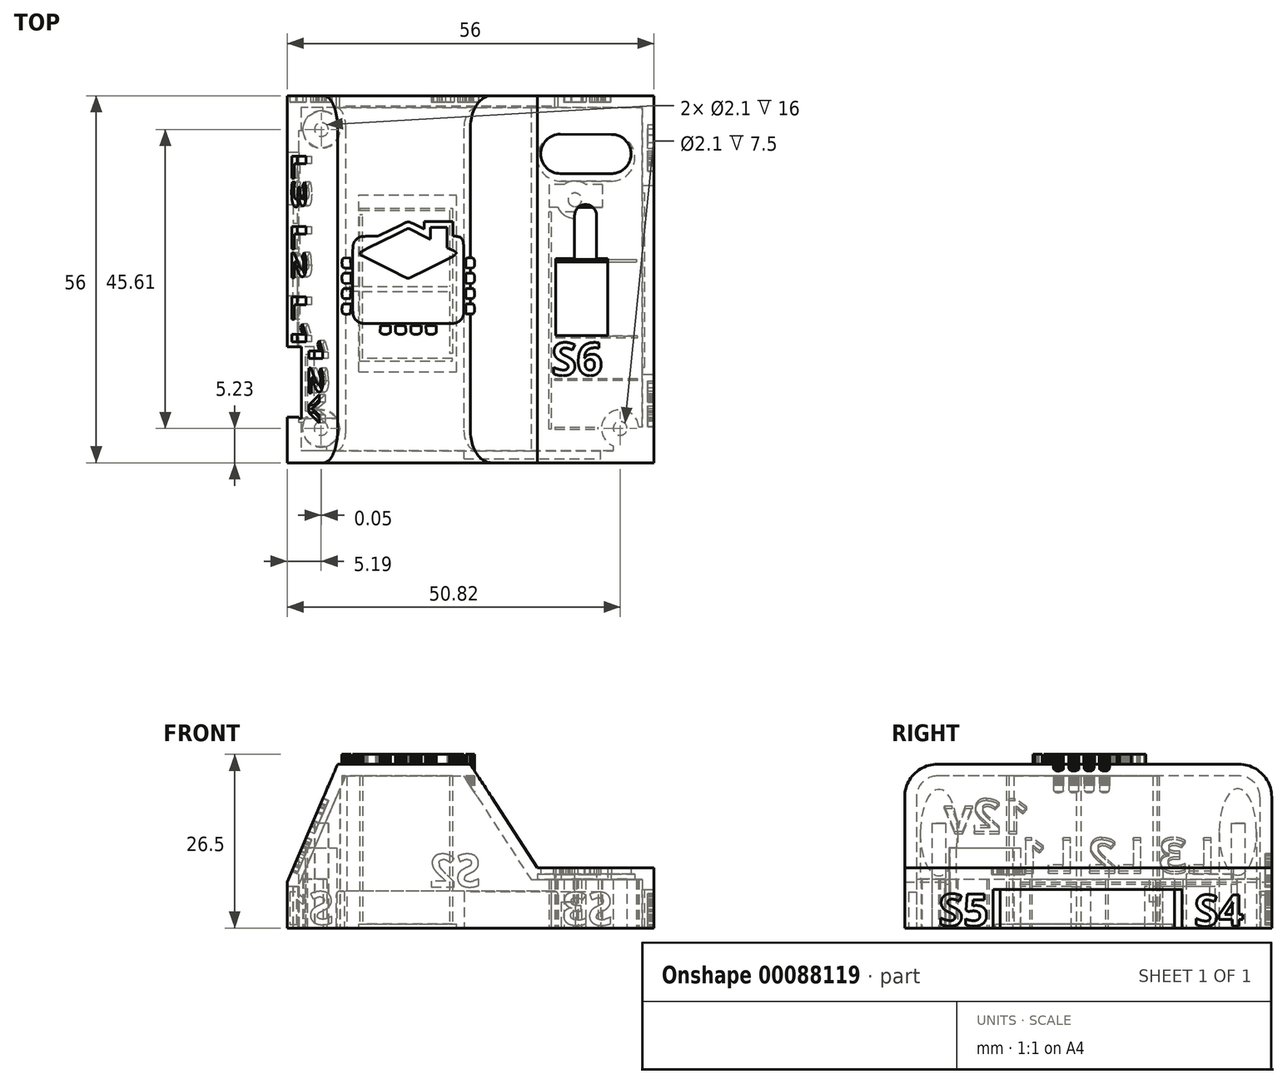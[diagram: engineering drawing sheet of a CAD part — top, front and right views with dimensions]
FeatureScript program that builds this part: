
annotation { "Feature Type Name" : "Feature", "Feature Type Description" : "" }
export const myFeature = defineFeature(function(context is Context, id is Id, definition is map)
    precondition{}
    {
        {
            var Q0;
            Q0=qCreatedBy(makeId("Top.planeOp"),FACE);
            var sketch = newSketch(context, id + "F0", { "sketchPlane" : qUnion([Q0])});
            skLineSegment(sketch, "E0.rect.bottom", {"start": v(22.84, -21.13) * mm, "end": v(-26.83, -21.13) * mm});
            skLineSegment(sketch, "E0.rect.top", {"start": v(22.84, 28.7) * mm, "end": v(-26.83, 28.7) * mm});
            skLineSegment(sketch, "E0.rect.left", {"start": v(22.84, -21.13) * mm, "end": v(22.84, 28.7) * mm});
            skPoint(sketch, "E0.rect.middle", {"position": v(-2, 3.78) * mm});
            skCircle(sketch, "E1", {"center": v(-24.81, -18.99) * mm, "radius": 1.05 * mm});
            skCircle(sketch, "E2", {"center": v(-24.76, 26.62) * mm, "radius": 1.05 * mm});
            skCircle(sketch, "E3", {"center": v(13.92, 15.91) * mm, "radius": 1.05 * mm});
            skLineSegment(sketch, "E4", {"start": v(-2, -21.13) * mm, "end": v(-2, -18.21) * mm});
            skCircle(sketch, "E5.MirrorC", {"center": v(20.82, -18.99) * mm, "radius": 1.05 * mm});
            skLineSegment(sketch, "E6.rect.bottom", {"start": v(24.75, -22.97) * mm, "end": v(-28.75, -22.97) * mm});
            skLineSegment(sketch, "E6.rect.top", {"start": v(24.75, 30.53) * mm, "end": v(-28.75, 30.53) * mm});
            skLineSegment(sketch, "E6.rect.left", {"start": v(24.75, -22.97) * mm, "end": v(24.75, 30.53) * mm});
            skLineSegment(sketch, "E6.rect.right", {"start": v(-28.75, -22.97) * mm, "end": v(-28.75, 30.53) * mm});
            skLineSegment(sketch, "E7.rect.bottom", {"start": v(26, -24.22) * mm, "end": v(-30, -24.22) * mm});
            skLineSegment(sketch, "E7.rect.top", {"start": v(26, 31.78) * mm, "end": v(-30, 31.78) * mm});
            skLineSegment(sketch, "E7.rect.left", {"start": v(26, -24.22) * mm, "end": v(26, 31.78) * mm});
            skLineSegment(sketch, "E7.rect.right", {"start": v(-30, -24.22) * mm, "end": v(-30, 31.78) * mm});
            skPoint(sketch, "E8", {"position": v(8.65, 14) * mm});
            skSolve(sketch);
        }
        {
            var Q0;
            Q0=qSketchRegion(id+"F0",true);
            var Q1;
            Q1=makeQuery(id+"F0.imprint","IMPRINT",FACE,{"disambiguationData":[TD([[makeQuery(id+"F0.imprint","IMPRINT",EDGE,{"derivedFrom":sQuery(id+"F0.wireOp",EDGE,"E1")}),-1.0]])]});
            extrude(context, id + "F1", {"entities" : qUnion([Q0, Q1]), "depth" : 25 * mm});
        }
        {
            var Q0;
            Q0=qCreatedBy(makeId("Front.planeOp"),FACE);
            var sketch = newSketch(context, id + "F2", { "sketchPlane" : qUnion([Q0])});
            skLineSegment(sketch, "E9", {"start": v(0, 0) * mm, "end": v(0, 7) * mm});
            skLineSegment(sketch, "E10", {"start": v(0, 7) * mm, "end": v(26.03, 7) * mm});
            skLineSegment(sketch, "E11", {"start": v(26.03, 9.19) * mm, "end": v(26.03, 25.51) * mm});
            skLineSegment(sketch, "E12", {"start": v(15.3, 7) * mm, "end": v(26.03, 7) * mm});
            skLineSegment(sketch, "E13", {"start": v(0, 7) * mm, "end": v(-30.02, 7) * mm});
            skLineSegment(sketch, "E14", {"start": v(-30.02, 7) * mm, "end": v(-22.06, 25.51) * mm});
            skLineSegment(sketch, "E15", {"start": v(-22.06, 25.51) * mm, "end": v(-2.39, 25.51) * mm});
            skLineSegment(sketch, "E16", {"start": v(26.03, 25.51) * mm, "end": v(-2.39, 25.51) * mm});
            skLineSegment(sketch, "E17", {"start": v(-22.06, 25.51) * mm, "end": v(-30.02, 25.51) * mm});
            skLineSegment(sketch, "E18", {"start": v(-30.02, 25.51) * mm, "end": v(-30.02, 7) * mm});
            skLineSegment(sketch, "E19", {"start": v(18.06, 10.7) * mm, "end": v(18.04, 10.7) * mm});
            skLineSegment(sketch, "E20", {"start": v(19.86, 9.19) * mm, "end": v(8.2, 9.19) * mm});
            skLineSegment(sketch, "E21", {"start": v(8.2, 9.19) * mm, "end": v(-2.39, 25.51) * mm});
            skLineSegment(sketch, "E22", {"start": v(19.86, 9.19) * mm, "end": v(26.03, 9.19) * mm});
            skSolve(sketch);
        }
        {
            var Q0;
            Q0=makeQuery(id+"F2.imprint","IMPRINT",FACE,{"disambiguationData":[TD([[makeQuery(id+"F2.imprint","IMPRINT",EDGE,{"derivedFrom":sQuery(id+"F2.wireOp",EDGE,"E14")}),1.0]])]});
            var Q1;
            {var subQ0=sQuery(id+"F2.wireOp",EDGE,"E11");Q1=makeQuery(id+"F2.imprint","IMPRINT",FACE,{"disambiguationData":[TD([[makeQuery(id+"F2.imprint","IMPRINT",EDGE,{"derivedFrom":subQ0}),1.0]])]});}
            extrude(context, id + "F3", {"entities" : qUnion([Q0, Q1]), "operationType" : NewBodyOperationType.REMOVE, "endBound" : BoundingType.UP_TO_NEXT, "oppositeDirection" : true, "depth" : 25 * mm, "hasSecondDirection" : true, "secondDirectionOppositeDirection" : false, "secondDirectionDepth" : 25 * mm});
        }
        {
            var Q0;
            Q0=makeQuery(id+"F1.opExtrude","CAP_EDGE",EDGE,{"disambiguationData":[OSD([sQuery(id+"F0.wireOp",EDGE,"E7.rect.right")])],"isStart":false});
            var Q1;
            Q1=makeQuery(id+"F3.boolean.opBoolean","COPY",EDGE,{"derivedFrom":makeQuery(id+"F3.opExtrude","TWEAK_EDGE",EDGE,{"derivedFrom":[makeQuery(id+"F1.opExtrude","CAP_FACE",FACE,{"disambiguationData":[OSD([sQuery(id+"F0.wireOp",EDGE,"E1"),sQuery(id+"F0.wireOp",EDGE,"E2"),sQuery(id+"F0.wireOp",EDGE,"E3"),sQuery(id+"F0.wireOp",EDGE,"E5.MirrorC"),sQuery(id+"F0.wireOp",EDGE,"E7.rect.bottom"),sQuery(id+"F0.wireOp",EDGE,"E7.rect.top"),sQuery(id+"F0.wireOp",EDGE,"E7.rect.left"),sQuery(id+"F0.wireOp",EDGE,"E7.rect.right")])],"isStart":false}),makeQuery(id+"F2.imprint","IMPRINT",EDGE,{"derivedFrom":sQuery(id+"F2.wireOp",EDGE,"ff17f17f-c23f-4b7b-92e3-773d52701edb")})]})});
            var Q2;
            Q2=makeQuery(id+"F3.boolean.opBoolean","COPY",EDGE,{"derivedFrom":makeQuery(id+"F3.opExtrude","TWEAK_EDGE",EDGE,{"derivedFrom":[makeQuery(id+"F1.opExtrude","CAP_FACE",FACE,{"disambiguationData":[OSD([sQuery(id+"F0.wireOp",EDGE,"E1"),sQuery(id+"F0.wireOp",EDGE,"E2"),sQuery(id+"F0.wireOp",EDGE,"E3"),sQuery(id+"F0.wireOp",EDGE,"E5.MirrorC"),sQuery(id+"F0.wireOp",EDGE,"E7.rect.bottom"),sQuery(id+"F0.wireOp",EDGE,"E7.rect.top"),sQuery(id+"F0.wireOp",EDGE,"E7.rect.left"),sQuery(id+"F0.wireOp",EDGE,"E7.rect.right")])],"isStart":false}),makeQuery(id+"F2.imprint","IMPRINT",EDGE,{"derivedFrom":sQuery(id+"F2.wireOp",EDGE,"7c30f75c-de24-4105-9ec6-0528e7197d9e")})]})});
            var Q3;
            {var subQ0=sQuery(id+"F2.wireOp",EDGE,"cpQ2IQLn-lepx-jHqE-Occg-QwCyzWVKbBFz");var subQ1=sQuery(id+"F2.wireOp",EDGE,"9136473a-ce9f-4df1-8e41-d79c079f6f02");var subQ2=makeQuery(id+"F2.imprint","INTERSECT",VERTEX,{"disambiguationData":[OD(0.0)],"derivedFrom":[subQ1,subQ0]});var subQ4=makeQuery(id+"F2.imprint","INTERSECT",VERTEX,{"disambiguationData":[OD(1.0)],"derivedFrom":[subQ1,subQ0]});Q3=makeQuery(id+"F3.boolean.opBoolean","COPY",EDGE,{"derivedFrom":makeQuery(id+"F3.opExtrude","TWEAK_EDGE",EDGE,{"derivedFrom":[makeQuery(id+"F1.opExtrude","CAP_FACE",FACE,{"disambiguationData":[OSD([sQuery(id+"F0.wireOp",EDGE,"E1"),sQuery(id+"F0.wireOp",EDGE,"E2"),sQuery(id+"F0.wireOp",EDGE,"E3"),sQuery(id+"F0.wireOp",EDGE,"E5.MirrorC"),sQuery(id+"F0.wireOp",EDGE,"E7.rect.bottom"),sQuery(id+"F0.wireOp",EDGE,"E7.rect.top"),sQuery(id+"F0.wireOp",EDGE,"E7.rect.left"),sQuery(id+"F0.wireOp",EDGE,"E7.rect.right")])],"isStart":false}),makeQuery(id+"F2.imprint","IMPRINT",EDGE,{"disambiguationData":[TD([[subQ4,1.0]])],"derivedFrom":subQ0}),makeQuery(id+"F2.imprint","IMPRINT",EDGE,{"disambiguationData":[TD([[subQ2,1.0]])],"derivedFrom":subQ0}),makeQuery(id+"F2.imprint","IMPRINT",EDGE,{"disambiguationData":[TD([[subQ2,-1.0]])],"derivedFrom":subQ0})]})});}
            var Q4;
            {var subQ0=sQuery(id+"F2.wireOp",EDGE,"cpQ2IQLn-lepx-jHqE-Occg-QwCyzWVKbBFz");var subQ1=sQuery(id+"F2.wireOp",EDGE,"9136473a-ce9f-4df1-8e41-d79c079f6f02");var subQ2=makeQuery(id+"F2.imprint","INTERSECT",VERTEX,{"disambiguationData":[OD(0.0)],"derivedFrom":[subQ1,subQ0]});var subQ3=sQuery(id+"F2.wireOp",EDGE,"7c30f75c-de24-4105-9ec6-0528e7197d9e");var subQ4=makeQuery(id+"F2.imprint","INTERSECT",VERTEX,{"derivedFrom":[subQ3,subQ0]});var subQ5=makeQuery(id+"F2.imprint","INTERSECT",VERTEX,{"disambiguationData":[OD(1.0)],"derivedFrom":[subQ1,subQ0]});Q4=makeQuery(id+"F3.boolean.opBoolean","COPY",EDGE,{"derivedFrom":makeQuery(id+"F3.opExtrude","TWEAK_EDGE",EDGE,{"disambiguationData":[OD(0.0)],"derivedFrom":[makeQuery(id+"F2.imprint","IMPRINT",EDGE,{"disambiguationData":[TD([[subQ4,1.0]])],"derivedFrom":subQ3}),makeQuery(id+"F2.imprint","IMPRINT",EDGE,{"disambiguationData":[TD([[subQ5,1.0]])],"derivedFrom":subQ0}),makeQuery(id+"F2.imprint","IMPRINT",EDGE,{"disambiguationData":[TD([[subQ2,1.0]])],"derivedFrom":subQ0}),makeQuery(id+"F2.imprint","IMPRINT",EDGE,{"disambiguationData":[TD([[subQ2,-1.0]])],"derivedFrom":subQ0})]})});}
            var Q5;
            {var subQ0=sQuery(id+"F2.wireOp",EDGE,"cpQ2IQLn-lepx-jHqE-Occg-QwCyzWVKbBFz");var subQ1=sQuery(id+"F2.wireOp",EDGE,"9136473a-ce9f-4df1-8e41-d79c079f6f02");var subQ2=makeQuery(id+"F2.imprint","INTERSECT",VERTEX,{"disambiguationData":[OD(0.0)],"derivedFrom":[subQ1,subQ0]});var subQ3=sQuery(id+"F2.wireOp",EDGE,"7c30f75c-de24-4105-9ec6-0528e7197d9e");var subQ4=makeQuery(id+"F2.imprint","INTERSECT",VERTEX,{"derivedFrom":[subQ3,subQ0]});var subQ5=makeQuery(id+"F2.imprint","INTERSECT",VERTEX,{"disambiguationData":[OD(1.0)],"derivedFrom":[subQ1,subQ0]});Q5=makeQuery(id+"F3.boolean.opBoolean","COPY",EDGE,{"derivedFrom":makeQuery(id+"F3.opExtrude","TWEAK_EDGE",EDGE,{"disambiguationData":[OD(1.0)],"derivedFrom":[makeQuery(id+"F2.imprint","IMPRINT",EDGE,{"disambiguationData":[TD([[subQ4,1.0]])],"derivedFrom":subQ3}),makeQuery(id+"F2.imprint","IMPRINT",EDGE,{"disambiguationData":[TD([[subQ5,1.0]])],"derivedFrom":subQ0}),makeQuery(id+"F2.imprint","IMPRINT",EDGE,{"disambiguationData":[TD([[subQ2,1.0]])],"derivedFrom":subQ0}),makeQuery(id+"F2.imprint","IMPRINT",EDGE,{"disambiguationData":[TD([[subQ2,-1.0]])],"derivedFrom":subQ0})]})});}
            var Q6;
            Q6=makeQuery(id+"F1.opExtrude","CAP_EDGE",EDGE,{"disambiguationData":[OSD([sQuery(id+"F0.wireOp",EDGE,"E7.rect.bottom")])],"isStart":false});
            var Q7;
            {var subQ0=sQuery(id+"F2.wireOp",EDGE,"cpQ2IQLn-lepx-jHqE-Occg-QwCyzWVKbBFz");var subQ1=sQuery(id+"F2.wireOp",EDGE,"9136473a-ce9f-4df1-8e41-d79c079f6f02");var subQ2=makeQuery(id+"F2.imprint","INTERSECT",VERTEX,{"disambiguationData":[OD(0.0)],"derivedFrom":[subQ1,subQ0]});var subQ4=makeQuery(id+"F2.imprint","INTERSECT",VERTEX,{"disambiguationData":[OD(1.0)],"derivedFrom":[subQ1,subQ0]});Q7=makeQuery(id+"F3.boolean.opBoolean","COPY",EDGE,{"derivedFrom":makeQuery(id+"F3.opExtrude","TWEAK_EDGE",EDGE,{"derivedFrom":[makeQuery(id+"F1.opExtrude","SWEPT_FACE",FACE,{"disambiguationData":[OSD([sQuery(id+"F0.wireOp",EDGE,"E7.rect.bottom")])]}),makeQuery(id+"F2.imprint","IMPRINT",EDGE,{"disambiguationData":[TD([[subQ4,1.0]])],"derivedFrom":subQ0}),makeQuery(id+"F2.imprint","IMPRINT",EDGE,{"disambiguationData":[TD([[subQ2,1.0]])],"derivedFrom":subQ0}),makeQuery(id+"F2.imprint","IMPRINT",EDGE,{"disambiguationData":[TD([[subQ2,-1.0]])],"derivedFrom":subQ0})]})});}
            var Q8;
            Q8=makeQuery(id+"F1.opExtrude","CAP_EDGE",EDGE,{"disambiguationData":[OSD([sQuery(id+"F0.wireOp",EDGE,"E7.rect.top")])],"isStart":false});
            var Q9;
            {var subQ0=sQuery(id+"F2.wireOp",EDGE,"cpQ2IQLn-lepx-jHqE-Occg-QwCyzWVKbBFz");var subQ1=sQuery(id+"F2.wireOp",EDGE,"9136473a-ce9f-4df1-8e41-d79c079f6f02");var subQ2=makeQuery(id+"F2.imprint","INTERSECT",VERTEX,{"disambiguationData":[OD(0.0)],"derivedFrom":[subQ1,subQ0]});var subQ4=makeQuery(id+"F2.imprint","INTERSECT",VERTEX,{"disambiguationData":[OD(1.0)],"derivedFrom":[subQ1,subQ0]});Q9=makeQuery(id+"F3.boolean.opBoolean","COPY",EDGE,{"derivedFrom":makeQuery(id+"F3.opExtrude","TWEAK_EDGE",EDGE,{"derivedFrom":[makeQuery(id+"F1.opExtrude","SWEPT_FACE",FACE,{"disambiguationData":[OSD([sQuery(id+"F0.wireOp",EDGE,"E7.rect.top")])]}),makeQuery(id+"F2.imprint","IMPRINT",EDGE,{"disambiguationData":[TD([[subQ4,1.0]])],"derivedFrom":subQ0}),makeQuery(id+"F2.imprint","IMPRINT",EDGE,{"disambiguationData":[TD([[subQ2,1.0]])],"derivedFrom":subQ0}),makeQuery(id+"F2.imprint","IMPRINT",EDGE,{"disambiguationData":[TD([[subQ2,-1.0]])],"derivedFrom":subQ0})]})});}
            var Q10;
            Q10=makeQuery(id+"F3.boolean.opBoolean","COPY",EDGE,{"derivedFrom":makeQuery(id+"F3.opExtrude","TWEAK_EDGE",EDGE,{"derivedFrom":[makeQuery(id+"F1.opExtrude","CAP_FACE",FACE,{"disambiguationData":[OSD([sQuery(id+"F0.wireOp",EDGE,"E1"),sQuery(id+"F0.wireOp",EDGE,"E2"),sQuery(id+"F0.wireOp",EDGE,"E3"),sQuery(id+"F0.wireOp",EDGE,"E5.MirrorC"),sQuery(id+"F0.wireOp",EDGE,"E7.rect.bottom"),sQuery(id+"F0.wireOp",EDGE,"E7.rect.top"),sQuery(id+"F0.wireOp",EDGE,"E7.rect.left"),sQuery(id+"F0.wireOp",EDGE,"E7.rect.right")])],"isStart":false}),makeQuery(id+"F2.imprint","IMPRINT",EDGE,{"derivedFrom":sQuery(id+"F2.wireOp",EDGE,"99fa5713-44e2-4710-8a3e-a5a5802f03ed")})]})});
            var Q11;
            Q11=makeQuery(id+"F3.boolean.opBoolean","COPY",EDGE,{"derivedFrom":makeQuery(id+"F3.opExtrude","TWEAK_EDGE",EDGE,{"derivedFrom":[makeQuery(id+"F1.opExtrude","CAP_FACE",FACE,{"disambiguationData":[OSD([sQuery(id+"F0.wireOp",EDGE,"E1"),sQuery(id+"F0.wireOp",EDGE,"E2"),sQuery(id+"F0.wireOp",EDGE,"E3"),sQuery(id+"F0.wireOp",EDGE,"E5.MirrorC"),sQuery(id+"F0.wireOp",EDGE,"E7.rect.bottom"),sQuery(id+"F0.wireOp",EDGE,"E7.rect.top"),sQuery(id+"F0.wireOp",EDGE,"E7.rect.left"),sQuery(id+"F0.wireOp",EDGE,"E7.rect.right")])],"isStart":false}),makeQuery(id+"F2.imprint","IMPRINT",EDGE,{"derivedFrom":sQuery(id+"F2.wireOp",EDGE,"E14")})]})});
            var Q12;
            Q12=makeQuery(id+"F3.boolean.opBoolean","COPY",EDGE,{"derivedFrom":makeQuery(id+"F3.opExtrude","TWEAK_EDGE",EDGE,{"derivedFrom":[makeQuery(id+"F1.opExtrude","CAP_FACE",FACE,{"disambiguationData":[OSD([sQuery(id+"F0.wireOp",EDGE,"E1"),sQuery(id+"F0.wireOp",EDGE,"E2"),sQuery(id+"F0.wireOp",EDGE,"E3"),sQuery(id+"F0.wireOp",EDGE,"E5.MirrorC"),sQuery(id+"F0.wireOp",EDGE,"E7.rect.bottom"),sQuery(id+"F0.wireOp",EDGE,"E7.rect.top"),sQuery(id+"F0.wireOp",EDGE,"E7.rect.left"),sQuery(id+"F0.wireOp",EDGE,"E7.rect.right")])],"isStart":false}),makeQuery(id+"F2.imprint","IMPRINT",EDGE,{"derivedFrom":sQuery(id+"F2.wireOp",EDGE,"E21")})]})});
            var Q13;
            Q13=makeQuery(id+"F3.boolean.opBoolean","COPY",EDGE,{"derivedFrom":makeQuery(id+"F3.opExtrude","TWEAK_EDGE",EDGE,{"derivedFrom":[makeQuery(id+"F2.imprint","IMPRINT",EDGE,{"derivedFrom":sQuery(id+"F2.wireOp",EDGE,"E20")}),makeQuery(id+"F2.imprint","IMPRINT",EDGE,{"derivedFrom":sQuery(id+"F2.wireOp",EDGE,"E21")})]})});
            var Q14;
            Q14=makeQuery(id+"F3.boolean.opBoolean","COPY",EDGE,{"derivedFrom":makeQuery(id+"F3.opExtrude","TWEAK_EDGE",EDGE,{"derivedFrom":[makeQuery(id+"F1.opExtrude","SWEPT_FACE",FACE,{"disambiguationData":[OSD([sQuery(id+"F0.wireOp",EDGE,"E7.rect.bottom")])]}),makeQuery(id+"F2.imprint","IMPRINT",EDGE,{"derivedFrom":sQuery(id+"F2.wireOp",EDGE,"E21")})]})});
            var Q15;
            Q15=makeQuery(id+"F3.boolean.opBoolean","COPY",EDGE,{"derivedFrom":makeQuery(id+"F3.opExtrude","TWEAK_EDGE",EDGE,{"derivedFrom":[makeQuery(id+"F1.opExtrude","SWEPT_FACE",FACE,{"disambiguationData":[OSD([sQuery(id+"F0.wireOp",EDGE,"E7.rect.top")])]}),makeQuery(id+"F2.imprint","IMPRINT",EDGE,{"derivedFrom":sQuery(id+"F2.wireOp",EDGE,"E21")})]})});
            var Q16;
            Q16=makeQuery(id+"F3.boolean.opBoolean","COPY",EDGE,{"derivedFrom":makeQuery(id+"F3.opExtrude","TWEAK_EDGE",EDGE,{"derivedFrom":[makeQuery(id+"F1.opExtrude","SWEPT_FACE",FACE,{"disambiguationData":[OSD([sQuery(id+"F0.wireOp",EDGE,"E7.rect.left")])]}),makeQuery(id+"F2.imprint","IMPRINT",EDGE,{"derivedFrom":sQuery(id+"F2.wireOp",EDGE,"E20")}),makeQuery(id+"F2.imprint","IMPRINT",EDGE,{"derivedFrom":sQuery(id+"F2.wireOp",EDGE,"E22")})]})});
            var Q17;
            Q17=makeQuery(id+"F3.boolean.opBoolean","COPY",EDGE,{"derivedFrom":makeQuery(id+"F3.opExtrude","TWEAK_EDGE",EDGE,{"derivedFrom":[makeQuery(id+"F2.imprint","IMPRINT",EDGE,{"derivedFrom":sQuery(id+"F2.wireOp",EDGE,"E20")}),makeQuery(id+"F2.imprint","IMPRINT",EDGE,{"derivedFrom":sQuery(id+"F2.wireOp",EDGE,"E21")}),makeQuery(id+"F2.imprint","IMPRINT",EDGE,{"derivedFrom":sQuery(id+"F2.wireOp",EDGE,"E22")})]})});
            fillet(context, id + "F4", {"entities" : qUnion([Q0, Q1, Q2, Q3, Q4, Q5, Q6, Q7, Q8, Q9, Q10, Q11, Q12, Q13, Q14, Q15, Q16, Q17]), "radius" : 5 * mm, "tangentPropagation" : true, "allowEdgeOverflow" : false});
        }
        {
            var Q0;
            Q0=makeQuery(id+"F1.opExtrude","SWEPT_BODY",BODY,{"disambiguationData":[OSD([sQuery(id+"F0.wireOp",EDGE,"E1"),sQuery(id+"F0.wireOp",EDGE,"E2"),sQuery(id+"F0.wireOp",EDGE,"E3"),sQuery(id+"F0.wireOp",EDGE,"E5.MirrorC"),sQuery(id+"F0.wireOp",EDGE,"E7.rect.bottom"),sQuery(id+"F0.wireOp",EDGE,"E7.rect.top"),sQuery(id+"F0.wireOp",EDGE,"E7.rect.left"),sQuery(id+"F0.wireOp",EDGE,"E7.rect.right")])]});
            transform(context, id + "F5", {"entities" : qUnion([Q0]), "transformType" : TransformType.TRANSLATION_3D, "dx" : -5 * mm, "dy" : -12 * mm, "dz" : 0 * mm, "makeCopy" : false});
        }
        {
            var Q0;
            Q0=makeQuery(id+"F1.opExtrude","CAP_FACE",FACE,{"disambiguationData":[OSD([sQuery(id+"F0.wireOp",EDGE,"E1"),sQuery(id+"F0.wireOp",EDGE,"E2"),sQuery(id+"F0.wireOp",EDGE,"E3"),sQuery(id+"F0.wireOp",EDGE,"E5.MirrorC"),sQuery(id+"F0.wireOp",EDGE,"E7.rect.bottom"),sQuery(id+"F0.wireOp",EDGE,"E7.rect.top"),sQuery(id+"F0.wireOp",EDGE,"E7.rect.left"),sQuery(id+"F0.wireOp",EDGE,"E7.rect.right")])],"isStart":true});
            shell(context, id + "F6", {"entities" : qUnion([Q0]), "thickness" : 1.8 * mm});
        }
        {
            var Q0;
            Q0=makeQuery(id+"F1.opExtrude","SWEPT_FACE",FACE,{"disambiguationData":[OSD([sQuery(id+"F0.wireOp",EDGE,"E7.rect.left")])]});
            cPlane(context, id + "F7", {"entities" : qUnion([Q0]), "cplaneType" : CPlaneType.OFFSET, "offset" : 0 * mm, "width" : 150 * mm, "height" : 150 * mm});
        }
        {
            var Q0;
            Q0=qCreatedBy(id+"F7.planeOp",FACE);
            var sketch = newSketch(context, id + "F8", { "sketchPlane" : qUnion([Q0])});
            skLineSegment(sketch, "E23.bottom", {"start": v(6.92, 0) * mm, "end": v(-20.2, 0) * mm});
            skLineSegment(sketch, "E23.top", {"start": v(6.12, 5.87) * mm, "end": v(-20.2, 5.87) * mm});
            skLineSegment(sketch, "E24", {"start": v(-20.2, 5.87) * mm, "end": v(-21.64, 5.87) * mm});
            skLineSegment(sketch, "E25", {"start": v(-21.64, 5.87) * mm, "end": v(-21.64, 0) * mm});
            skLineSegment(sketch, "E26", {"start": v(-21.64, 0) * mm, "end": v(-20.2, 0) * mm});
            skLineSegment(sketch, "E27", {"start": v(6.12, 5.87) * mm, "end": v(6.12, 0) * mm});
            skPoint(sketch, "E28.orphan", {"position": v(7.84, 0) * mm});
            skLineSegment(sketch, "E29", {"start": v(4.97, 0) * mm, "end": v(4.97, 5.87) * mm});
            skLineSegment(sketch, "E30", {"start": v(-21.64, 5.87) * mm, "end": v(-22.73, 5.87) * mm});
            skLineSegment(sketch, "E31", {"start": v(-22.73, 5.87) * mm, "end": v(-22.73, 0) * mm});
            skLineSegment(sketch, "E32", {"start": v(-22.73, 0) * mm, "end": v(-21.64, 0) * mm});
            skSolve(sketch);
        }
        {
            var Q0;
            {var subQ1=sQuery(id+"F8.wireOp",EDGE,"E24");Q0=makeQuery(id+"F8.imprint","IMPRINT",FACE,{"disambiguationData":[TD([[makeQuery(id+"F8.imprint","IMPRINT",EDGE,{"derivedFrom":subQ1}),1.0]])]});}
            extrude(context, id + "F9", {"entities" : qUnion([Q0]), "operationType" : NewBodyOperationType.REMOVE, "oppositeDirection" : true, "depth" : (1.7 - 0.3) * mm});
        }
        {
            var Q0;
            Q0=makeQuery(id+"F8.imprint","IMPRINT",FACE,{"disambiguationData":[TD([[makeQuery(id+"F8.imprint","IMPRINT",EDGE,{"derivedFrom":sQuery(id+"F8.wireOp",EDGE,"E25")}),-1.0]])]});
            var Q1;
            {var subQ0=sQuery(id+"F8.wireOp",EDGE,"E27");Q1=makeQuery(id+"F8.imprint","IMPRINT",FACE,{"disambiguationData":[TD([[makeQuery(id+"F8.imprint","IMPRINT",EDGE,{"derivedFrom":subQ0}),-1.0]])]});}
            extrude(context, id + "F10", {"entities" : qUnion([Q0, Q1]), "operationType" : NewBodyOperationType.REMOVE, "oppositeDirection" : true, "depth" : 2 * mm});
        }
        {
            var Q0;
            Q0=makeQuery(id+"F1.opExtrude","SWEPT_FACE",FACE,{"disambiguationData":[OSD([sQuery(id+"F0.wireOp",EDGE,"E7.rect.right")])]});
            cPlane(context, id + "F11", {"entities" : qUnion([Q0]), "cplaneType" : CPlaneType.OFFSET, "offset" : 0 * mm, "width" : 150 * mm, "height" : 150 * mm});
        }
        {
            var Q0;
            Q0=qCreatedBy(id+"F11.planeOp",FACE);
            var sketch = newSketch(context, id + "F12", { "sketchPlane" : qUnion([Q0])});
            skLineSegment(sketch, "E33.top", {"start": v(-11.15, 6.31) * mm, "end": v(-3.45, 6.31) * mm});
            skLineSegment(sketch, "E34", {"start": v(27.25, 11.15) * mm, "end": v(27.25, 11.15) * mm});
            skLineSegment(sketch, "E35", {"start": v(-11.15, 0) * mm, "end": v(-11.15, 6.31) * mm});
            skPoint(sketch, "E36.start.orphan", {"position": v(-15.15, 0) * mm});
            skLineSegment(sketch, "E37", {"start": v(29.28, 0) * mm, "end": v(-11.15, 0) * mm});
            skLineSegment(sketch, "E38", {"start": v(-10.29, 6.31) * mm, "end": v(-10.29, 0) * mm});
            skLineSegment(sketch, "E39", {"start": v(19.35, 12.2) * mm, "end": v(29.28, 12.2) * mm});
            skLineSegment(sketch, "E40", {"start": v(-11.15, 3.16) * mm, "end": v(-3.45, 3.16) * mm, "construction": true});
            skLineSegment(sketch, "E41", {"start": v(-3.45, 3.16) * mm, "end": v(-0.05, 3.16) * mm, "construction": true});
            skLineSegment(sketch, "E42", {"start": v(-0.05, 3.16) * mm, "end": v(7.65, 3.16) * mm, "construction": true});
            skLineSegment(sketch, "E43", {"start": v(7.65, 3.16) * mm, "end": v(11.05, 3.16) * mm, "construction": true});
            skLineSegment(sketch, "E44.trimOffspring", {"start": v(11.05, 6.31) * mm, "end": v(18.53, 6.31) * mm});
            skLineSegment(sketch, "E45", {"start": v(11.9, 6.31) * mm, "end": v(11.9, 0) * mm});
            skLineSegment(sketch, "E46", {"start": v(0, 6.31) * mm, "end": v(7.65, 6.31) * mm});
            skLineSegment(sketch, "E47", {"start": v(7.65, 0) * mm, "end": v(0, 0) * mm});
            skLineSegment(sketch, "E48", {"start": v(-3.45, 0) * mm, "end": v(-11.15, 0) * mm});
            skLineSegment(sketch, "E49", {"start": v(30.08, 0) * mm, "end": v(11.05, 0) * mm});
            skLineSegment(sketch, "E50.bottom", {"start": v(-0.32, 0) * mm, "end": v(-3.15, 0) * mm});
            skLineSegment(sketch, "E50.top", {"start": v(-0.32, 6.31) * mm, "end": v(-3.15, 6.31) * mm});
            skLineSegment(sketch, "E50.left", {"start": v(-0.32, 0) * mm, "end": v(-0.32, 6.31) * mm});
            skLineSegment(sketch, "E50.right", {"start": v(-3.15, 0) * mm, "end": v(-3.15, 6.31) * mm});
            skLineSegment(sketch, "E51.bottom", {"start": v(10.8, 0) * mm, "end": v(7.92, 0) * mm});
            skLineSegment(sketch, "E51.top", {"start": v(10.8, 6.31) * mm, "end": v(7.92, 6.31) * mm});
            skLineSegment(sketch, "E51.left", {"start": v(10.8, 0) * mm, "end": v(10.8, 6.31) * mm});
            skLineSegment(sketch, "E51.right", {"start": v(7.92, 0) * mm, "end": v(7.92, 6.31) * mm});
            skLineSegment(sketch, "E52", {"start": v(-3.45, 6.31) * mm, "end": v(11.05, 6.31) * mm});
            skLineSegment(sketch, "E53", {"start": v(29.28, 12.2) * mm, "end": v(29.28, 0) * mm});
            skPoint(sketch, "E54.end.orphan", {"position": v(30.08, 11.15) * mm});
            skPoint(sketch, "E54.start.orphan", {"position": v(30.08, 12.2) * mm});
            skLineSegment(sketch, "E55", {"start": v(18.53, 6.31) * mm, "end": v(18.53, 12.2) * mm});
            skLineSegment(sketch, "E56", {"start": v(18.53, 12.2) * mm, "end": v(19.35, 12.2) * mm});
            skPoint(sketch, "E57.start.orphan", {"position": v(19.35, 11.15) * mm});
            skPoint(sketch, "E58.end.orphan", {"position": v(19.35, 0) * mm});
            skPoint(sketch, "E58.start.orphan", {"position": v(19.35, 6.31) * mm});
            skLineSegment(sketch, "E59", {"start": v(28.38, 0) * mm, "end": v(28.38, 12.2) * mm});
            skLineSegment(sketch, "E60", {"start": v(19.35, 12.2) * mm, "end": v(19.35, 0) * mm});
            skLineSegment(sketch, "E61", {"start": v(18.53, 6.31) * mm, "end": v(18.53, 0) * mm});
            skSolve(sketch);
        }
        {
            var Q0;
            {var subQ0=sQuery(id+"F12.wireOp",EDGE,"E35");Q0=makeQuery(id+"F12.imprint","IMPRINT",FACE,{"disambiguationData":[TD([[makeQuery(id+"F12.imprint","IMPRINT",EDGE,{"derivedFrom":subQ0}),-1.0]])]});}
            var Q1;
            {var subQ1=sQuery(id+"F12.wireOp",EDGE,"E38");Q1=makeQuery(id+"F12.imprint","IMPRINT",FACE,{"disambiguationData":[TD([[makeQuery(id+"F12.imprint","IMPRINT",EDGE,{"derivedFrom":subQ1}),1.0]])]});}
            var Q2;
            {var subQ0=sQuery(id+"F12.wireOp",EDGE,"LVVauTd6-uSLQ-SWm0-nvuu-HrEgJgk2loCY");Q2=makeQuery(id+"F12.imprint","IMPRINT",FACE,{"disambiguationData":[TD([[makeQuery(id+"F12.imprint","IMPRINT",EDGE,{"derivedFrom":subQ0}),-1.0]])]});}
            var Q3;
            Q3=makeQuery(id+"F12.imprint","IMPRINT",FACE,{"disambiguationData":[TD([[makeQuery(id+"F12.imprint","IMPRINT",EDGE,{"derivedFrom":sQuery(id+"F12.wireOp",EDGE,"Bzj0w9RH-aYdH-ZF7y-Z4mK-Pif1xP8myCSu")}),1.0]])]});
            var Q4;
            Q4=makeQuery(id+"F12.imprint","IMPRINT",FACE,{"disambiguationData":[TD([[makeQuery(id+"F12.imprint","IMPRINT",EDGE,{"derivedFrom":sQuery(id+"F12.wireOp",EDGE,"E50.bottom")}),-1.0]])]});
            var Q5;
            {var subQ1=sQuery(id+"F12.wireOp",EDGE,"E47");Q5=makeQuery(id+"F12.imprint","IMPRINT",FACE,{"disambiguationData":[TD([[makeQuery(id+"F12.imprint","IMPRINT",EDGE,{"derivedFrom":subQ1}),-1.0]])]});}
            var Q6;
            Q6=makeQuery(id+"F12.imprint","IMPRINT",FACE,{"disambiguationData":[TD([[makeQuery(id+"F12.imprint","IMPRINT",EDGE,{"derivedFrom":sQuery(id+"F12.wireOp",EDGE,"E51.bottom")}),-1.0]])]});
            var Q7;
            {var subQ3=sQuery(id+"F12.wireOp",EDGE,"E45");Q7=makeQuery(id+"F12.imprint","IMPRINT",FACE,{"disambiguationData":[TD([[makeQuery(id+"F12.imprint","IMPRINT",EDGE,{"derivedFrom":subQ3}),-1.0]])]});}
            var Q8;
            {var subQ2=sQuery(id+"F12.wireOp",EDGE,"E59");Q8=makeQuery(id+"F12.imprint","IMPRINT",FACE,{"disambiguationData":[TD([[makeQuery(id+"F12.imprint","IMPRINT",EDGE,{"derivedFrom":subQ2}),1.0]])]});}
            var Q9;
            {var subQ2=sQuery(id+"F12.wireOp",EDGE,"E45");Q9=makeQuery(id+"F12.imprint","IMPRINT",FACE,{"disambiguationData":[TD([[makeQuery(id+"F12.imprint","IMPRINT",EDGE,{"derivedFrom":subQ2}),1.0]])]});}
            extrude(context, id + "F13", {"entities" : qUnion([Q0, Q1, Q2, Q3, Q4, Q5, Q6, Q7, Q8, Q9]), "operationType" : NewBodyOperationType.REMOVE, "oppositeDirection" : true, "depth" : 1.6 * mm});
        }
        {
            var Q0;
            {var subQ0=sQuery(id+"F12.wireOp",EDGE,"E35");Q0=makeQuery(id+"F12.imprint","IMPRINT",FACE,{"disambiguationData":[TD([[makeQuery(id+"F12.imprint","IMPRINT",EDGE,{"derivedFrom":subQ0}),-1.0]])]});}
            var Q1;
            Q1=makeQuery(id+"F12.imprint","IMPRINT",FACE,{"disambiguationData":[TD([[makeQuery(id+"F12.imprint","IMPRINT",EDGE,{"derivedFrom":sQuery(id+"F12.wireOp",EDGE,"E55")}),-1.0]])]});
            var Q2;
            {var subQ0=sQuery(id+"F12.wireOp",EDGE,"E53");Q2=makeQuery(id+"F12.imprint","IMPRINT",FACE,{"disambiguationData":[TD([[makeQuery(id+"F12.imprint","IMPRINT",EDGE,{"derivedFrom":subQ0}),-1.0]])]});}
            var Q3;
            {var subQ2=sQuery(id+"F12.wireOp",EDGE,"E59");Q3=makeQuery(id+"F12.imprint","IMPRINT",FACE,{"disambiguationData":[TD([[makeQuery(id+"F12.imprint","IMPRINT",EDGE,{"derivedFrom":subQ2}),1.0]])]});}
            extrude(context, id + "F14", {"entities" : qUnion([Q0, Q1, Q2, Q3]), "operationType" : NewBodyOperationType.REMOVE, "oppositeDirection" : true, "depth" : 8 * mm});
        }
        {
            var Q0;
            Q0=qCreatedBy(makeId("Top.planeOp"),FACE);
            var sketch = newSketch(context, id + "F15", { "sketchPlane" : qUnion([Q0])});
            skLineSegment(sketch, "E62.bottom", {"start": v(-27.19, -29.45) * mm, "end": v(-33.17, -29.45) * mm});
            skLineSegment(sketch, "E62.top", {"start": v(-27.19, -20) * mm, "end": v(-33.17, -20) * mm});
            skLineSegment(sketch, "E62.left", {"start": v(-27.19, -29.45) * mm, "end": v(-27.19, -21.32) * mm});
            skLineSegment(sketch, "E62.right", {"start": v(-33.17, -29.45) * mm, "end": v(-33.17, -21.32) * mm});
            skLineSegment(sketch, "E63", {"start": v(-33.17, -20.99) * mm, "end": v(-27.19, -20.99) * mm});
            skLineSegment(sketch, "E64", {"start": v(-33.17, -21.32) * mm, "end": v(-27.19, -21.32) * mm});
            skLineSegment(sketch, "E65.trimOffspring", {"start": v(-27.19, -20.99) * mm, "end": v(-27.19, -20) * mm});
            skLineSegment(sketch, "E66.trimOffspring", {"start": v(-33.17, -20.99) * mm, "end": v(-33.17, -20) * mm});
            skSolve(sketch);
        }
        {
            var Q0;
            Q0=qSketchRegion(id+"F15",true);
            var Q1;
            {var subQ0=sQuery(id+"F12.wireOp",EDGE,"E39");Q1=makeQuery(id+"F14.boolean.opBoolean","COPY",FACE,{"derivedFrom":makeQuery(id+"F14.opExtrude","SWEPT_FACE",FACE,{"disambiguationData":[OSD([subQ0]),TDD([makeQuery(id+"F12.imprint","IMPRINT",EDGE,{"disambiguationData":[TD([[makeQuery(id+"F12.imprint","INTERSECT",VERTEX,{"derivedFrom":[subQ0,sQuery(id+"F12.wireOp",EDGE,"E54")]}),1.0]])],"derivedFrom":subQ0})])]})});}
            extrude(context, id + "F16", {"entities" : qUnion([Q0]), "operationType" : NewBodyOperationType.REMOVE, "endBound" : BoundingType.UP_TO_SURFACE, "endBoundEntityFace" : qUnion([Q1]), "depth" : 11.3 * mm});
        }
        {
            var Q0;
            Q0=makeQuery(id+"F1.opExtrude","SWEPT_FACE",FACE,{"disambiguationData":[OSD([sQuery(id+"F0.wireOp",EDGE,"E7.rect.top")])]});
            cPlane(context, id + "F17", {"entities" : qUnion([Q0]), "cplaneType" : CPlaneType.OFFSET, "offset" : 0 * mm, "width" : 150 * mm, "height" : 150 * mm});
        }
        {
            var Q0;
            Q0=qCreatedBy(id+"F17.planeOp",FACE);
            var sketch = newSketch(context, id + "F18", { "sketchPlane" : qUnion([Q0])});
            skLineSegment(sketch, "E67.bottom", {"start": v(-6.36, 0) * mm, "end": v(27.5, 0) * mm});
            skLineSegment(sketch, "E67.left", {"start": v(-6.36, 0) * mm, "end": v(-6.36, 2.05) * mm});
            skLineSegment(sketch, "E68", {"start": v(-5.32, 3.26) * mm, "end": v(-5.32, 0) * mm});
            skLineSegment(sketch, "E69", {"start": v(27.5, 2.61) * mm, "end": v(27.5, 0) * mm});
            skLineSegment(sketch, "E70", {"start": v(26.27, 5.04) * mm, "end": v(26.27, 0) * mm});
            skPoint(sketch, "E71.visualSharp", {"position": v(-6.36, 7.05) * mm});
            skLineSegment(sketch, "E72", {"start": v(24.5, 5.61) * mm, "end": v(-1.9, 5.61) * mm});
            skPoint(sketch, "E73.visualSharp", {"position": v(-3.28, 5.61) * mm});
            skPoint(sketch, "E74.visualSharp", {"position": v(27.5, 5.61) * mm});
            skLineSegment(sketch, "E75", {"start": v(-6.36, 2.05) * mm, "end": v(-6.36, 5.08) * mm});
            skLineSegment(sketch, "E76", {"start": v(-5.83, 5.61) * mm, "end": v(-1.9, 5.61) * mm});
            skPoint(sketch, "E77.visualSharp", {"position": v(-6.36, 5.61) * mm});
            skArc(sketch, "E77.filletArc", {"start": v(-5.83, 5.61) * mm, "mid": v(-6.2, 5.45) * mm, "end": v(-6.36, 5.08) * mm});
            skLineSegment(sketch, "E78", {"start": v(-5.32, 3.26) * mm, "end": v(-5.32, 5.61) * mm});
            skLineSegment(sketch, "E79", {"start": v(24.5, 5.61) * mm, "end": v(26.98, 5.61) * mm});
            skLineSegment(sketch, "E80", {"start": v(27.5, 2.61) * mm, "end": v(27.5, 5.08) * mm});
            skLineSegment(sketch, "E81", {"start": v(26.27, 5.04) * mm, "end": v(26.27, 5.61) * mm});
            skArc(sketch, "E82.filletArc", {"start": v(27.5, 5.08) * mm, "mid": v(27.35, 5.45) * mm, "end": v(26.98, 5.61) * mm});
            skSolve(sketch);
        }
        {
            var Q0;
            Q0=qSketchRegion(id+"F18",true);
            extrude(context, id + "F19", {"entities" : qUnion([Q0]), "operationType" : NewBodyOperationType.REMOVE, "oppositeDirection" : true, "depth" : 1.6 * mm});
        }
        {
            var Q0;
            Q0=qCreatedBy(makeId("Top.planeOp"),FACE);
            var sketch = newSketch(context, id + "F20", { "sketchPlane" : qUnion([Q0])});
            skArc(sketch, "E83", {"start": v(6.16, 2.02) * mm, "mid": v(8.9, 0.56) * mm, "end": v(11.63, 2.02) * mm});
            skLineSegment(sketch, "E84", {"start": v(11.63, 2.02) * mm, "end": v(6.16, 2.02) * mm});
            skSolve(sketch);
        }
        {
            var Q0;
            Q0=qSketchRegion(id+"F20",true);
            extrude(context, id + "F21", {"entities" : qUnion([Q0]), "operationType" : NewBodyOperationType.REMOVE, "depth" : 4 * mm});
        }
        {
            var Q0;
            {var subQ0=sQuery(id+"F18.wireOp",EDGE,"E67.left");Q0=makeQuery(id+"F18.imprint","IMPRINT",FACE,{"disambiguationData":[TD([[makeQuery(id+"F18.imprint","IMPRINT",EDGE,{"derivedFrom":subQ0}),-1.0]])]});}
            var Q1;
            {var subQ0=sQuery(id+"F18.wireOp",EDGE,"E67.right");Q1=makeQuery(id+"F18.imprint","IMPRINT",FACE,{"disambiguationData":[TD([[makeQuery(id+"F18.imprint","IMPRINT",EDGE,{"derivedFrom":subQ0}),1.0]])]});}
            extrude(context, id + "F22", {"entities" : qUnion([Q0, Q1]), "operationType" : NewBodyOperationType.REMOVE, "oppositeDirection" : true, "depth" : 2 * mm});
        }
        {
            var Q0;
            Q0=qCreatedBy(makeId("Top.planeOp"),FACE);
            var sketch = newSketch(context, id + "F23", { "sketchPlane" : qUnion([Q0])});
            skLineSegment(sketch, "E85", {"start": v(21, 19.9) * mm, "end": v(21, 10.4) * mm, "construction": true});
            skLineSegment(sketch, "E86", {"start": v(12.22, 0) * mm, "end": v(12.22, -5.06) * mm});
            skLineSegment(sketch, "E87", {"start": v(12.22, 0) * mm, "end": v(12.22, 1.5) * mm});
            skArc(sketch, "E88", {"start": v(14.47, 7.9) * mm, "mid": v(17.49, 10.88) * mm, "end": v(14.5, 13.88) * mm});
            skArc(sketch, "E89", {"start": v(6.7, 13.9) * mm, "mid": v(3.7, 10.9) * mm, "end": v(6.7, 7.9) * mm});
            skLineSegment(sketch, "E90", {"start": v(14.5, 13.88) * mm, "end": v(6.7, 13.9) * mm});
            skLineSegment(sketch, "E91", {"start": v(6.7, 7.9) * mm, "end": v(14.54, 7.9) * mm});
            skLineSegment(sketch, "E92", {"start": v(6, -5.57) * mm, "end": v(6, -16.85) * mm});
            skLineSegment(sketch, "E93", {"start": v(12.6, -16.85) * mm, "end": v(6, -16.85) * mm});
            skPoint(sketch, "E94.center.orphan", {"position": v(10.72, -16.85) * mm});
            skLineSegment(sketch, "E95", {"start": v(8.87, -5.06) * mm, "end": v(8.87, 1.5) * mm});
            skArc(sketch, "E96", {"start": v(12.22, 1.5) * mm, "mid": v(10.54, 3.17) * mm, "end": v(8.87, 1.5) * mm});
            skPoint(sketch, "E97.orphan", {"position": v(12.22, -16.85) * mm});
            skLineSegment(sketch, "E98", {"start": v(0, 0) * mm, "end": v(0, 19.9) * mm, "construction": true});
            skLineSegment(sketch, "E99", {"start": v(0, 19.9) * mm, "end": v(21, 19.9) * mm, "construction": true});
            skLineSegment(sketch, "E100", {"start": v(14.5, 10.9) * mm, "end": v(21, 10.9) * mm, "construction": true});
            skLineSegment(sketch, "E101", {"start": v(8.87, -5.06) * mm, "end": v(6, -5.06) * mm});
            skLineSegment(sketch, "E102", {"start": v(6, -5.06) * mm, "end": v(6, -5.57) * mm});
            skLineSegment(sketch, "E103", {"start": v(12.22, -5.06) * mm, "end": v(12.6, -5.06) * mm});
            skLineSegment(sketch, "E104", {"start": v(12.6, -16.85) * mm, "end": v(13.95, -16.85) * mm});
            skLineSegment(sketch, "E105", {"start": v(13.95, -16.85) * mm, "end": v(13.95, -5.06) * mm});
            skLineSegment(sketch, "E106", {"start": v(13.95, -5.06) * mm, "end": v(12.6, -5.06) * mm});
            skPoint(sketch, "E107.end.orphan", {"position": v(12.6, -5.57) * mm});
            skSolve(sketch);
        }
        {
            var Q0;
            Q0=qSketchRegion(id+"F23",true);
            extrude(context, id + "F24", {"entities" : qUnion([Q0]), "operationType" : NewBodyOperationType.REMOVE, "depth" : 25 * mm});
        }
        {
            var Q0;
            Q0=qCreatedBy(makeId("Top.planeOp"),FACE);
            var sketch = newSketch(context, id + "F25", { "sketchPlane" : qUnion([Q0])});
            skLineSegment(sketch, "E108", {"start": v(18.49, -17.16) * mm, "end": v(5.97, -17.16) * mm});
            skLineSegment(sketch, "E109", {"start": v(18.49, -16.86) * mm, "end": v(5.97, -16.86) * mm});
            skLineSegment(sketch, "E110", {"start": v(12.44, -31.08) * mm, "end": v(5.87, -31.08) * mm});
            skLineSegment(sketch, "E111", {"start": v(12.44, -30.78) * mm, "end": v(5.87, -30.78) * mm});
            skLineSegment(sketch, "E112.bottom", {"start": v(-33.84, 14.47) * mm, "end": v(-32.16, 14.47) * mm});
            skLineSegment(sketch, "E112.top", {"start": v(-33.84, 18.7) * mm, "end": v(-29.5, 18.7) * mm});
            skLineSegment(sketch, "E112.left", {"start": v(-33.84, 14.47) * mm, "end": v(-33.84, 18.7) * mm});
            skLineSegment(sketch, "E112.right", {"start": v(-29.5, 16.74) * mm, "end": v(-29.5, 18.7) * mm});
            skArc(sketch, "E113", {"start": v(-29.5, 16.74) * mm, "mid": v(-31.35, 16.22) * mm, "end": v(-32.16, 14.47) * mm});
            skLineSegment(sketch, "E114.bottom", {"start": v(-33.6, -31.08) * mm, "end": v(-33.6, -31.08) * mm});
            skLineSegment(sketch, "E114.top", {"start": v(-33.6, -34.81) * mm, "end": v(-31.03, -34.81) * mm});
            skLineSegment(sketch, "E114.left", {"start": v(-33.6, -31.08) * mm, "end": v(-33.6, -34.81) * mm});
            skLineSegment(sketch, "E114.right", {"start": v(-31.03, -31.08) * mm, "end": v(-31.03, -33.21) * mm});
            skLineSegment(sketch, "E115.bottom", {"start": v(-31.03, -34.81) * mm, "end": v(-28.95, -34.81) * mm});
            skLineSegment(sketch, "E115.top", {"start": v(-31.03, -33.21) * mm, "end": v(-28.95, -33.21) * mm});
            skLineSegment(sketch, "E115.right", {"start": v(-28.95, -34.81) * mm, "end": v(-28.95, -33.21) * mm});
            skPoint(sketch, "E116.end.orphan", {"position": v(-34.98, -31.08) * mm});
            skPoint(sketch, "E116.start.orphan", {"position": v(-34.98, -30.78) * mm});
            skLineSegment(sketch, "E117.bottom", {"start": v(16.87, -34.88) * mm, "end": v(19.69, -34.88) * mm});
            skLineSegment(sketch, "E117.top", {"start": v(16.87, -30.79) * mm, "end": v(19.69, -30.79) * mm});
            skLineSegment(sketch, "E117.left", {"start": v(16.87, -33.4) * mm, "end": v(16.87, -30.79) * mm});
            skLineSegment(sketch, "E117.right", {"start": v(19.69, -34.88) * mm, "end": v(19.69, -30.79) * mm});
            skLineSegment(sketch, "E118.bottom", {"start": v(16.87, -34.88) * mm, "end": v(14.73, -34.88) * mm});
            skLineSegment(sketch, "E118.top", {"start": v(16.87, -33.4) * mm, "end": v(14.73, -33.4) * mm});
            skLineSegment(sketch, "E118.right", {"start": v(14.73, -34.88) * mm, "end": v(14.73, -33.4) * mm});
            skLineSegment(sketch, "E119.top", {"start": v(-31.03, -30.09) * mm, "end": v(-33.6, -30.09) * mm});
            skLineSegment(sketch, "E119.left", {"start": v(-31.03, -31.08) * mm, "end": v(-31.03, -30.09) * mm});
            skLineSegment(sketch, "E119.right", {"start": v(-33.6, -31.08) * mm, "end": v(-33.6, -30.09) * mm});
            skLineSegment(sketch, "E120", {"start": v(5.87, -31.08) * mm, "end": v(5.87, -30.78) * mm});
            skPoint(sketch, "E121.end.orphan", {"position": v(-34.98, -17.16) * mm});
            skPoint(sketch, "E121.start.orphan", {"position": v(-34.98, -16.86) * mm});
            skLineSegment(sketch, "E122.trimOffspring", {"start": v(5.97, -17.16) * mm, "end": v(5.97, -16.86) * mm});
            skLineSegment(sketch, "E123.bottom", {"start": v(5.85, -23.4) * mm, "end": v(18.49, -23.4) * mm});
            skLineSegment(sketch, "E123.top", {"start": v(5.85, -23.7) * mm, "end": v(18.49, -23.7) * mm});
            skLineSegment(sketch, "E123.left", {"start": v(5.85, -23.4) * mm, "end": v(5.85, -23.7) * mm});
            skLineSegment(sketch, "E124", {"start": v(5.29, -31.08) * mm, "end": v(5.29, 2.03) * mm});
            skLineSegment(sketch, "E125", {"start": v(4.99, -31.08) * mm, "end": v(5.29, -31.08) * mm});
            skLineSegment(sketch, "E126", {"start": v(12.44, -30.78) * mm, "end": v(12.44, -31.08) * mm});
            skLineSegment(sketch, "E127", {"start": v(18.49, -16.86) * mm, "end": v(18.49, -17.16) * mm});
            skPoint(sketch, "E128.orphan", {"position": v(19.24, -17.16) * mm});
            skLineSegment(sketch, "E129.trimOffspring", {"start": v(18.49, -23.4) * mm, "end": v(18.49, -23.7) * mm});
            skPoint(sketch, "E130.orphan", {"position": v(19.24, -23.7) * mm});
            skLineSegment(sketch, "E131.trimOffspring", {"start": v(4.99, 2.03) * mm, "end": v(4.99, -31.08) * mm});
            skLineSegment(sketch, "E132", {"start": v(4.99, 2.03) * mm, "end": v(5.29, 2.03) * mm});
            skLineSegment(sketch, "E133.bottom", {"start": v(4.99, 2.73) * mm, "end": v(13.12, 2.73) * mm});
            skLineSegment(sketch, "E133.top", {"start": v(4.99, 6.24) * mm, "end": v(13.12, 6.24) * mm});
            skLineSegment(sketch, "E133.left", {"start": v(4.99, 2.73) * mm, "end": v(4.99, 6.24) * mm});
            skLineSegment(sketch, "E133.right", {"start": v(13.12, 2.73) * mm, "end": v(13.12, 6.24) * mm});
            skCircle(sketch, "E134", {"center": v(8.91, 3.9) * mm, "radius": 1.04 * mm});
            skPoint(sketch, "E134.first.point", {"position": v(8.9, 2.86) * mm});
            skPoint(sketch, "E134.second.point", {"position": v(8.95, 4.94) * mm});
            skPoint(sketch, "E134.third.point", {"position": v(9.95, 3.84) * mm});
            skSolve(sketch);
        }
        {
            var Q0;
            Q0=qSketchRegion(id+"F25",true);
            var Q1;
            Q1=makeQuery(id+"F6.opShell","OFFSET_FACE",FACE,{"disambiguationData":[OSD([sQuery(id+"F2.wireOp",EDGE,"E20"),sQuery(id+"F2.wireOp",EDGE,"E22")])]});
            extrude(context, id + "F26", {"entities" : qUnion([Q0]), "operationType" : NewBodyOperationType.ADD, "endBoundEntityFace" : qUnion([Q1]), "depth" : 7.5 * mm});
        }
        {
            var Q0;
            Q0=qCreatedBy(makeId("Top.planeOp"),FACE);
            var sketch = newSketch(context, id + "F27", { "sketchPlane" : qUnion([Q0])});
            skLineSegment(sketch, "E135", {"start": v(-14.06, 0.58) * mm, "end": v(-9.7, 0.57) * mm});
            skLineSegment(sketch, "E136", {"start": v(-8.04, -3.57) * mm, "end": v(-8.03, -3.84) * mm});
            skLineSegment(sketch, "E137", {"start": v(-8.03, -3.84) * mm, "end": v(-8.04, -13.15) * mm});
            skLineSegment(sketch, "E138", {"start": v(-8.04, -13.15) * mm, "end": v(-8.03, -13.22) * mm});
            skLineSegment(sketch, "E139", {"start": v(-8.03, -13.22) * mm, "end": v(-8.03, -13.28) * mm});
            skLineSegment(sketch, "E140", {"start": v(-8.03, -13.28) * mm, "end": v(-8.04, -13.35) * mm});
            skLineSegment(sketch, "E141", {"start": v(-8.04, -13.35) * mm, "end": v(-8.04, -13.42) * mm});
            skLineSegment(sketch, "E142", {"start": v(-8.04, -13.42) * mm, "end": v(-8.05, -13.48) * mm});
            skLineSegment(sketch, "E143", {"start": v(-8.05, -13.48) * mm, "end": v(-8.06, -13.55) * mm});
            skLineSegment(sketch, "E144", {"start": v(-8.06, -13.55) * mm, "end": v(-8.07, -13.61) * mm});
            skLineSegment(sketch, "E145", {"start": v(-8.07, -13.61) * mm, "end": v(-8.1, -13.68) * mm});
            skLineSegment(sketch, "E146", {"start": v(-8.1, -13.68) * mm, "end": v(-8.1, -13.74) * mm});
            skLineSegment(sketch, "E147", {"start": v(-8.1, -13.74) * mm, "end": v(-8.13, -13.8) * mm});
            skLineSegment(sketch, "E148", {"start": v(-8.13, -13.8) * mm, "end": v(-8.15, -13.86) * mm});
            skLineSegment(sketch, "E149", {"start": v(-8.15, -13.86) * mm, "end": v(-8.18, -13.93) * mm});
            skLineSegment(sketch, "E150", {"start": v(-8.18, -13.93) * mm, "end": v(-8.2, -13.99) * mm});
            skLineSegment(sketch, "E151", {"start": v(-8.2, -13.99) * mm, "end": v(-8.23, -14.05) * mm});
            skLineSegment(sketch, "E152", {"start": v(-8.23, -14.05) * mm, "end": v(-8.26, -14.1) * mm});
            skLineSegment(sketch, "E153", {"start": v(-8.26, -14.1) * mm, "end": v(-8.3, -14.16) * mm});
            skLineSegment(sketch, "E154", {"start": v(-8.3, -14.16) * mm, "end": v(-8.33, -14.22) * mm});
            skLineSegment(sketch, "E155", {"start": v(-8.33, -14.22) * mm, "end": v(-8.37, -14.27) * mm});
            skLineSegment(sketch, "E156", {"start": v(-8.37, -14.27) * mm, "end": v(-8.4, -14.32) * mm});
            skLineSegment(sketch, "E157", {"start": v(-8.4, -14.32) * mm, "end": v(-8.45, -14.37) * mm});
            skLineSegment(sketch, "E158", {"start": v(-8.45, -14.37) * mm, "end": v(-8.5, -14.42) * mm});
            skLineSegment(sketch, "E159", {"start": v(-8.5, -14.42) * mm, "end": v(-8.54, -14.47) * mm});
            skLineSegment(sketch, "E160", {"start": v(-8.54, -14.47) * mm, "end": v(-8.59, -14.52) * mm});
            skLineSegment(sketch, "E161", {"start": v(-8.59, -14.52) * mm, "end": v(-8.63, -14.56) * mm});
            skLineSegment(sketch, "E162", {"start": v(-8.63, -14.56) * mm, "end": v(-8.69, -14.6) * mm});
            skLineSegment(sketch, "E163", {"start": v(-8.69, -14.6) * mm, "end": v(-8.74, -14.64) * mm});
            skLineSegment(sketch, "E164", {"start": v(-8.74, -14.64) * mm, "end": v(-8.8, -14.68) * mm});
            skLineSegment(sketch, "E165", {"start": v(-8.8, -14.68) * mm, "end": v(-8.85, -14.72) * mm});
            skLineSegment(sketch, "E166", {"start": v(-8.85, -14.72) * mm, "end": v(-8.9, -14.75) * mm});
            skLineSegment(sketch, "E167", {"start": v(-8.9, -14.75) * mm, "end": v(-8.95, -14.77) * mm});
            skLineSegment(sketch, "E168", {"start": v(-8.95, -14.77) * mm, "end": v(-8.99, -14.8) * mm});
            skLineSegment(sketch, "E169", {"start": v(-8.99, -14.8) * mm, "end": v(-9.03, -14.81) * mm});
            skLineSegment(sketch, "E170", {"start": v(-9.03, -14.81) * mm, "end": v(-9.07, -14.83) * mm});
            skLineSegment(sketch, "E171", {"start": v(-9.07, -14.83) * mm, "end": v(-9.11, -14.85) * mm});
            skLineSegment(sketch, "E172", {"start": v(-9.11, -14.85) * mm, "end": v(-9.16, -14.86) * mm});
            skLineSegment(sketch, "E173", {"start": v(-9.16, -14.86) * mm, "end": v(-9.2, -14.88) * mm});
            skLineSegment(sketch, "E174", {"start": v(-9.2, -14.88) * mm, "end": v(-9.24, -14.9) * mm});
            skLineSegment(sketch, "E175", {"start": v(-9.24, -14.9) * mm, "end": v(-9.29, -14.9) * mm});
            skLineSegment(sketch, "E176", {"start": v(-9.29, -14.9) * mm, "end": v(-9.33, -14.91) * mm});
            skLineSegment(sketch, "E177", {"start": v(-9.33, -14.91) * mm, "end": v(-9.38, -14.92) * mm});
            skLineSegment(sketch, "E178", {"start": v(-9.38, -14.92) * mm, "end": v(-9.42, -14.93) * mm});
            skLineSegment(sketch, "E179", {"start": v(-9.42, -14.93) * mm, "end": v(-9.51, -14.94) * mm});
            skLineSegment(sketch, "E180", {"start": v(-9.51, -14.94) * mm, "end": v(-9.6, -14.96) * mm});
            skLineSegment(sketch, "E181", {"start": v(-9.6, -14.96) * mm, "end": v(-9.74, -14.97) * mm});
            skLineSegment(sketch, "E182", {"start": v(-9.74, -14.97) * mm, "end": v(-10.2, -14.98) * mm});
            skLineSegment(sketch, "E183", {"start": v(-10.2, -14.98) * mm, "end": v(-23.2, -14.97) * mm});
            skLineSegment(sketch, "E184", {"start": v(-23.2, -14.97) * mm, "end": v(-23.28, -14.97) * mm});
            skLineSegment(sketch, "E185", {"start": v(-23.28, -14.97) * mm, "end": v(-23.35, -14.97) * mm});
            skLineSegment(sketch, "E186", {"start": v(-23.35, -14.97) * mm, "end": v(-23.43, -14.97) * mm});
            skLineSegment(sketch, "E187", {"start": v(-23.43, -14.97) * mm, "end": v(-23.5, -14.96) * mm});
            skLineSegment(sketch, "E188", {"start": v(-23.5, -14.96) * mm, "end": v(-23.58, -14.94) * mm});
            skLineSegment(sketch, "E189", {"start": v(-23.58, -14.94) * mm, "end": v(-23.65, -14.93) * mm});
            skLineSegment(sketch, "E190", {"start": v(-23.65, -14.93) * mm, "end": v(-23.72, -14.9) * mm});
            skLineSegment(sketch, "E191", {"start": v(-23.72, -14.9) * mm, "end": v(-23.8, -14.89) * mm});
            skLineSegment(sketch, "E192", {"start": v(-23.8, -14.89) * mm, "end": v(-23.86, -14.86) * mm});
            skLineSegment(sketch, "E193", {"start": v(-23.86, -14.86) * mm, "end": v(-23.93, -14.83) * mm});
            skLineSegment(sketch, "E194", {"start": v(-23.93, -14.83) * mm, "end": v(-24, -14.8) * mm});
            skLineSegment(sketch, "E195", {"start": v(-24, -14.8) * mm, "end": v(-24.07, -14.77) * mm});
            skLineSegment(sketch, "E196", {"start": v(-24.07, -14.77) * mm, "end": v(-24.13, -14.73) * mm});
            skLineSegment(sketch, "E197", {"start": v(-24.13, -14.73) * mm, "end": v(-24.2, -14.7) * mm});
            skLineSegment(sketch, "E198", {"start": v(-24.2, -14.7) * mm, "end": v(-24.26, -14.65) * mm});
            skLineSegment(sketch, "E199", {"start": v(-24.26, -14.65) * mm, "end": v(-24.32, -14.6) * mm});
            skLineSegment(sketch, "E200", {"start": v(-24.32, -14.6) * mm, "end": v(-24.38, -14.56) * mm});
            skLineSegment(sketch, "E201", {"start": v(-24.38, -14.56) * mm, "end": v(-24.43, -14.51) * mm});
            skLineSegment(sketch, "E202", {"start": v(-24.43, -14.51) * mm, "end": v(-24.48, -14.46) * mm});
            skLineSegment(sketch, "E203", {"start": v(-24.48, -14.46) * mm, "end": v(-24.54, -14.4) * mm});
            skLineSegment(sketch, "E204", {"start": v(-24.54, -14.4) * mm, "end": v(-24.59, -14.35) * mm});
            skLineSegment(sketch, "E205", {"start": v(-24.59, -14.35) * mm, "end": v(-24.63, -14.3) * mm});
            skLineSegment(sketch, "E206", {"start": v(-24.63, -14.3) * mm, "end": v(-24.68, -14.23) * mm});
            skLineSegment(sketch, "E207", {"start": v(-24.68, -14.23) * mm, "end": v(-24.72, -14.17) * mm});
            skLineSegment(sketch, "E208", {"start": v(-24.72, -14.17) * mm, "end": v(-24.76, -14.1) * mm});
            skLineSegment(sketch, "E209", {"start": v(-24.76, -14.1) * mm, "end": v(-24.8, -14.04) * mm});
            skLineSegment(sketch, "E210", {"start": v(-24.8, -14.04) * mm, "end": v(-24.82, -13.97) * mm});
            skLineSegment(sketch, "E211", {"start": v(-24.82, -13.97) * mm, "end": v(-24.85, -13.9) * mm});
            skLineSegment(sketch, "E212", {"start": v(-24.85, -13.9) * mm, "end": v(-24.88, -13.83) * mm});
            skLineSegment(sketch, "E213", {"start": v(-24.88, -13.83) * mm, "end": v(-24.9, -13.76) * mm});
            skLineSegment(sketch, "E214", {"start": v(-24.9, -13.76) * mm, "end": v(-24.92, -13.66) * mm});
            skLineSegment(sketch, "E215", {"start": v(-24.92, -13.66) * mm, "end": v(-24.94, -13.55) * mm});
            skLineSegment(sketch, "E216", {"start": v(-24.94, -13.55) * mm, "end": v(-24.96, -13.38) * mm});
            skLineSegment(sketch, "E217", {"start": v(-24.96, -13.38) * mm, "end": v(-24.98, -12.8) * mm});
            skLineSegment(sketch, "E218", {"start": v(-24.98, -12.8) * mm, "end": v(-24.98, -3.92) * mm});
            skLineSegment(sketch, "E219", {"start": v(-24.98, -3.92) * mm, "end": v(-24.97, -3.38) * mm});
            skLineSegment(sketch, "E220", {"start": v(-24.97, -3.38) * mm, "end": v(-24.96, -3.24) * mm});
            skLineSegment(sketch, "E221", {"start": v(-24.96, -3.24) * mm, "end": v(-24.95, -3.15) * mm});
            skLineSegment(sketch, "E222", {"start": v(-24.95, -3.15) * mm, "end": v(-24.94, -3.1) * mm});
            skLineSegment(sketch, "E223", {"start": v(-24.94, -3.1) * mm, "end": v(-24.93, -3.06) * mm});
            skLineSegment(sketch, "E224", {"start": v(-24.93, -3.06) * mm, "end": v(-24.93, -3.02) * mm});
            skLineSegment(sketch, "E225", {"start": v(-24.93, -3.02) * mm, "end": v(-24.92, -2.97) * mm});
            skLineSegment(sketch, "E226", {"start": v(-24.92, -2.97) * mm, "end": v(-24.9, -2.93) * mm});
            skLineSegment(sketch, "E227", {"start": v(-24.9, -2.93) * mm, "end": v(-24.9, -2.88) * mm});
            skLineSegment(sketch, "E228", {"start": v(-24.9, -2.88) * mm, "end": v(-24.88, -2.84) * mm});
            skLineSegment(sketch, "E229", {"start": v(-24.88, -2.84) * mm, "end": v(-24.87, -2.8) * mm});
            skLineSegment(sketch, "E230", {"start": v(-24.87, -2.8) * mm, "end": v(-24.85, -2.76) * mm});
            skLineSegment(sketch, "E231", {"start": v(-24.85, -2.76) * mm, "end": v(-24.83, -2.71) * mm});
            skLineSegment(sketch, "E232", {"start": v(-24.83, -2.71) * mm, "end": v(-24.81, -2.67) * mm});
            skLineSegment(sketch, "E233", {"start": v(-24.81, -2.67) * mm, "end": v(-24.8, -2.63) * mm});
            skLineSegment(sketch, "E234", {"start": v(-24.8, -2.63) * mm, "end": v(-24.77, -2.58) * mm});
            skLineSegment(sketch, "E235", {"start": v(-24.77, -2.58) * mm, "end": v(-24.74, -2.53) * mm});
            skLineSegment(sketch, "E236", {"start": v(-24.74, -2.53) * mm, "end": v(-24.7, -2.48) * mm});
            skLineSegment(sketch, "E237", {"start": v(-24.7, -2.48) * mm, "end": v(-24.68, -2.43) * mm});
            skLineSegment(sketch, "E238", {"start": v(-24.68, -2.43) * mm, "end": v(-24.64, -2.38) * mm});
            skLineSegment(sketch, "E239", {"start": v(-24.64, -2.38) * mm, "end": v(-24.6, -2.34) * mm});
            skLineSegment(sketch, "E240", {"start": v(-24.6, -2.34) * mm, "end": v(-24.57, -2.3) * mm});
            skLineSegment(sketch, "E241", {"start": v(-24.57, -2.3) * mm, "end": v(-24.53, -2.25) * mm});
            skLineSegment(sketch, "E242", {"start": v(-24.53, -2.25) * mm, "end": v(-24.5, -2.2) * mm});
            skLineSegment(sketch, "E243", {"start": v(-24.5, -2.2) * mm, "end": v(-24.45, -2.16) * mm});
            skLineSegment(sketch, "E244", {"start": v(-24.45, -2.16) * mm, "end": v(-24.41, -2.12) * mm});
            skLineSegment(sketch, "E245", {"start": v(-24.41, -2.12) * mm, "end": v(-24.37, -2.08) * mm});
            skLineSegment(sketch, "E246", {"start": v(-24.37, -2.08) * mm, "end": v(-24.32, -2.05) * mm});
            skLineSegment(sketch, "E247", {"start": v(-24.32, -2.05) * mm, "end": v(-24.28, -2.01) * mm});
            skLineSegment(sketch, "E248", {"start": v(-24.28, -2.01) * mm, "end": v(-24.23, -1.98) * mm});
            skLineSegment(sketch, "E249", {"start": v(-24.23, -1.98) * mm, "end": v(-24.18, -1.94) * mm});
            skLineSegment(sketch, "E250", {"start": v(-24.18, -1.94) * mm, "end": v(-24.13, -1.91) * mm});
            skLineSegment(sketch, "E251", {"start": v(-24.13, -1.91) * mm, "end": v(-24.08, -1.88) * mm});
            skLineSegment(sketch, "E252", {"start": v(-24.08, -1.88) * mm, "end": v(-24.03, -1.86) * mm});
            skLineSegment(sketch, "E253", {"start": v(-24.03, -1.86) * mm, "end": v(-23.98, -1.83) * mm});
            skLineSegment(sketch, "E254", {"start": v(-23.98, -1.83) * mm, "end": v(-23.93, -1.8) * mm});
            skLineSegment(sketch, "E255", {"start": v(-23.93, -1.8) * mm, "end": v(-23.87, -1.79) * mm});
            skLineSegment(sketch, "E256", {"start": v(-23.87, -1.79) * mm, "end": v(-23.82, -1.77) * mm});
            skLineSegment(sketch, "E257", {"start": v(-23.82, -1.77) * mm, "end": v(-23.76, -1.75) * mm});
            skLineSegment(sketch, "E258", {"start": v(-23.76, -1.75) * mm, "end": v(-23.7, -1.73) * mm});
            skLineSegment(sketch, "E259", {"start": v(-23.7, -1.73) * mm, "end": v(-23.65, -1.72) * mm});
            skLineSegment(sketch, "E260", {"start": v(-23.65, -1.72) * mm, "end": v(-23.6, -1.71) * mm});
            skLineSegment(sketch, "E261", {"start": v(-23.6, -1.71) * mm, "end": v(-23.53, -1.7) * mm});
            skLineSegment(sketch, "E262", {"start": v(-23.53, -1.7) * mm, "end": v(-23.48, -1.7) * mm});
            skLineSegment(sketch, "E263", {"start": v(-23.48, -1.7) * mm, "end": v(-23.32, -1.69) * mm});
            skLineSegment(sketch, "E264", {"start": v(-23.32, -1.69) * mm, "end": v(-23.17, -1.68) * mm});
            skLineSegment(sketch, "E265", {"start": v(-23.17, -1.68) * mm, "end": v(-22.95, -1.67) * mm});
            skLineSegment(sketch, "E266", {"start": v(-22.95, -1.67) * mm, "end": v(-21.9, -1.67) * mm});
            skLineSegment(sketch, "E267", {"start": v(-21.9, -1.67) * mm, "end": v(-21.52, -1.67) * mm});
            skLineSegment(sketch, "E268", {"start": v(-21.52, -1.67) * mm, "end": v(-21.3, -1.66) * mm});
            skLineSegment(sketch, "E269", {"start": v(-21.3, -1.66) * mm, "end": v(-21.2, -1.64) * mm});
            skLineSegment(sketch, "E270", {"start": v(-21.2, -1.64) * mm, "end": v(-20.86, -1.5) * mm});
            skLineSegment(sketch, "E271", {"start": v(-20.86, -1.5) * mm, "end": v(-17.7, 0.02) * mm});
            skLineSegment(sketch, "E272", {"start": v(-17.7, 0.02) * mm, "end": v(-17.01, 0.36) * mm});
            skLineSegment(sketch, "E273", {"start": v(-15.75, 0.24) * mm, "end": v(-14.06, -0.59) * mm});
            skLineSegment(sketch, "E274", {"start": v(-14.06, -0.59) * mm, "end": v(-14.06, 0.58) * mm});
            skLineSegment(sketch, "E275", {"start": v(-13.15, -0.33) * mm, "end": v(-13.15, -2.1) * mm});
            skLineSegment(sketch, "E276", {"start": v(-13.15, -2.1) * mm, "end": v(-13.26, -2.06) * mm});
            skLineSegment(sketch, "E277", {"start": v(-13.26, -2.06) * mm, "end": v(-13.9, -1.75) * mm});
            skLineSegment(sketch, "E278", {"start": v(-16.83, -0.6) * mm, "end": v(-17.05, -0.71) * mm});
            skLineSegment(sketch, "E279", {"start": v(-17.05, -0.71) * mm, "end": v(-17.27, -0.83) * mm});
            skLineSegment(sketch, "E280", {"start": v(-17.27, -0.83) * mm, "end": v(-18.4, -1.4) * mm});
            skLineSegment(sketch, "E281", {"start": v(-18.4, -1.4) * mm, "end": v(-22.7, -3.51) * mm});
            skLineSegment(sketch, "E282", {"start": v(-22.7, -3.51) * mm, "end": v(-23.6, -3.97) * mm});
            skLineSegment(sketch, "E283", {"start": v(-23.6, -3.97) * mm, "end": v(-23.64, -4) * mm});
            skLineSegment(sketch, "E284", {"start": v(-23.64, -4) * mm, "end": v(-23.69, -4.02) * mm});
            skLineSegment(sketch, "E285", {"start": v(-23.69, -4.02) * mm, "end": v(-23.73, -4.05) * mm});
            skLineSegment(sketch, "E286", {"start": v(-23.73, -4.05) * mm, "end": v(-23.76, -4.08) * mm});
            skLineSegment(sketch, "E287", {"start": v(-23.76, -4.08) * mm, "end": v(-23.79, -4.1) * mm});
            skLineSegment(sketch, "E288", {"start": v(-23.79, -4.1) * mm, "end": v(-23.8, -4.13) * mm});
            skLineSegment(sketch, "E289", {"start": v(-23.8, -4.13) * mm, "end": v(-23.82, -4.15) * mm});
            skLineSegment(sketch, "E290", {"start": v(-23.82, -4.15) * mm, "end": v(-23.83, -4.16) * mm});
            skLineSegment(sketch, "E291", {"start": v(-23.83, -4.16) * mm, "end": v(-23.83, -4.18) * mm});
            skLineSegment(sketch, "E292", {"start": v(-23.83, -4.18) * mm, "end": v(-23.84, -4.2) * mm});
            skLineSegment(sketch, "E293", {"start": v(-23.84, -4.2) * mm, "end": v(-23.85, -4.21) * mm});
            skLineSegment(sketch, "E294", {"start": v(-23.85, -4.21) * mm, "end": v(-23.85, -4.23) * mm});
            skLineSegment(sketch, "E295", {"start": v(-23.85, -4.23) * mm, "end": v(-23.85, -4.25) * mm});
            skLineSegment(sketch, "E296", {"start": v(-23.85, -4.25) * mm, "end": v(-23.86, -4.27) * mm});
            skLineSegment(sketch, "E297", {"start": v(-23.86, -4.27) * mm, "end": v(-23.86, -4.29) * mm});
            skLineSegment(sketch, "E298", {"start": v(-23.86, -4.29) * mm, "end": v(-23.86, -4.3) * mm});
            skLineSegment(sketch, "E299", {"start": v(-23.86, -4.3) * mm, "end": v(-23.85, -4.32) * mm});
            skLineSegment(sketch, "E300", {"start": v(-23.85, -4.32) * mm, "end": v(-23.85, -4.34) * mm});
            skLineSegment(sketch, "E301", {"start": v(-23.85, -4.34) * mm, "end": v(-23.84, -4.36) * mm});
            skLineSegment(sketch, "E302", {"start": v(-23.84, -4.36) * mm, "end": v(-23.84, -4.38) * mm});
            skLineSegment(sketch, "E303", {"start": v(-23.84, -4.38) * mm, "end": v(-23.83, -4.4) * mm});
            skLineSegment(sketch, "E304", {"start": v(-23.83, -4.4) * mm, "end": v(-23.82, -4.42) * mm});
            skLineSegment(sketch, "E305", {"start": v(-23.82, -4.42) * mm, "end": v(-23.81, -4.44) * mm});
            skLineSegment(sketch, "E306", {"start": v(-23.81, -4.44) * mm, "end": v(-23.8, -4.45) * mm});
            skLineSegment(sketch, "E307", {"start": v(-23.8, -4.45) * mm, "end": v(-23.8, -4.47) * mm});
            skLineSegment(sketch, "E308", {"start": v(-23.8, -4.47) * mm, "end": v(-23.78, -4.48) * mm});
            skLineSegment(sketch, "E309", {"start": v(-23.78, -4.48) * mm, "end": v(-23.76, -4.5) * mm});
            skLineSegment(sketch, "E310", {"start": v(-23.76, -4.5) * mm, "end": v(-23.73, -4.53) * mm});
            skLineSegment(sketch, "E311", {"start": v(-23.73, -4.53) * mm, "end": v(-23.7, -4.55) * mm});
            skLineSegment(sketch, "E312", {"start": v(-23.7, -4.55) * mm, "end": v(-23.58, -4.62) * mm});
            skLineSegment(sketch, "E313", {"start": v(-23.58, -4.62) * mm, "end": v(-23.42, -4.7) * mm});
            skLineSegment(sketch, "E314", {"start": v(-23.42, -4.7) * mm, "end": v(-19.6, -6.6) * mm});
            skLineSegment(sketch, "E315", {"start": v(-19.6, -6.6) * mm, "end": v(-18.6, -7.09) * mm});
            skLineSegment(sketch, "E316", {"start": v(-18.6, -7.09) * mm, "end": v(-17.5, -7.65) * mm});
            skLineSegment(sketch, "E317", {"start": v(-17.5, -7.65) * mm, "end": v(-16.7, -8.03) * mm});
            skLineSegment(sketch, "E318", {"start": v(-16.7, -8.03) * mm, "end": v(-16.68, -8.04) * mm});
            skLineSegment(sketch, "E319", {"start": v(-16.68, -8.04) * mm, "end": v(-16.66, -8.05) * mm});
            skLineSegment(sketch, "E320", {"start": v(-16.66, -8.05) * mm, "end": v(-16.64, -8.06) * mm});
            skLineSegment(sketch, "E321", {"start": v(-16.64, -8.06) * mm, "end": v(-16.62, -8.06) * mm});
            skLineSegment(sketch, "E322", {"start": v(-16.62, -8.06) * mm, "end": v(-16.6, -8.07) * mm});
            skLineSegment(sketch, "E323", {"start": v(-16.6, -8.07) * mm, "end": v(-16.58, -8.07) * mm});
            skLineSegment(sketch, "E324", {"start": v(-16.58, -8.07) * mm, "end": v(-16.56, -8.07) * mm});
            skLineSegment(sketch, "E325", {"start": v(-16.56, -8.07) * mm, "end": v(-16.54, -8.07) * mm});
            skLineSegment(sketch, "E326", {"start": v(-16.54, -8.07) * mm, "end": v(-16.52, -8.08) * mm});
            skLineSegment(sketch, "E327", {"start": v(-16.52, -8.08) * mm, "end": v(-16.48, -8.07) * mm});
            skLineSegment(sketch, "E328", {"start": v(-16.48, -8.07) * mm, "end": v(-16.44, -8.07) * mm});
            skLineSegment(sketch, "E329", {"start": v(-16.44, -8.07) * mm, "end": v(-16.4, -8.06) * mm});
            skLineSegment(sketch, "E330", {"start": v(-16.4, -8.06) * mm, "end": v(-16.32, -8.04) * mm});
            skLineSegment(sketch, "E331", {"start": v(-16.32, -8.04) * mm, "end": v(-16.14, -7.96) * mm});
            skLineSegment(sketch, "E332", {"start": v(-16.14, -7.96) * mm, "end": v(-13.76, -6.78) * mm});
            skLineSegment(sketch, "E333", {"start": v(-13.76, -6.78) * mm, "end": v(-9.85, -4.84) * mm});
            skLineSegment(sketch, "E334", {"start": v(-9.4, -3.99) * mm, "end": v(-9.57, -3.89) * mm});
            skLineSegment(sketch, "E335", {"start": v(-9.57, -3.89) * mm, "end": v(-10.59, -3.4) * mm});
            skLineSegment(sketch, "E336", {"start": v(-10.59, -3.4) * mm, "end": v(-10.6, -0.33) * mm});
            skLineSegment(sketch, "E337", {"start": v(-10.6, -0.33) * mm, "end": v(-13.15, -0.33) * mm});
            skLineSegment(sketch, "E338", {"start": v(-26.34, -4.98) * mm, "end": v(-25.3, -4.97) * mm});
            skLineSegment(sketch, "E339", {"start": v(-25.3, -4.97) * mm, "end": v(-25.28, -6.53) * mm});
            skLineSegment(sketch, "E340", {"start": v(-25.28, -6.53) * mm, "end": v(-26.11, -6.52) * mm});
            skLineSegment(sketch, "E341", {"start": v(-26.11, -6.52) * mm, "end": v(-26.27, -6.5) * mm});
            skLineSegment(sketch, "E342", {"start": v(-26.27, -6.5) * mm, "end": v(-26.38, -6.49) * mm});
            skLineSegment(sketch, "E343", {"start": v(-26.38, -6.49) * mm, "end": v(-26.4, -6.47) * mm});
            skLineSegment(sketch, "E344", {"start": v(-26.4, -6.47) * mm, "end": v(-26.43, -6.45) * mm});
            skLineSegment(sketch, "E345", {"start": v(-26.43, -6.45) * mm, "end": v(-26.45, -6.43) * mm});
            skLineSegment(sketch, "E346", {"start": v(-26.45, -6.43) * mm, "end": v(-26.47, -6.41) * mm});
            skLineSegment(sketch, "E347", {"start": v(-26.47, -6.41) * mm, "end": v(-26.49, -6.39) * mm});
            skLineSegment(sketch, "E348", {"start": v(-26.49, -6.39) * mm, "end": v(-26.5, -6.37) * mm});
            skLineSegment(sketch, "E349", {"start": v(-26.5, -6.37) * mm, "end": v(-26.52, -6.34) * mm});
            skLineSegment(sketch, "E350", {"start": v(-26.52, -6.34) * mm, "end": v(-26.54, -6.32) * mm});
            skLineSegment(sketch, "E351", {"start": v(-26.54, -6.32) * mm, "end": v(-26.55, -6.29) * mm});
            skLineSegment(sketch, "E352", {"start": v(-26.55, -6.29) * mm, "end": v(-26.56, -6.26) * mm});
            skLineSegment(sketch, "E353", {"start": v(-26.56, -6.26) * mm, "end": v(-26.57, -6.23) * mm});
            skLineSegment(sketch, "E354", {"start": v(-26.57, -6.23) * mm, "end": v(-26.58, -6.2) * mm});
            skLineSegment(sketch, "E355", {"start": v(-26.58, -6.2) * mm, "end": v(-26.59, -6.18) * mm});
            skLineSegment(sketch, "E356", {"start": v(-26.59, -6.18) * mm, "end": v(-26.6, -6.15) * mm});
            skLineSegment(sketch, "E357", {"start": v(-26.6, -6.15) * mm, "end": v(-26.6, -6.09) * mm});
            skLineSegment(sketch, "E358", {"start": v(-26.6, -6.09) * mm, "end": v(-26.62, -6.03) * mm});
            skLineSegment(sketch, "E359", {"start": v(-26.62, -6.03) * mm, "end": v(-26.62, -5.9) * mm});
            skLineSegment(sketch, "E360", {"start": v(-26.62, -5.9) * mm, "end": v(-26.63, -5.75) * mm});
            skLineSegment(sketch, "E361", {"start": v(-26.63, -5.75) * mm, "end": v(-26.63, -5.7) * mm});
            skLineSegment(sketch, "E362", {"start": v(-26.63, -5.7) * mm, "end": v(-26.63, -5.62) * mm});
            skLineSegment(sketch, "E363", {"start": v(-26.63, -5.62) * mm, "end": v(-26.62, -5.5) * mm});
            skLineSegment(sketch, "E364", {"start": v(-26.62, -5.5) * mm, "end": v(-26.6, -5.42) * mm});
            skLineSegment(sketch, "E365", {"start": v(-26.6, -5.42) * mm, "end": v(-26.6, -5.36) * mm});
            skLineSegment(sketch, "E366", {"start": v(-26.6, -5.36) * mm, "end": v(-26.58, -5.3) * mm});
            skLineSegment(sketch, "E367", {"start": v(-26.58, -5.3) * mm, "end": v(-26.58, -5.28) * mm});
            skLineSegment(sketch, "E368", {"start": v(-26.58, -5.28) * mm, "end": v(-26.57, -5.25) * mm});
            skLineSegment(sketch, "E369", {"start": v(-26.57, -5.25) * mm, "end": v(-26.56, -5.23) * mm});
            skLineSegment(sketch, "E370", {"start": v(-26.56, -5.23) * mm, "end": v(-26.55, -5.2) * mm});
            skLineSegment(sketch, "E371", {"start": v(-26.55, -5.2) * mm, "end": v(-26.53, -5.18) * mm});
            skLineSegment(sketch, "E372", {"start": v(-26.53, -5.18) * mm, "end": v(-26.52, -5.15) * mm});
            skLineSegment(sketch, "E373", {"start": v(-26.52, -5.15) * mm, "end": v(-26.5, -5.13) * mm});
            skLineSegment(sketch, "E374", {"start": v(-26.5, -5.13) * mm, "end": v(-26.5, -5.1) * mm});
            skLineSegment(sketch, "E375", {"start": v(-26.5, -5.1) * mm, "end": v(-26.47, -5.09) * mm});
            skLineSegment(sketch, "E376", {"start": v(-26.47, -5.09) * mm, "end": v(-26.46, -5.07) * mm});
            skLineSegment(sketch, "E377", {"start": v(-26.46, -5.07) * mm, "end": v(-26.44, -5.05) * mm});
            skLineSegment(sketch, "E378", {"start": v(-26.44, -5.05) * mm, "end": v(-26.42, -5.03) * mm});
            skLineSegment(sketch, "E379", {"start": v(-26.42, -5.03) * mm, "end": v(-26.4, -5.01) * mm});
            skLineSegment(sketch, "E380", {"start": v(-26.4, -5.01) * mm, "end": v(-26.37, -5) * mm});
            skLineSegment(sketch, "E381", {"start": v(-26.37, -5) * mm, "end": v(-26.34, -4.98) * mm});
            skLineSegment(sketch, "E382", {"start": v(-7.72, -4.97) * mm, "end": v(-7.68, -4.98) * mm});
            skLineSegment(sketch, "E383", {"start": v(-7.68, -4.98) * mm, "end": v(-7.64, -4.98) * mm});
            skLineSegment(sketch, "E384", {"start": v(-7.64, -4.98) * mm, "end": v(-7.6, -4.98) * mm});
            skLineSegment(sketch, "E385", {"start": v(-7.6, -4.98) * mm, "end": v(-7.55, -4.98) * mm});
            skLineSegment(sketch, "E386", {"start": v(-7.55, -4.98) * mm, "end": v(-7.5, -4.98) * mm});
            skLineSegment(sketch, "E387", {"start": v(-7.5, -4.98) * mm, "end": v(-7.41, -4.97) * mm});
            skLineSegment(sketch, "E388", {"start": v(-7.41, -4.97) * mm, "end": v(-7.13, -4.95) * mm});
            skLineSegment(sketch, "E389", {"start": v(-7.13, -4.95) * mm, "end": v(-7.09, -4.94) * mm});
            skLineSegment(sketch, "E390", {"start": v(-7.09, -4.94) * mm, "end": v(-7.04, -4.94) * mm});
            skLineSegment(sketch, "E391", {"start": v(-7.04, -4.94) * mm, "end": v(-7, -4.94) * mm});
            skLineSegment(sketch, "E392", {"start": v(-7, -4.94) * mm, "end": v(-6.95, -4.94) * mm});
            skLineSegment(sketch, "E393", {"start": v(-6.95, -4.94) * mm, "end": v(-6.9, -4.94) * mm});
            skLineSegment(sketch, "E394", {"start": v(-6.9, -4.94) * mm, "end": v(-6.86, -4.95) * mm});
            skLineSegment(sketch, "E395", {"start": v(-6.86, -4.95) * mm, "end": v(-6.82, -4.95) * mm});
            skLineSegment(sketch, "E396", {"start": v(-6.82, -4.95) * mm, "end": v(-6.78, -4.96) * mm});
            skLineSegment(sketch, "E397", {"start": v(-6.78, -4.96) * mm, "end": v(-6.74, -4.97) * mm});
            skLineSegment(sketch, "E398", {"start": v(-6.74, -4.97) * mm, "end": v(-6.7, -4.99) * mm});
            skLineSegment(sketch, "E399", {"start": v(-6.7, -4.99) * mm, "end": v(-6.66, -5) * mm});
            skLineSegment(sketch, "E400", {"start": v(-6.66, -5) * mm, "end": v(-6.62, -5.03) * mm});
            skLineSegment(sketch, "E401", {"start": v(-6.62, -5.03) * mm, "end": v(-6.58, -5.05) * mm});
            skLineSegment(sketch, "E402", {"start": v(-6.58, -5.05) * mm, "end": v(-6.55, -5.08) * mm});
            skLineSegment(sketch, "E403", {"start": v(-6.55, -5.08) * mm, "end": v(-6.52, -5.1) * mm});
            skLineSegment(sketch, "E404", {"start": v(-6.52, -5.1) * mm, "end": v(-6.48, -5.14) * mm});
            skLineSegment(sketch, "E405", {"start": v(-6.48, -5.14) * mm, "end": v(-6.47, -5.18) * mm});
            skLineSegment(sketch, "E406", {"start": v(-6.47, -5.18) * mm, "end": v(-6.46, -5.21) * mm});
            skLineSegment(sketch, "E407", {"start": v(-6.46, -5.21) * mm, "end": v(-6.45, -5.24) * mm});
            skLineSegment(sketch, "E408", {"start": v(-6.45, -5.24) * mm, "end": v(-6.43, -5.31) * mm});
            skLineSegment(sketch, "E409", {"start": v(-6.43, -5.31) * mm, "end": v(-6.41, -5.38) * mm});
            skLineSegment(sketch, "E410", {"start": v(-6.41, -5.38) * mm, "end": v(-6.4, -5.45) * mm});
            skLineSegment(sketch, "E411", {"start": v(-6.4, -5.45) * mm, "end": v(-6.4, -5.52) * mm});
            skLineSegment(sketch, "E412", {"start": v(-6.4, -5.52) * mm, "end": v(-6.39, -5.59) * mm});
            skLineSegment(sketch, "E413", {"start": v(-6.39, -5.59) * mm, "end": v(-6.38, -5.7) * mm});
            skLineSegment(sketch, "E414", {"start": v(-6.38, -5.7) * mm, "end": v(-6.39, -5.83) * mm});
            skLineSegment(sketch, "E415", {"start": v(-6.39, -5.83) * mm, "end": v(-6.4, -6.08) * mm});
            skLineSegment(sketch, "E416", {"start": v(-6.4, -6.08) * mm, "end": v(-6.42, -6.15) * mm});
            skLineSegment(sketch, "E417", {"start": v(-6.42, -6.15) * mm, "end": v(-6.47, -6.3) * mm});
            skLineSegment(sketch, "E418", {"start": v(-6.47, -6.3) * mm, "end": v(-6.5, -6.36) * mm});
            skLineSegment(sketch, "E419", {"start": v(-6.5, -6.36) * mm, "end": v(-6.53, -6.4) * mm});
            skLineSegment(sketch, "E420", {"start": v(-6.53, -6.4) * mm, "end": v(-6.56, -6.43) * mm});
            skLineSegment(sketch, "E421", {"start": v(-6.56, -6.43) * mm, "end": v(-6.59, -6.46) * mm});
            skLineSegment(sketch, "E422", {"start": v(-6.59, -6.46) * mm, "end": v(-6.61, -6.47) * mm});
            skLineSegment(sketch, "E423", {"start": v(-6.61, -6.47) * mm, "end": v(-6.64, -6.49) * mm});
            skLineSegment(sketch, "E424", {"start": v(-6.64, -6.49) * mm, "end": v(-6.67, -6.5) * mm});
            skLineSegment(sketch, "E425", {"start": v(-6.67, -6.5) * mm, "end": v(-7.74, -6.53) * mm});
            skLineSegment(sketch, "E426", {"start": v(-7.74, -6.53) * mm, "end": v(-7.72, -4.97) * mm});
            skLineSegment(sketch, "E427", {"start": v(-26.35, -7.32) * mm, "end": v(-25.28, -7.3) * mm});
            skLineSegment(sketch, "E428", {"start": v(-25.28, -7.3) * mm, "end": v(-25.28, -8.87) * mm});
            skLineSegment(sketch, "E429", {"start": v(-25.28, -8.87) * mm, "end": v(-26.35, -8.85) * mm});
            skLineSegment(sketch, "E430", {"start": v(-26.35, -8.85) * mm, "end": v(-26.5, -8.7) * mm});
            skLineSegment(sketch, "E431", {"start": v(-26.5, -8.7) * mm, "end": v(-26.55, -8.62) * mm});
            skLineSegment(sketch, "E432", {"start": v(-26.55, -8.62) * mm, "end": v(-26.57, -8.57) * mm});
            skLineSegment(sketch, "E433", {"start": v(-26.57, -8.57) * mm, "end": v(-26.6, -8.52) * mm});
            skLineSegment(sketch, "E434", {"start": v(-26.6, -8.52) * mm, "end": v(-26.6, -8.47) * mm});
            skLineSegment(sketch, "E435", {"start": v(-26.6, -8.47) * mm, "end": v(-26.6, -8.45) * mm});
            skLineSegment(sketch, "E436", {"start": v(-26.6, -8.45) * mm, "end": v(-26.61, -8.37) * mm});
            skLineSegment(sketch, "E437", {"start": v(-26.61, -8.37) * mm, "end": v(-26.63, -8.2) * mm});
            skLineSegment(sketch, "E438", {"start": v(-26.63, -8.2) * mm, "end": v(-26.63, -8.08) * mm});
            skLineSegment(sketch, "E439", {"start": v(-26.63, -8.08) * mm, "end": v(-26.64, -8) * mm});
            skLineSegment(sketch, "E440", {"start": v(-26.64, -8) * mm, "end": v(-26.64, -7.95) * mm});
            skLineSegment(sketch, "E441", {"start": v(-26.64, -7.95) * mm, "end": v(-26.63, -7.9) * mm});
            skLineSegment(sketch, "E442", {"start": v(-26.63, -7.9) * mm, "end": v(-26.63, -7.86) * mm});
            skLineSegment(sketch, "E443", {"start": v(-26.63, -7.86) * mm, "end": v(-26.63, -7.82) * mm});
            skLineSegment(sketch, "E444", {"start": v(-26.63, -7.82) * mm, "end": v(-26.62, -7.78) * mm});
            skLineSegment(sketch, "E445", {"start": v(-26.62, -7.78) * mm, "end": v(-26.61, -7.74) * mm});
            skLineSegment(sketch, "E446", {"start": v(-26.61, -7.74) * mm, "end": v(-26.6, -7.7) * mm});
            skLineSegment(sketch, "E447", {"start": v(-26.6, -7.7) * mm, "end": v(-26.6, -7.66) * mm});
            skLineSegment(sketch, "E448", {"start": v(-26.6, -7.66) * mm, "end": v(-26.58, -7.62) * mm});
            skLineSegment(sketch, "E449", {"start": v(-26.58, -7.62) * mm, "end": v(-26.56, -7.58) * mm});
            skLineSegment(sketch, "E450", {"start": v(-26.56, -7.58) * mm, "end": v(-26.55, -7.54) * mm});
            skLineSegment(sketch, "E451", {"start": v(-26.55, -7.54) * mm, "end": v(-26.53, -7.5) * mm});
            skLineSegment(sketch, "E452", {"start": v(-26.53, -7.5) * mm, "end": v(-26.5, -7.47) * mm});
            skLineSegment(sketch, "E453", {"start": v(-26.5, -7.47) * mm, "end": v(-26.48, -7.44) * mm});
            skLineSegment(sketch, "E454", {"start": v(-26.48, -7.44) * mm, "end": v(-26.45, -7.4) * mm});
            skLineSegment(sketch, "E455", {"start": v(-26.45, -7.4) * mm, "end": v(-26.42, -7.38) * mm});
            skLineSegment(sketch, "E456", {"start": v(-26.42, -7.38) * mm, "end": v(-26.39, -7.35) * mm});
            skLineSegment(sketch, "E457", {"start": v(-26.39, -7.35) * mm, "end": v(-26.35, -7.32) * mm});
            skLineSegment(sketch, "E458", {"start": v(-7.73, -7.3) * mm, "end": v(-6.66, -7.32) * mm});
            skLineSegment(sketch, "E459", {"start": v(-6.66, -7.32) * mm, "end": v(-6.53, -7.44) * mm});
            skLineSegment(sketch, "E460", {"start": v(-6.53, -7.44) * mm, "end": v(-6.47, -7.53) * mm});
            skLineSegment(sketch, "E461", {"start": v(-6.47, -7.53) * mm, "end": v(-6.44, -7.58) * mm});
            skLineSegment(sketch, "E462", {"start": v(-6.44, -7.58) * mm, "end": v(-6.43, -7.63) * mm});
            skLineSegment(sketch, "E463", {"start": v(-6.43, -7.63) * mm, "end": v(-6.41, -7.68) * mm});
            skLineSegment(sketch, "E464", {"start": v(-6.41, -7.68) * mm, "end": v(-6.4, -7.7) * mm});
            skLineSegment(sketch, "E465", {"start": v(-6.4, -7.7) * mm, "end": v(-6.4, -7.79) * mm});
            skLineSegment(sketch, "E466", {"start": v(-6.4, -7.79) * mm, "end": v(-6.39, -7.96) * mm});
            skLineSegment(sketch, "E467", {"start": v(-6.39, -7.96) * mm, "end": v(-6.38, -8.09) * mm});
            skLineSegment(sketch, "E468", {"start": v(-6.38, -8.09) * mm, "end": v(-6.38, -8.17) * mm});
            skLineSegment(sketch, "E469", {"start": v(-6.38, -8.17) * mm, "end": v(-6.38, -8.22) * mm});
            skLineSegment(sketch, "E470", {"start": v(-6.38, -8.22) * mm, "end": v(-6.38, -8.26) * mm});
            skLineSegment(sketch, "E471", {"start": v(-6.38, -8.26) * mm, "end": v(-6.38, -8.3) * mm});
            skLineSegment(sketch, "E472", {"start": v(-6.38, -8.3) * mm, "end": v(-6.39, -8.34) * mm});
            skLineSegment(sketch, "E473", {"start": v(-6.39, -8.34) * mm, "end": v(-6.4, -8.39) * mm});
            skLineSegment(sketch, "E474", {"start": v(-6.4, -8.39) * mm, "end": v(-6.4, -8.43) * mm});
            skLineSegment(sketch, "E475", {"start": v(-6.4, -8.43) * mm, "end": v(-6.4, -8.47) * mm});
            skLineSegment(sketch, "E476", {"start": v(-6.4, -8.47) * mm, "end": v(-6.42, -8.5) * mm});
            skLineSegment(sketch, "E477", {"start": v(-6.42, -8.5) * mm, "end": v(-6.43, -8.55) * mm});
            skLineSegment(sketch, "E478", {"start": v(-6.43, -8.55) * mm, "end": v(-6.45, -8.58) * mm});
            skLineSegment(sketch, "E479", {"start": v(-6.45, -8.58) * mm, "end": v(-6.47, -8.62) * mm});
            skLineSegment(sketch, "E480", {"start": v(-6.47, -8.62) * mm, "end": v(-6.49, -8.66) * mm});
            skLineSegment(sketch, "E481", {"start": v(-6.49, -8.66) * mm, "end": v(-6.5, -8.7) * mm});
            skLineSegment(sketch, "E482", {"start": v(-6.5, -8.7) * mm, "end": v(-6.53, -8.73) * mm});
            skLineSegment(sketch, "E483", {"start": v(-6.53, -8.73) * mm, "end": v(-6.56, -8.76) * mm});
            skLineSegment(sketch, "E484", {"start": v(-6.56, -8.76) * mm, "end": v(-6.6, -8.79) * mm});
            skLineSegment(sketch, "E485", {"start": v(-6.6, -8.79) * mm, "end": v(-6.62, -8.82) * mm});
            skLineSegment(sketch, "E486", {"start": v(-6.62, -8.82) * mm, "end": v(-6.66, -8.85) * mm});
            skLineSegment(sketch, "E487", {"start": v(-6.66, -8.85) * mm, "end": v(-7.73, -8.87) * mm});
            skLineSegment(sketch, "E488", {"start": v(-7.73, -8.87) * mm, "end": v(-7.73, -7.3) * mm});
            skLineSegment(sketch, "E489", {"start": v(-26.38, -9.67) * mm, "end": v(-26.27, -9.66) * mm});
            skLineSegment(sketch, "E490", {"start": v(-26.27, -9.66) * mm, "end": v(-26.08, -9.64) * mm});
            skLineSegment(sketch, "E491", {"start": v(-26.08, -9.64) * mm, "end": v(-25.28, -9.63) * mm});
            skLineSegment(sketch, "E492", {"start": v(-25.28, -9.63) * mm, "end": v(-25.3, -11.2) * mm});
            skLineSegment(sketch, "E493", {"start": v(-25.3, -11.2) * mm, "end": v(-26.03, -11.2) * mm});
            skLineSegment(sketch, "E494", {"start": v(-26.03, -11.2) * mm, "end": v(-26.17, -11.2) * mm});
            skLineSegment(sketch, "E495", {"start": v(-26.17, -11.2) * mm, "end": v(-26.27, -11.19) * mm});
            skLineSegment(sketch, "E496", {"start": v(-26.27, -11.19) * mm, "end": v(-26.3, -11.18) * mm});
            skLineSegment(sketch, "E497", {"start": v(-26.3, -11.18) * mm, "end": v(-26.34, -11.17) * mm});
            skLineSegment(sketch, "E498", {"start": v(-26.34, -11.17) * mm, "end": v(-26.36, -11.16) * mm});
            skLineSegment(sketch, "E499", {"start": v(-26.36, -11.16) * mm, "end": v(-26.39, -11.15) * mm});
            skLineSegment(sketch, "E500", {"start": v(-26.39, -11.15) * mm, "end": v(-26.41, -11.13) * mm});
            skLineSegment(sketch, "E501", {"start": v(-26.41, -11.13) * mm, "end": v(-26.43, -11.11) * mm});
            skLineSegment(sketch, "E502", {"start": v(-26.43, -11.11) * mm, "end": v(-26.46, -11.1) * mm});
            skLineSegment(sketch, "E503", {"start": v(-26.46, -11.1) * mm, "end": v(-26.47, -11.08) * mm});
            skLineSegment(sketch, "E504", {"start": v(-26.47, -11.08) * mm, "end": v(-26.5, -11.05) * mm});
            skLineSegment(sketch, "E505", {"start": v(-26.5, -11.05) * mm, "end": v(-26.5, -11.03) * mm});
            skLineSegment(sketch, "E506", {"start": v(-26.5, -11.03) * mm, "end": v(-26.52, -11) * mm});
            skLineSegment(sketch, "E507", {"start": v(-26.52, -11) * mm, "end": v(-26.54, -10.98) * mm});
            skLineSegment(sketch, "E508", {"start": v(-26.54, -10.98) * mm, "end": v(-26.55, -10.95) * mm});
            skLineSegment(sketch, "E509", {"start": v(-26.55, -10.95) * mm, "end": v(-26.56, -10.93) * mm});
            skLineSegment(sketch, "E510", {"start": v(-26.56, -10.93) * mm, "end": v(-26.57, -10.9) * mm});
            skLineSegment(sketch, "E511", {"start": v(-26.57, -10.9) * mm, "end": v(-26.58, -10.87) * mm});
            skLineSegment(sketch, "E512", {"start": v(-26.58, -10.87) * mm, "end": v(-26.59, -10.84) * mm});
            skLineSegment(sketch, "E513", {"start": v(-26.59, -10.84) * mm, "end": v(-26.6, -10.78) * mm});
            skLineSegment(sketch, "E514", {"start": v(-26.6, -10.78) * mm, "end": v(-26.61, -10.72) * mm});
            skLineSegment(sketch, "E515", {"start": v(-26.61, -10.72) * mm, "end": v(-26.62, -10.63) * mm});
            skLineSegment(sketch, "E516", {"start": v(-26.62, -10.63) * mm, "end": v(-26.63, -10.55) * mm});
            skLineSegment(sketch, "E517", {"start": v(-26.63, -10.55) * mm, "end": v(-26.63, -10.5) * mm});
            skLineSegment(sketch, "E518", {"start": v(-26.63, -10.5) * mm, "end": v(-26.63, -10.47) * mm});
            skLineSegment(sketch, "E519", {"start": v(-26.63, -10.47) * mm, "end": v(-26.63, -10.38) * mm});
            skLineSegment(sketch, "E520", {"start": v(-26.63, -10.38) * mm, "end": v(-26.62, -10.23) * mm});
            skLineSegment(sketch, "E521", {"start": v(-26.62, -10.23) * mm, "end": v(-26.62, -10.14) * mm});
            skLineSegment(sketch, "E522", {"start": v(-26.62, -10.14) * mm, "end": v(-26.6, -10.08) * mm});
            skLineSegment(sketch, "E523", {"start": v(-26.6, -10.08) * mm, "end": v(-26.6, -10.02) * mm});
            skLineSegment(sketch, "E524", {"start": v(-26.6, -10.02) * mm, "end": v(-26.59, -9.99) * mm});
            skLineSegment(sketch, "E525", {"start": v(-26.59, -9.99) * mm, "end": v(-26.58, -9.96) * mm});
            skLineSegment(sketch, "E526", {"start": v(-26.58, -9.96) * mm, "end": v(-26.57, -9.93) * mm});
            skLineSegment(sketch, "E527", {"start": v(-26.57, -9.93) * mm, "end": v(-26.56, -9.9) * mm});
            skLineSegment(sketch, "E528", {"start": v(-26.56, -9.9) * mm, "end": v(-26.55, -9.87) * mm});
            skLineSegment(sketch, "E529", {"start": v(-26.55, -9.87) * mm, "end": v(-26.54, -9.85) * mm});
            skLineSegment(sketch, "E530", {"start": v(-26.54, -9.85) * mm, "end": v(-26.52, -9.82) * mm});
            skLineSegment(sketch, "E531", {"start": v(-26.52, -9.82) * mm, "end": v(-26.5, -9.8) * mm});
            skLineSegment(sketch, "E532", {"start": v(-26.5, -9.8) * mm, "end": v(-26.49, -9.77) * mm});
            skLineSegment(sketch, "E533", {"start": v(-26.49, -9.77) * mm, "end": v(-26.47, -9.75) * mm});
            skLineSegment(sketch, "E534", {"start": v(-26.47, -9.75) * mm, "end": v(-26.45, -9.73) * mm});
            skLineSegment(sketch, "E535", {"start": v(-26.45, -9.73) * mm, "end": v(-26.43, -9.71) * mm});
            skLineSegment(sketch, "E536", {"start": v(-26.43, -9.71) * mm, "end": v(-26.4, -9.7) * mm});
            skLineSegment(sketch, "E537", {"start": v(-26.4, -9.7) * mm, "end": v(-26.38, -9.67) * mm});
            skLineSegment(sketch, "E538", {"start": v(-7.73, -9.64) * mm, "end": v(-6.54, -9.67) * mm});
            skLineSegment(sketch, "E539", {"start": v(-6.54, -9.67) * mm, "end": v(-6.51, -9.75) * mm});
            skLineSegment(sketch, "E540", {"start": v(-6.51, -9.75) * mm, "end": v(-6.48, -9.83) * mm});
            skLineSegment(sketch, "E541", {"start": v(-6.48, -9.83) * mm, "end": v(-6.46, -9.9) * mm});
            skLineSegment(sketch, "E542", {"start": v(-6.46, -9.9) * mm, "end": v(-6.44, -9.99) * mm});
            skLineSegment(sketch, "E543", {"start": v(-6.44, -9.99) * mm, "end": v(-6.42, -10.07) * mm});
            skLineSegment(sketch, "E544", {"start": v(-6.42, -10.07) * mm, "end": v(-6.4, -10.15) * mm});
            skLineSegment(sketch, "E545", {"start": v(-6.4, -10.15) * mm, "end": v(-6.4, -10.23) * mm});
            skLineSegment(sketch, "E546", {"start": v(-6.4, -10.23) * mm, "end": v(-6.39, -10.32) * mm});
            skLineSegment(sketch, "E547", {"start": v(-6.39, -10.32) * mm, "end": v(-6.38, -10.4) * mm});
            skLineSegment(sketch, "E548", {"start": v(-6.38, -10.4) * mm, "end": v(-6.38, -10.44) * mm});
            skLineSegment(sketch, "E549", {"start": v(-6.38, -10.44) * mm, "end": v(-6.38, -10.48) * mm});
            skLineSegment(sketch, "E550", {"start": v(-6.38, -10.48) * mm, "end": v(-6.38, -10.53) * mm});
            skLineSegment(sketch, "E551", {"start": v(-6.38, -10.53) * mm, "end": v(-6.39, -10.57) * mm});
            skLineSegment(sketch, "E552", {"start": v(-6.39, -10.57) * mm, "end": v(-6.39, -10.6) * mm});
            skLineSegment(sketch, "E553", {"start": v(-6.39, -10.6) * mm, "end": v(-6.4, -10.65) * mm});
            skLineSegment(sketch, "E554", {"start": v(-6.4, -10.65) * mm, "end": v(-6.4, -10.7) * mm});
            skLineSegment(sketch, "E555", {"start": v(-6.4, -10.7) * mm, "end": v(-6.4, -10.73) * mm});
            skLineSegment(sketch, "E556", {"start": v(-6.4, -10.73) * mm, "end": v(-6.41, -10.77) * mm});
            skLineSegment(sketch, "E557", {"start": v(-6.41, -10.77) * mm, "end": v(-6.42, -10.82) * mm});
            skLineSegment(sketch, "E558", {"start": v(-6.42, -10.82) * mm, "end": v(-6.43, -10.86) * mm});
            skLineSegment(sketch, "E559", {"start": v(-6.43, -10.86) * mm, "end": v(-6.45, -10.92) * mm});
            skLineSegment(sketch, "E560", {"start": v(-6.45, -10.92) * mm, "end": v(-6.47, -10.97) * mm});
            skLineSegment(sketch, "E561", {"start": v(-6.47, -10.97) * mm, "end": v(-6.5, -11.03) * mm});
            skLineSegment(sketch, "E562", {"start": v(-6.5, -11.03) * mm, "end": v(-6.53, -11.07) * mm});
            skLineSegment(sketch, "E563", {"start": v(-6.53, -11.07) * mm, "end": v(-6.56, -11.1) * mm});
            skLineSegment(sketch, "E564", {"start": v(-6.56, -11.1) * mm, "end": v(-6.58, -11.12) * mm});
            skLineSegment(sketch, "E565", {"start": v(-6.58, -11.12) * mm, "end": v(-6.6, -11.14) * mm});
            skLineSegment(sketch, "E566", {"start": v(-6.6, -11.14) * mm, "end": v(-6.64, -11.15) * mm});
            skLineSegment(sketch, "E567", {"start": v(-6.64, -11.15) * mm, "end": v(-6.66, -11.17) * mm});
            skLineSegment(sketch, "E568", {"start": v(-6.66, -11.17) * mm, "end": v(-6.7, -11.18) * mm});
            skLineSegment(sketch, "E569", {"start": v(-6.7, -11.18) * mm, "end": v(-6.7, -11.18) * mm});
            skLineSegment(sketch, "E570", {"start": v(-6.7, -11.18) * mm, "end": v(-7.72, -11.2) * mm});
            skLineSegment(sketch, "E571", {"start": v(-7.72, -11.2) * mm, "end": v(-7.73, -9.64) * mm});
            skLineSegment(sketch, "E572", {"start": v(-26.47, -12.01) * mm, "end": v(-25.28, -11.98) * mm});
            skLineSegment(sketch, "E573", {"start": v(-25.28, -11.98) * mm, "end": v(-25.3, -13.53) * mm});
            skLineSegment(sketch, "E574", {"start": v(-25.3, -13.53) * mm, "end": v(-25.33, -13.53) * mm});
            skLineSegment(sketch, "E575", {"start": v(-25.33, -13.53) * mm, "end": v(-25.38, -13.52) * mm});
            skLineSegment(sketch, "E576", {"start": v(-25.38, -13.52) * mm, "end": v(-25.42, -13.52) * mm});
            skLineSegment(sketch, "E577", {"start": v(-25.42, -13.52) * mm, "end": v(-25.47, -13.52) * mm});
            skLineSegment(sketch, "E578", {"start": v(-25.47, -13.52) * mm, "end": v(-25.5, -13.52) * mm});
            skLineSegment(sketch, "E579", {"start": v(-25.5, -13.52) * mm, "end": v(-25.6, -13.53) * mm});
            skLineSegment(sketch, "E580", {"start": v(-25.6, -13.53) * mm, "end": v(-25.88, -13.56) * mm});
            skLineSegment(sketch, "E581", {"start": v(-25.88, -13.56) * mm, "end": v(-25.93, -13.56) * mm});
            skLineSegment(sketch, "E582", {"start": v(-25.93, -13.56) * mm, "end": v(-25.97, -13.56) * mm});
            skLineSegment(sketch, "E583", {"start": v(-25.97, -13.56) * mm, "end": v(-26.02, -13.56) * mm});
            skLineSegment(sketch, "E584", {"start": v(-26.02, -13.56) * mm, "end": v(-26.06, -13.56) * mm});
            skLineSegment(sketch, "E585", {"start": v(-26.06, -13.56) * mm, "end": v(-26.1, -13.56) * mm});
            skLineSegment(sketch, "E586", {"start": v(-26.1, -13.56) * mm, "end": v(-26.15, -13.56) * mm});
            skLineSegment(sketch, "E587", {"start": v(-26.15, -13.56) * mm, "end": v(-26.2, -13.55) * mm});
            skLineSegment(sketch, "E588", {"start": v(-26.2, -13.55) * mm, "end": v(-26.24, -13.54) * mm});
            skLineSegment(sketch, "E589", {"start": v(-26.24, -13.54) * mm, "end": v(-26.28, -13.53) * mm});
            skLineSegment(sketch, "E590", {"start": v(-26.28, -13.53) * mm, "end": v(-26.32, -13.52) * mm});
            skLineSegment(sketch, "E591", {"start": v(-26.32, -13.52) * mm, "end": v(-26.36, -13.5) * mm});
            skLineSegment(sketch, "E592", {"start": v(-26.36, -13.5) * mm, "end": v(-26.4, -13.48) * mm});
            skLineSegment(sketch, "E593", {"start": v(-26.4, -13.48) * mm, "end": v(-26.43, -13.45) * mm});
            skLineSegment(sketch, "E594", {"start": v(-26.43, -13.45) * mm, "end": v(-26.46, -13.43) * mm});
            skLineSegment(sketch, "E595", {"start": v(-26.46, -13.43) * mm, "end": v(-26.5, -13.4) * mm});
            skLineSegment(sketch, "E596", {"start": v(-26.5, -13.4) * mm, "end": v(-26.53, -13.36) * mm});
            skLineSegment(sketch, "E597", {"start": v(-26.53, -13.36) * mm, "end": v(-26.55, -13.31) * mm});
            skLineSegment(sketch, "E598", {"start": v(-26.55, -13.31) * mm, "end": v(-26.56, -13.27) * mm});
            skLineSegment(sketch, "E599", {"start": v(-26.56, -13.27) * mm, "end": v(-26.57, -13.22) * mm});
            skLineSegment(sketch, "E600", {"start": v(-26.57, -13.22) * mm, "end": v(-26.59, -13.18) * mm});
            skLineSegment(sketch, "E601", {"start": v(-26.59, -13.18) * mm, "end": v(-26.6, -13.13) * mm});
            skLineSegment(sketch, "E602", {"start": v(-26.6, -13.13) * mm, "end": v(-26.6, -13.08) * mm});
            skLineSegment(sketch, "E603", {"start": v(-26.6, -13.08) * mm, "end": v(-26.61, -13.04) * mm});
            skLineSegment(sketch, "E604", {"start": v(-26.61, -13.04) * mm, "end": v(-26.62, -12.99) * mm});
            skLineSegment(sketch, "E605", {"start": v(-26.62, -12.99) * mm, "end": v(-26.63, -12.94) * mm});
            skLineSegment(sketch, "E606", {"start": v(-26.63, -12.94) * mm, "end": v(-26.63, -12.9) * mm});
            skLineSegment(sketch, "E607", {"start": v(-26.63, -12.9) * mm, "end": v(-26.63, -12.85) * mm});
            skLineSegment(sketch, "E608", {"start": v(-26.63, -12.85) * mm, "end": v(-26.63, -12.8) * mm});
            skLineSegment(sketch, "E609", {"start": v(-26.63, -12.8) * mm, "end": v(-26.63, -12.75) * mm});
            skLineSegment(sketch, "E610", {"start": v(-26.63, -12.75) * mm, "end": v(-26.63, -12.7) * mm});
            skLineSegment(sketch, "E611", {"start": v(-26.63, -12.7) * mm, "end": v(-26.63, -12.66) * mm});
            skLineSegment(sketch, "E612", {"start": v(-26.63, -12.66) * mm, "end": v(-26.62, -12.6) * mm});
            skLineSegment(sketch, "E613", {"start": v(-26.62, -12.6) * mm, "end": v(-26.62, -12.56) * mm});
            skLineSegment(sketch, "E614", {"start": v(-26.62, -12.56) * mm, "end": v(-26.61, -12.51) * mm});
            skLineSegment(sketch, "E615", {"start": v(-26.61, -12.51) * mm, "end": v(-26.6, -12.47) * mm});
            skLineSegment(sketch, "E616", {"start": v(-26.6, -12.47) * mm, "end": v(-26.6, -12.42) * mm});
            skLineSegment(sketch, "E617", {"start": v(-26.6, -12.42) * mm, "end": v(-26.59, -12.37) * mm});
            skLineSegment(sketch, "E618", {"start": v(-26.59, -12.37) * mm, "end": v(-26.58, -12.33) * mm});
            skLineSegment(sketch, "E619", {"start": v(-26.58, -12.33) * mm, "end": v(-26.56, -12.28) * mm});
            skLineSegment(sketch, "E620", {"start": v(-26.56, -12.28) * mm, "end": v(-26.55, -12.23) * mm});
            skLineSegment(sketch, "E621", {"start": v(-26.55, -12.23) * mm, "end": v(-26.54, -12.19) * mm});
            skLineSegment(sketch, "E622", {"start": v(-26.54, -12.19) * mm, "end": v(-26.52, -12.14) * mm});
            skLineSegment(sketch, "E623", {"start": v(-26.52, -12.14) * mm, "end": v(-26.5, -12.1) * mm});
            skLineSegment(sketch, "E624", {"start": v(-26.5, -12.1) * mm, "end": v(-26.49, -12.05) * mm});
            skLineSegment(sketch, "E625", {"start": v(-26.49, -12.05) * mm, "end": v(-26.47, -12.01) * mm});
            skLineSegment(sketch, "E626", {"start": v(-7.73, -11.98) * mm, "end": v(-6.54, -12.01) * mm});
            skLineSegment(sketch, "E627", {"start": v(-6.54, -12.01) * mm, "end": v(-6.52, -12.06) * mm});
            skLineSegment(sketch, "E628", {"start": v(-6.52, -12.06) * mm, "end": v(-6.5, -12.1) * mm});
            skLineSegment(sketch, "E629", {"start": v(-6.5, -12.1) * mm, "end": v(-6.49, -12.16) * mm});
            skLineSegment(sketch, "E630", {"start": v(-6.49, -12.16) * mm, "end": v(-6.47, -12.2) * mm});
            skLineSegment(sketch, "E631", {"start": v(-6.47, -12.2) * mm, "end": v(-6.46, -12.26) * mm});
            skLineSegment(sketch, "E632", {"start": v(-6.46, -12.26) * mm, "end": v(-6.44, -12.31) * mm});
            skLineSegment(sketch, "E633", {"start": v(-6.44, -12.31) * mm, "end": v(-6.43, -12.37) * mm});
            skLineSegment(sketch, "E634", {"start": v(-6.43, -12.37) * mm, "end": v(-6.42, -12.42) * mm});
            skLineSegment(sketch, "E635", {"start": v(-6.42, -12.42) * mm, "end": v(-6.4, -12.48) * mm});
            skLineSegment(sketch, "E636", {"start": v(-6.4, -12.48) * mm, "end": v(-6.4, -12.53) * mm});
            skLineSegment(sketch, "E637", {"start": v(-6.4, -12.53) * mm, "end": v(-6.39, -12.59) * mm});
            skLineSegment(sketch, "E638", {"start": v(-6.39, -12.59) * mm, "end": v(-6.38, -12.64) * mm});
            skLineSegment(sketch, "E639", {"start": v(-6.38, -12.64) * mm, "end": v(-6.38, -12.7) * mm});
            skLineSegment(sketch, "E640", {"start": v(-6.38, -12.7) * mm, "end": v(-6.37, -12.75) * mm});
            skLineSegment(sketch, "E641", {"start": v(-6.37, -12.75) * mm, "end": v(-6.37, -12.8) * mm});
            skLineSegment(sketch, "E642", {"start": v(-6.37, -12.8) * mm, "end": v(-6.37, -12.86) * mm});
            skLineSegment(sketch, "E643", {"start": v(-6.37, -12.86) * mm, "end": v(-6.38, -12.91) * mm});
            skLineSegment(sketch, "E644", {"start": v(-6.38, -12.91) * mm, "end": v(-6.38, -12.97) * mm});
            skLineSegment(sketch, "E645", {"start": v(-6.38, -12.97) * mm, "end": v(-6.39, -13.02) * mm});
            skLineSegment(sketch, "E646", {"start": v(-6.39, -13.02) * mm, "end": v(-6.4, -13.07) * mm});
            skLineSegment(sketch, "E647", {"start": v(-6.4, -13.07) * mm, "end": v(-6.4, -13.12) * mm});
            skLineSegment(sketch, "E648", {"start": v(-6.4, -13.12) * mm, "end": v(-6.42, -13.17) * mm});
            skLineSegment(sketch, "E649", {"start": v(-6.42, -13.17) * mm, "end": v(-6.44, -13.22) * mm});
            skLineSegment(sketch, "E650", {"start": v(-6.44, -13.22) * mm, "end": v(-6.46, -13.27) * mm});
            skLineSegment(sketch, "E651", {"start": v(-6.46, -13.27) * mm, "end": v(-6.49, -13.32) * mm});
            skLineSegment(sketch, "E652", {"start": v(-6.49, -13.32) * mm, "end": v(-6.51, -13.36) * mm});
            skLineSegment(sketch, "E653", {"start": v(-6.51, -13.36) * mm, "end": v(-6.54, -13.4) * mm});
            skLineSegment(sketch, "E654", {"start": v(-6.54, -13.4) * mm, "end": v(-6.58, -13.45) * mm});
            skLineSegment(sketch, "E655", {"start": v(-6.58, -13.45) * mm, "end": v(-6.61, -13.49) * mm});
            skLineSegment(sketch, "E656", {"start": v(-6.61, -13.49) * mm, "end": v(-6.65, -13.5) * mm});
            skLineSegment(sketch, "E657", {"start": v(-6.65, -13.5) * mm, "end": v(-6.69, -13.5) * mm});
            skLineSegment(sketch, "E658", {"start": v(-6.69, -13.5) * mm, "end": v(-6.72, -13.52) * mm});
            skLineSegment(sketch, "E659", {"start": v(-6.72, -13.52) * mm, "end": v(-6.76, -13.52) * mm});
            skLineSegment(sketch, "E660", {"start": v(-6.76, -13.52) * mm, "end": v(-6.8, -13.53) * mm});
            skLineSegment(sketch, "E661", {"start": v(-6.8, -13.53) * mm, "end": v(-6.87, -13.54) * mm});
            skLineSegment(sketch, "E662", {"start": v(-6.87, -13.54) * mm, "end": v(-6.95, -13.55) * mm});
            skLineSegment(sketch, "E663", {"start": v(-6.95, -13.55) * mm, "end": v(-7.06, -13.55) * mm});
            skLineSegment(sketch, "E664", {"start": v(-7.06, -13.55) * mm, "end": v(-7.6, -13.53) * mm});
            skLineSegment(sketch, "E665", {"start": v(-7.6, -13.53) * mm, "end": v(-7.72, -13.53) * mm});
            skLineSegment(sketch, "E666", {"start": v(-7.72, -13.53) * mm, "end": v(-7.73, -11.98) * mm});
            skLineSegment(sketch, "E667", {"start": v(-20.77, -15.27) * mm, "end": v(-19.21, -15.27) * mm});
            skLineSegment(sketch, "E668", {"start": v(-19.21, -15.27) * mm, "end": v(-19.21, -16.13) * mm});
            skLineSegment(sketch, "E669", {"start": v(-19.21, -16.13) * mm, "end": v(-19.22, -16.27) * mm});
            skLineSegment(sketch, "E670", {"start": v(-19.22, -16.27) * mm, "end": v(-19.23, -16.29) * mm});
            skLineSegment(sketch, "E671", {"start": v(-19.23, -16.29) * mm, "end": v(-19.23, -16.3) * mm});
            skLineSegment(sketch, "E672", {"start": v(-19.23, -16.3) * mm, "end": v(-19.24, -16.32) * mm});
            skLineSegment(sketch, "E673", {"start": v(-19.24, -16.32) * mm, "end": v(-19.24, -16.34) * mm});
            skLineSegment(sketch, "E674", {"start": v(-19.24, -16.34) * mm, "end": v(-19.25, -16.35) * mm});
            skLineSegment(sketch, "E675", {"start": v(-19.25, -16.35) * mm, "end": v(-19.26, -16.37) * mm});
            skLineSegment(sketch, "E676", {"start": v(-19.26, -16.37) * mm, "end": v(-19.27, -16.38) * mm});
            skLineSegment(sketch, "E677", {"start": v(-19.27, -16.38) * mm, "end": v(-19.28, -16.4) * mm});
            skLineSegment(sketch, "E678", {"start": v(-19.28, -16.4) * mm, "end": v(-19.3, -16.41) * mm});
            skLineSegment(sketch, "E679", {"start": v(-19.3, -16.41) * mm, "end": v(-19.32, -16.43) * mm});
            skLineSegment(sketch, "E680", {"start": v(-19.32, -16.43) * mm, "end": v(-19.34, -16.46) * mm});
            skLineSegment(sketch, "E681", {"start": v(-19.34, -16.46) * mm, "end": v(-19.39, -16.49) * mm});
            skLineSegment(sketch, "E682", {"start": v(-19.39, -16.49) * mm, "end": v(-19.47, -16.53) * mm});
            skLineSegment(sketch, "E683", {"start": v(-19.47, -16.53) * mm, "end": v(-19.6, -16.58) * mm});
            skLineSegment(sketch, "E684", {"start": v(-19.6, -16.58) * mm, "end": v(-19.69, -16.6) * mm});
            skLineSegment(sketch, "E685", {"start": v(-19.69, -16.6) * mm, "end": v(-19.73, -16.6) * mm});
            skLineSegment(sketch, "E686", {"start": v(-19.73, -16.6) * mm, "end": v(-19.77, -16.6) * mm});
            skLineSegment(sketch, "E687", {"start": v(-19.77, -16.6) * mm, "end": v(-19.81, -16.61) * mm});
            skLineSegment(sketch, "E688", {"start": v(-19.81, -16.61) * mm, "end": v(-19.86, -16.62) * mm});
            skLineSegment(sketch, "E689", {"start": v(-19.86, -16.62) * mm, "end": v(-19.9, -16.62) * mm});
            skLineSegment(sketch, "E690", {"start": v(-19.9, -16.62) * mm, "end": v(-19.94, -16.62) * mm});
            skLineSegment(sketch, "E691", {"start": v(-19.94, -16.62) * mm, "end": v(-19.98, -16.62) * mm});
            skLineSegment(sketch, "E692", {"start": v(-19.98, -16.62) * mm, "end": v(-20.03, -16.62) * mm});
            skLineSegment(sketch, "E693", {"start": v(-20.03, -16.62) * mm, "end": v(-20.07, -16.62) * mm});
            skLineSegment(sketch, "E694", {"start": v(-20.07, -16.62) * mm, "end": v(-20.11, -16.62) * mm});
            skLineSegment(sketch, "E695", {"start": v(-20.11, -16.62) * mm, "end": v(-20.15, -16.62) * mm});
            skLineSegment(sketch, "E696", {"start": v(-20.15, -16.62) * mm, "end": v(-20.2, -16.61) * mm});
            skLineSegment(sketch, "E697", {"start": v(-20.2, -16.61) * mm, "end": v(-20.24, -16.6) * mm});
            skLineSegment(sketch, "E698", {"start": v(-20.24, -16.6) * mm, "end": v(-20.28, -16.6) * mm});
            skLineSegment(sketch, "E699", {"start": v(-20.28, -16.6) * mm, "end": v(-20.32, -16.6) * mm});
            skLineSegment(sketch, "E700", {"start": v(-20.32, -16.6) * mm, "end": v(-20.36, -16.58) * mm});
            skLineSegment(sketch, "E701", {"start": v(-20.36, -16.58) * mm, "end": v(-20.4, -16.57) * mm});
            skLineSegment(sketch, "E702", {"start": v(-20.4, -16.57) * mm, "end": v(-20.44, -16.56) * mm});
            skLineSegment(sketch, "E703", {"start": v(-20.44, -16.56) * mm, "end": v(-20.48, -16.54) * mm});
            skLineSegment(sketch, "E704", {"start": v(-20.48, -16.54) * mm, "end": v(-20.52, -16.53) * mm});
            skLineSegment(sketch, "E705", {"start": v(-20.52, -16.53) * mm, "end": v(-20.56, -16.51) * mm});
            skLineSegment(sketch, "E706", {"start": v(-20.56, -16.51) * mm, "end": v(-20.6, -16.5) * mm});
            skLineSegment(sketch, "E707", {"start": v(-20.6, -16.5) * mm, "end": v(-20.64, -16.47) * mm});
            skLineSegment(sketch, "E708", {"start": v(-20.64, -16.47) * mm, "end": v(-20.68, -16.45) * mm});
            skLineSegment(sketch, "E709", {"start": v(-20.68, -16.45) * mm, "end": v(-20.71, -16.43) * mm});
            skLineSegment(sketch, "E710", {"start": v(-20.71, -16.43) * mm, "end": v(-20.75, -16.4) * mm});
            skLineSegment(sketch, "E711", {"start": v(-20.75, -16.4) * mm, "end": v(-20.78, -16.38) * mm});
            skLineSegment(sketch, "E712", {"start": v(-20.78, -16.38) * mm, "end": v(-20.77, -15.27) * mm});
            skLineSegment(sketch, "E713", {"start": v(-18.48, -15.27) * mm, "end": v(-16.91, -15.27) * mm});
            skLineSegment(sketch, "E714", {"start": v(-16.91, -15.27) * mm, "end": v(-16.89, -16.15) * mm});
            skLineSegment(sketch, "E715", {"start": v(-16.89, -16.15) * mm, "end": v(-16.9, -16.21) * mm});
            skLineSegment(sketch, "E716", {"start": v(-16.9, -16.21) * mm, "end": v(-16.9, -16.27) * mm});
            skLineSegment(sketch, "E717", {"start": v(-16.9, -16.27) * mm, "end": v(-16.93, -16.32) * mm});
            skLineSegment(sketch, "E718", {"start": v(-16.93, -16.32) * mm, "end": v(-16.96, -16.37) * mm});
            skLineSegment(sketch, "E719", {"start": v(-16.96, -16.37) * mm, "end": v(-17, -16.42) * mm});
            skLineSegment(sketch, "E720", {"start": v(-17, -16.42) * mm, "end": v(-17.02, -16.45) * mm});
            skLineSegment(sketch, "E721", {"start": v(-17.02, -16.45) * mm, "end": v(-17.04, -16.47) * mm});
            skLineSegment(sketch, "E722", {"start": v(-17.04, -16.47) * mm, "end": v(-17.07, -16.5) * mm});
            skLineSegment(sketch, "E723", {"start": v(-17.07, -16.5) * mm, "end": v(-17.1, -16.52) * mm});
            skLineSegment(sketch, "E724", {"start": v(-17.1, -16.52) * mm, "end": v(-17.13, -16.54) * mm});
            skLineSegment(sketch, "E725", {"start": v(-17.13, -16.54) * mm, "end": v(-17.15, -16.55) * mm});
            skLineSegment(sketch, "E726", {"start": v(-17.15, -16.55) * mm, "end": v(-17.17, -16.56) * mm});
            skLineSegment(sketch, "E727", {"start": v(-17.17, -16.56) * mm, "end": v(-17.19, -16.56) * mm});
            skLineSegment(sketch, "E728", {"start": v(-17.19, -16.56) * mm, "end": v(-17.2, -16.57) * mm});
            skLineSegment(sketch, "E729", {"start": v(-17.2, -16.57) * mm, "end": v(-17.22, -16.57) * mm});
            skLineSegment(sketch, "E730", {"start": v(-17.22, -16.57) * mm, "end": v(-17.24, -16.57) * mm});
            skLineSegment(sketch, "E731", {"start": v(-17.24, -16.57) * mm, "end": v(-17.26, -16.58) * mm});
            skLineSegment(sketch, "E732", {"start": v(-17.26, -16.58) * mm, "end": v(-17.3, -16.58) * mm});
            skLineSegment(sketch, "E733", {"start": v(-17.3, -16.58) * mm, "end": v(-17.39, -16.6) * mm});
            skLineSegment(sketch, "E734", {"start": v(-17.39, -16.6) * mm, "end": v(-17.47, -16.61) * mm});
            skLineSegment(sketch, "E735", {"start": v(-17.47, -16.61) * mm, "end": v(-17.56, -16.62) * mm});
            skLineSegment(sketch, "E736", {"start": v(-17.56, -16.62) * mm, "end": v(-17.6, -16.62) * mm});
            skLineSegment(sketch, "E737", {"start": v(-17.6, -16.62) * mm, "end": v(-17.65, -16.63) * mm});
            skLineSegment(sketch, "E738", {"start": v(-17.65, -16.63) * mm, "end": v(-17.7, -16.63) * mm});
            skLineSegment(sketch, "E739", {"start": v(-17.7, -16.63) * mm, "end": v(-17.74, -16.63) * mm});
            skLineSegment(sketch, "E740", {"start": v(-17.74, -16.63) * mm, "end": v(-17.79, -16.63) * mm});
            skLineSegment(sketch, "E741", {"start": v(-17.79, -16.63) * mm, "end": v(-17.83, -16.62) * mm});
            skLineSegment(sketch, "E742", {"start": v(-17.83, -16.62) * mm, "end": v(-17.88, -16.62) * mm});
            skLineSegment(sketch, "E743", {"start": v(-17.88, -16.62) * mm, "end": v(-17.92, -16.61) * mm});
            skLineSegment(sketch, "E744", {"start": v(-17.92, -16.61) * mm, "end": v(-17.96, -16.6) * mm});
            skLineSegment(sketch, "E745", {"start": v(-17.96, -16.6) * mm, "end": v(-18, -16.6) * mm});
            skLineSegment(sketch, "E746", {"start": v(-18, -16.6) * mm, "end": v(-18.05, -16.59) * mm});
            skLineSegment(sketch, "E747", {"start": v(-18.05, -16.59) * mm, "end": v(-18.1, -16.57) * mm});
            skLineSegment(sketch, "E748", {"start": v(-18.1, -16.57) * mm, "end": v(-18.13, -16.56) * mm});
            skLineSegment(sketch, "E749", {"start": v(-18.13, -16.56) * mm, "end": v(-18.17, -16.54) * mm});
            skLineSegment(sketch, "E750", {"start": v(-18.17, -16.54) * mm, "end": v(-18.2, -16.52) * mm});
            skLineSegment(sketch, "E751", {"start": v(-18.2, -16.52) * mm, "end": v(-18.25, -16.5) * mm});
            skLineSegment(sketch, "E752", {"start": v(-18.25, -16.5) * mm, "end": v(-18.28, -16.48) * mm});
            skLineSegment(sketch, "E753", {"start": v(-18.28, -16.48) * mm, "end": v(-18.32, -16.45) * mm});
            skLineSegment(sketch, "E754", {"start": v(-18.32, -16.45) * mm, "end": v(-18.35, -16.42) * mm});
            skLineSegment(sketch, "E755", {"start": v(-18.35, -16.42) * mm, "end": v(-18.38, -16.39) * mm});
            skLineSegment(sketch, "E756", {"start": v(-18.38, -16.39) * mm, "end": v(-18.4, -16.35) * mm});
            skLineSegment(sketch, "E757", {"start": v(-18.4, -16.35) * mm, "end": v(-18.44, -16.32) * mm});
            skLineSegment(sketch, "E758", {"start": v(-18.44, -16.32) * mm, "end": v(-18.45, -16.25) * mm});
            skLineSegment(sketch, "E759", {"start": v(-18.45, -16.25) * mm, "end": v(-18.46, -16.14) * mm});
            skLineSegment(sketch, "E760", {"start": v(-18.46, -16.14) * mm, "end": v(-18.48, -15.96) * mm});
            skLineSegment(sketch, "E761", {"start": v(-18.48, -15.96) * mm, "end": v(-18.48, -15.27) * mm});
            skLineSegment(sketch, "E762", {"start": v(-16.1, -15.27) * mm, "end": v(-14.53, -15.27) * mm});
            skLineSegment(sketch, "E763", {"start": v(-14.53, -15.27) * mm, "end": v(-14.53, -15.99) * mm});
            skLineSegment(sketch, "E764", {"start": v(-14.53, -15.99) * mm, "end": v(-14.54, -16.16) * mm});
            skLineSegment(sketch, "E765", {"start": v(-14.54, -16.16) * mm, "end": v(-14.55, -16.26) * mm});
            skLineSegment(sketch, "E766", {"start": v(-14.55, -16.26) * mm, "end": v(-14.57, -16.3) * mm});
            skLineSegment(sketch, "E767", {"start": v(-14.57, -16.3) * mm, "end": v(-14.59, -16.33) * mm});
            skLineSegment(sketch, "E768", {"start": v(-14.59, -16.33) * mm, "end": v(-14.6, -16.36) * mm});
            skLineSegment(sketch, "E769", {"start": v(-14.6, -16.36) * mm, "end": v(-14.63, -16.38) * mm});
            skLineSegment(sketch, "E770", {"start": v(-14.63, -16.38) * mm, "end": v(-14.65, -16.41) * mm});
            skLineSegment(sketch, "E771", {"start": v(-14.65, -16.41) * mm, "end": v(-14.67, -16.44) * mm});
            skLineSegment(sketch, "E772", {"start": v(-14.67, -16.44) * mm, "end": v(-14.7, -16.46) * mm});
            skLineSegment(sketch, "E773", {"start": v(-14.7, -16.46) * mm, "end": v(-14.73, -16.48) * mm});
            skLineSegment(sketch, "E774", {"start": v(-14.73, -16.48) * mm, "end": v(-14.76, -16.5) * mm});
            skLineSegment(sketch, "E775", {"start": v(-14.76, -16.5) * mm, "end": v(-14.78, -16.52) * mm});
            skLineSegment(sketch, "E776", {"start": v(-14.78, -16.52) * mm, "end": v(-14.82, -16.53) * mm});
            skLineSegment(sketch, "E777", {"start": v(-14.82, -16.53) * mm, "end": v(-14.85, -16.55) * mm});
            skLineSegment(sketch, "E778", {"start": v(-14.85, -16.55) * mm, "end": v(-14.88, -16.56) * mm});
            skLineSegment(sketch, "E779", {"start": v(-14.88, -16.56) * mm, "end": v(-14.91, -16.57) * mm});
            skLineSegment(sketch, "E780", {"start": v(-14.91, -16.57) * mm, "end": v(-14.95, -16.58) * mm});
            skLineSegment(sketch, "E781", {"start": v(-14.95, -16.58) * mm, "end": v(-14.98, -16.59) * mm});
            skLineSegment(sketch, "E782", {"start": v(-14.98, -16.59) * mm, "end": v(-15.02, -16.6) * mm});
            skLineSegment(sketch, "E783", {"start": v(-15.02, -16.6) * mm, "end": v(-15.05, -16.6) * mm});
            skLineSegment(sketch, "E784", {"start": v(-15.05, -16.6) * mm, "end": v(-15.1, -16.6) * mm});
            skLineSegment(sketch, "E785", {"start": v(-15.1, -16.6) * mm, "end": v(-15.16, -16.61) * mm});
            skLineSegment(sketch, "E786", {"start": v(-15.16, -16.61) * mm, "end": v(-15.24, -16.62) * mm});
            skLineSegment(sketch, "E787", {"start": v(-15.24, -16.62) * mm, "end": v(-15.3, -16.62) * mm});
            skLineSegment(sketch, "E788", {"start": v(-15.3, -16.62) * mm, "end": v(-15.38, -16.62) * mm});
            skLineSegment(sketch, "E789", {"start": v(-15.38, -16.62) * mm, "end": v(-15.44, -16.61) * mm});
            skLineSegment(sketch, "E790", {"start": v(-15.44, -16.61) * mm, "end": v(-15.5, -16.62) * mm});
            skLineSegment(sketch, "E791", {"start": v(-15.5, -16.62) * mm, "end": v(-15.55, -16.61) * mm});
            skLineSegment(sketch, "E792", {"start": v(-15.55, -16.61) * mm, "end": v(-15.6, -16.6) * mm});
            skLineSegment(sketch, "E793", {"start": v(-15.6, -16.6) * mm, "end": v(-15.66, -16.6) * mm});
            skLineSegment(sketch, "E794", {"start": v(-15.66, -16.6) * mm, "end": v(-15.71, -16.59) * mm});
            skLineSegment(sketch, "E795", {"start": v(-15.71, -16.59) * mm, "end": v(-15.74, -16.58) * mm});
            skLineSegment(sketch, "E796", {"start": v(-15.74, -16.58) * mm, "end": v(-15.77, -16.57) * mm});
            skLineSegment(sketch, "E797", {"start": v(-15.77, -16.57) * mm, "end": v(-15.8, -16.56) * mm});
            skLineSegment(sketch, "E798", {"start": v(-15.8, -16.56) * mm, "end": v(-15.82, -16.55) * mm});
            skLineSegment(sketch, "E799", {"start": v(-15.82, -16.55) * mm, "end": v(-15.84, -16.54) * mm});
            skLineSegment(sketch, "E800", {"start": v(-15.84, -16.54) * mm, "end": v(-15.87, -16.53) * mm});
            skLineSegment(sketch, "E801", {"start": v(-15.87, -16.53) * mm, "end": v(-15.9, -16.52) * mm});
            skLineSegment(sketch, "E802", {"start": v(-15.9, -16.52) * mm, "end": v(-15.92, -16.5) * mm});
            skLineSegment(sketch, "E803", {"start": v(-15.92, -16.5) * mm, "end": v(-15.94, -16.49) * mm});
            skLineSegment(sketch, "E804", {"start": v(-15.94, -16.49) * mm, "end": v(-15.96, -16.47) * mm});
            skLineSegment(sketch, "E805", {"start": v(-15.96, -16.47) * mm, "end": v(-15.98, -16.46) * mm});
            skLineSegment(sketch, "E806", {"start": v(-15.98, -16.46) * mm, "end": v(-16, -16.44) * mm});
            skLineSegment(sketch, "E807", {"start": v(-16, -16.44) * mm, "end": v(-16.02, -16.42) * mm});
            skLineSegment(sketch, "E808", {"start": v(-16.02, -16.42) * mm, "end": v(-16.04, -16.4) * mm});
            skLineSegment(sketch, "E809", {"start": v(-16.04, -16.4) * mm, "end": v(-16.05, -16.38) * mm});
            skLineSegment(sketch, "E810", {"start": v(-16.05, -16.38) * mm, "end": v(-16.07, -16.35) * mm});
            skLineSegment(sketch, "E811", {"start": v(-16.07, -16.35) * mm, "end": v(-16.08, -16.33) * mm});
            skLineSegment(sketch, "E812", {"start": v(-16.08, -16.33) * mm, "end": v(-16.1, -16.3) * mm});
            skLineSegment(sketch, "E813", {"start": v(-16.1, -16.3) * mm, "end": v(-16.1, -16.28) * mm});
            skLineSegment(sketch, "E814", {"start": v(-16.1, -16.28) * mm, "end": v(-16.12, -16.18) * mm});
            skLineSegment(sketch, "E815", {"start": v(-16.12, -16.18) * mm, "end": v(-16.13, -16.04) * mm});
            skLineSegment(sketch, "E816", {"start": v(-16.13, -16.04) * mm, "end": v(-16.13, -15.76) * mm});
            skLineSegment(sketch, "E817", {"start": v(-16.13, -15.76) * mm, "end": v(-16.1, -15.27) * mm});
            skLineSegment(sketch, "E818", {"start": v(-13.8, -15.27) * mm, "end": v(-12.24, -15.27) * mm});
            skLineSegment(sketch, "E819", {"start": v(-12.24, -15.27) * mm, "end": v(-12.23, -16.38) * mm});
            skLineSegment(sketch, "E820", {"start": v(-12.23, -16.38) * mm, "end": v(-12.27, -16.4) * mm});
            skLineSegment(sketch, "E821", {"start": v(-12.27, -16.4) * mm, "end": v(-12.3, -16.43) * mm});
            skLineSegment(sketch, "E822", {"start": v(-12.3, -16.43) * mm, "end": v(-12.34, -16.45) * mm});
            skLineSegment(sketch, "E823", {"start": v(-12.34, -16.45) * mm, "end": v(-12.38, -16.48) * mm});
            skLineSegment(sketch, "E824", {"start": v(-12.38, -16.48) * mm, "end": v(-12.42, -16.5) * mm});
            skLineSegment(sketch, "E825", {"start": v(-12.42, -16.5) * mm, "end": v(-12.46, -16.51) * mm});
            skLineSegment(sketch, "E826", {"start": v(-12.46, -16.51) * mm, "end": v(-12.5, -16.53) * mm});
            skLineSegment(sketch, "E827", {"start": v(-12.5, -16.53) * mm, "end": v(-12.54, -16.55) * mm});
            skLineSegment(sketch, "E828", {"start": v(-12.54, -16.55) * mm, "end": v(-12.58, -16.56) * mm});
            skLineSegment(sketch, "E829", {"start": v(-12.58, -16.56) * mm, "end": v(-12.62, -16.57) * mm});
            skLineSegment(sketch, "E830", {"start": v(-12.62, -16.57) * mm, "end": v(-12.66, -16.58) * mm});
            skLineSegment(sketch, "E831", {"start": v(-12.66, -16.58) * mm, "end": v(-12.7, -16.6) * mm});
            skLineSegment(sketch, "E832", {"start": v(-12.7, -16.6) * mm, "end": v(-12.75, -16.6) * mm});
            skLineSegment(sketch, "E833", {"start": v(-12.75, -16.6) * mm, "end": v(-12.8, -16.6) * mm});
            skLineSegment(sketch, "E834", {"start": v(-12.8, -16.6) * mm, "end": v(-12.84, -16.61) * mm});
            skLineSegment(sketch, "E835", {"start": v(-12.84, -16.61) * mm, "end": v(-12.88, -16.62) * mm});
            skLineSegment(sketch, "E836", {"start": v(-12.88, -16.62) * mm, "end": v(-12.92, -16.62) * mm});
            skLineSegment(sketch, "E837", {"start": v(-12.92, -16.62) * mm, "end": v(-12.97, -16.62) * mm});
            skLineSegment(sketch, "E838", {"start": v(-12.97, -16.62) * mm, "end": v(-13.01, -16.62) * mm});
            skLineSegment(sketch, "E839", {"start": v(-13.01, -16.62) * mm, "end": v(-13.05, -16.62) * mm});
            skLineSegment(sketch, "E840", {"start": v(-13.05, -16.62) * mm, "end": v(-13.1, -16.62) * mm});
            skLineSegment(sketch, "E841", {"start": v(-13.1, -16.62) * mm, "end": v(-13.14, -16.62) * mm});
            skLineSegment(sketch, "E842", {"start": v(-13.14, -16.62) * mm, "end": v(-13.19, -16.61) * mm});
            skLineSegment(sketch, "E843", {"start": v(-13.19, -16.61) * mm, "end": v(-13.23, -16.6) * mm});
            skLineSegment(sketch, "E844", {"start": v(-13.23, -16.6) * mm, "end": v(-13.27, -16.6) * mm});
            skLineSegment(sketch, "E845", {"start": v(-13.27, -16.6) * mm, "end": v(-13.32, -16.6) * mm});
            skLineSegment(sketch, "E846", {"start": v(-13.32, -16.6) * mm, "end": v(-13.36, -16.59) * mm});
            skLineSegment(sketch, "E847", {"start": v(-13.36, -16.59) * mm, "end": v(-13.4, -16.58) * mm});
            skLineSegment(sketch, "E848", {"start": v(-13.4, -16.58) * mm, "end": v(-13.44, -16.57) * mm});
            skLineSegment(sketch, "E849", {"start": v(-13.44, -16.57) * mm, "end": v(-13.63, -16.48) * mm});
            skLineSegment(sketch, "E850", {"start": v(-13.63, -16.48) * mm, "end": v(-13.67, -16.46) * mm});
            skLineSegment(sketch, "E851", {"start": v(-13.67, -16.46) * mm, "end": v(-13.7, -16.44) * mm});
            skLineSegment(sketch, "E852", {"start": v(-13.7, -16.44) * mm, "end": v(-13.72, -16.42) * mm});
            skLineSegment(sketch, "E853", {"start": v(-13.72, -16.42) * mm, "end": v(-13.74, -16.4) * mm});
            skLineSegment(sketch, "E854", {"start": v(-13.74, -16.4) * mm, "end": v(-13.74, -16.39) * mm});
            skLineSegment(sketch, "E855", {"start": v(-13.74, -16.39) * mm, "end": v(-13.75, -16.37) * mm});
            skLineSegment(sketch, "E856", {"start": v(-13.75, -16.37) * mm, "end": v(-13.76, -16.36) * mm});
            skLineSegment(sketch, "E857", {"start": v(-13.76, -16.36) * mm, "end": v(-13.76, -16.34) * mm});
            skLineSegment(sketch, "E858", {"start": v(-13.76, -16.34) * mm, "end": v(-13.77, -16.33) * mm});
            skLineSegment(sketch, "E859", {"start": v(-13.77, -16.33) * mm, "end": v(-13.77, -16.31) * mm});
            skLineSegment(sketch, "E860", {"start": v(-13.77, -16.31) * mm, "end": v(-13.78, -16.3) * mm});
            skLineSegment(sketch, "E861", {"start": v(-13.78, -16.3) * mm, "end": v(-13.8, -15.27) * mm});
            skFitSpline(sketch, "E862", {"points": [v(-16.09, 0.4) * mm, v(-16.48, 0.53) * mm, v(-16.87, 0.42) * mm], "startDerivative": vector(-0.77, 0.4) * mm, "endDerivative": vector(-0.8, -0.36) * mm});
            skFitSpline(sketch, "E863", {"points": [v(-9.68, -1.66) * mm, v(-8.41, -1.95) * mm, v(-8.04, -3.41) * mm], "startDerivative": vector(3.1, -0.07) * mm, "endDerivative": vector(0.22, -3.4) * mm});
            skLineSegment(sketch, "E864", {"start": v(-8.04, -3.41) * mm, "end": v(-8.04, -3.57) * mm});
            skLineSegment(sketch, "E865", {"start": v(-16.09, 0.4) * mm, "end": v(-15.75, 0.24) * mm});
            skLineSegment(sketch, "E866", {"start": v(-17.01, 0.36) * mm, "end": v(-16.87, 0.42) * mm});
            skLineSegment(sketch, "E867", {"start": v(-9.68, -1.66) * mm, "end": v(-9.7, 0.57) * mm});
            skLineSegment(sketch, "E868", {"start": v(-13.9, -1.75) * mm, "end": v(-16.26, -0.55) * mm});
            skFitSpline(sketch, "E869", {"points": [v(-16.26, -0.55) * mm, v(-16.5, -0.47) * mm, v(-16.83, -0.6) * mm], "startDerivative": vector(-0.52, 0.27) * mm, "endDerivative": vector(-0.63, -0.37) * mm});
            skFitSpline(sketch, "E870", {"points": [v(-9.4, -3.99) * mm, v(-9.18, -4.2) * mm, v(-9.85, -4.84) * mm], "startDerivative": vector(0.88, -0.52) * mm, "endDerivative": vector(-1.57, -1.12) * mm});
            skSolve(sketch);
        }
        {
            var Q0;
            Q0=qSketchRegion(id+"F27",true);
            extrude(context, id + "F28", {"entities" : qUnion([Q0]), "operationType" : NewBodyOperationType.ADD, "depth" : 26.5 * mm});
        }
        {
            var Q0;
            Q0=qSketchRegion(id+"F27",true);
            var Q1;
            {var subQ0=sQuery(id+"F0.wireOp",EDGE,"E7.rect.top");var subQ1=sQuery(id+"F0.wireOp",EDGE,"E7.rect.right");var subQ2=sQuery(id+"F0.wireOp",EDGE,"E7.rect.left");var subQ3=sQuery(id+"F0.wireOp",EDGE,"E7.rect.bottom");var subQ4=sQuery(id+"F0.wireOp",EDGE,"E5.MirrorC");var subQ5=sQuery(id+"F0.wireOp",EDGE,"E3");var subQ6=sQuery(id+"F0.wireOp",EDGE,"E2");var subQ7=sQuery(id+"F0.wireOp",EDGE,"E1");Q1=makeQuery(id+"F28.boolean.opBoolean","SPLIT",FACE,{"disambiguationData":[TD([makeQuery(id+"F28.opExtrude","SWEPT_FACE",FACE,{"disambiguationData":[OSD([sQuery(id+"F27.wireOp",EDGE,"E135")])]})])],"derivedFrom":makeQuery(id+"F6.opShell","OFFSET_FACE",FACE,{"disambiguationData":[OSD([subQ7,subQ6,subQ5,subQ4,subQ3,subQ0,subQ2,subQ1]),TDD([makeQuery(id+"F1.opExtrude","CAP_FACE",FACE,{"disambiguationData":[OSD([subQ7,subQ6,subQ5,subQ4,subQ3,subQ0,subQ2,subQ1])],"isStart":false})])]})});}
            extrude(context, id + "F29", {"entities" : qUnion([Q0]), "operationType" : NewBodyOperationType.REMOVE, "endBound" : BoundingType.UP_TO_SURFACE, "endBoundEntityFace" : qUnion([Q1]), "depth" : 23 * mm});
        }
        {
            var Q0;
            {var subQ0=sQuery(id+"F18.wireOp",EDGE,"E69");Q0=makeQuery(id+"F18.imprint","IMPRINT",FACE,{"disambiguationData":[TD([[makeQuery(id+"F18.imprint","IMPRINT",EDGE,{"derivedFrom":subQ0}),-1.0]])]});}
            extrude(context, id + "F30", {"entities" : qUnion([Q0]), "operationType" : NewBodyOperationType.REMOVE, "oppositeDirection" : true, "depth" : 2 * mm});
        }
        {
            var Q0;
            Q0=qCreatedBy(makeId("Top.planeOp"),FACE);
            var sketch = newSketch(context, id + "F31", { "sketchPlane" : qUnion([Q0])});
            skLineSegment(sketch, "E871.bottom", {"start": v(7.48, -5.58) * mm, "end": v(13.97, -5.58) * mm});
            skLineSegment(sketch, "E871.top", {"start": v(7.48, -5.2) * mm, "end": v(13.97, -5.2) * mm});
            skLineSegment(sketch, "E872.bottom", {"start": v(6.04, -5.58) * mm, "end": v(16.8, -5.58) * mm});
            skLineSegment(sketch, "E872.top", {"start": v(6.04, -5.2) * mm, "end": v(16.8, -5.2) * mm});
            skLineSegment(sketch, "E872.left", {"start": v(6.04, -5.58) * mm, "end": v(6.04, -5.2) * mm});
            skLineSegment(sketch, "E873", {"start": v(16.8, -5.2) * mm, "end": v(18.32, -5.2) * mm});
            skLineSegment(sketch, "E874", {"start": v(18.32, -5.2) * mm, "end": v(18.32, -5.58) * mm});
            skLineSegment(sketch, "E875", {"start": v(18.32, -5.58) * mm, "end": v(16.8, -5.58) * mm});
            skSolve(sketch);
        }
        {
            var Q0;
            Q0=qSketchRegion(id+"F31",true);
            var Q1;
            {var subQ1=sQuery(id+"F2.wireOp",EDGE,"E22");var subQ3=sQuery(id+"F2.wireOp",EDGE,"E20");Q1=makeQuery(id+"F24.boolean.opBoolean","SPLIT",FACE,{"disambiguationData":[TD([makeQuery(id+"F6.opShell","OFFSET_FACE",FACE,{"disambiguationData":[OSD([sQuery(id+"F0.wireOp",EDGE,"E3")])]})])],"derivedFrom":makeQuery(id+"F6.opShell","OFFSET_FACE",FACE,{"disambiguationData":[OSD([subQ3,subQ1])]})});}
            extrude(context, id + "F32", {"entities" : qUnion([Q0]), "operationType" : NewBodyOperationType.ADD, "endBound" : BoundingType.UP_TO_SURFACE, "endBoundEntityFace" : qUnion([Q1]), "depth" : 25 * mm});
        }
        {
            var Q0;
            {var subQ0=sQuery(id+"F0.wireOp",EDGE,"E7.rect.top");var subQ1=sQuery(id+"F0.wireOp",EDGE,"E7.rect.right");var subQ2=sQuery(id+"F0.wireOp",EDGE,"E7.rect.left");var subQ3=sQuery(id+"F0.wireOp",EDGE,"E7.rect.bottom");var subQ4=sQuery(id+"F0.wireOp",EDGE,"E5.MirrorC");var subQ5=sQuery(id+"F0.wireOp",EDGE,"E3");var subQ6=sQuery(id+"F0.wireOp",EDGE,"E2");var subQ7=sQuery(id+"F0.wireOp",EDGE,"E1");Q0=makeQuery(id+"F28.boolean.opBoolean","SPLIT",FACE,{"disambiguationData":[TD([makeQuery(id+"F4.opFillet","BLEND_FACE",FACE,{"disambiguationData":[OSD([subQ0])]})])],"derivedFrom":makeQuery(id+"F1.opExtrude","CAP_FACE",FACE,{"disambiguationData":[OSD([subQ7,subQ6,subQ5,subQ4,subQ3,subQ0,subQ2,subQ1])],"isStart":false})});}
            cPlane(context, id + "F33", {"entities" : qUnion([Q0]), "cplaneType" : CPlaneType.OFFSET, "offset" : 9 * mm, "oppositeDirection" : true, "width" : 150 * mm, "height" : 150 * mm});
        }
        {
            var Q0;
            Q0=qCreatedBy(id+"F33.planeOp",FACE);
            var sketch = newSketch(context, id + "F34", { "sketchPlane" : qUnion([Q0])});
            skCircle(sketch, "E876", {"center": v(-29.86, -30.9) * mm, "radius": 1.22 * mm});
            skCircle(sketch, "E877", {"center": v(-29.84, 14.65) * mm, "radius": 1.25 * mm});
            skSolve(sketch);
        }
        {
            var Q0;
            Q0=qSketchRegion(id+"F34",true);
            var Q1;
            Q1=makeQuery(id+"F3.boolean.opBoolean","COPY",FACE,{"derivedFrom":makeQuery(id+"F3.opExtrude","SWEPT_FACE",FACE,{"disambiguationData":[OSD([sQuery(id+"F2.wireOp",EDGE,"E14")])]})});
            extrude(context, id + "F35", {"entities" : qUnion([Q0]), "operationType" : NewBodyOperationType.ADD, "endBound" : BoundingType.UP_TO_SURFACE, "endBoundEntityFace" : qUnion([Q1]), "depth" : 25 * mm});
        }
        {
            var Q0;
            {var subQ0=sQuery(id+"F0.wireOp",EDGE,"E7.rect.right");var subQ1=sQuery(id+"F0.wireOp",EDGE,"E7.rect.left");var subQ2=sQuery(id+"F0.wireOp",EDGE,"E7.rect.top");var subQ3=sQuery(id+"F0.wireOp",EDGE,"E7.rect.bottom");var subQ4=sQuery(id+"F0.wireOp",EDGE,"E5.MirrorC");var subQ5=sQuery(id+"F0.wireOp",EDGE,"E3");var subQ6=sQuery(id+"F0.wireOp",EDGE,"E2");var subQ7=sQuery(id+"F0.wireOp",EDGE,"E1");Q0=makeQuery(id+"F28.boolean.opBoolean","SPLIT",FACE,{"disambiguationData":[TD([makeQuery(id+"F4.opFillet","BLEND_FACE",FACE,{"disambiguationData":[OSD([subQ3])]})])],"derivedFrom":makeQuery(id+"F1.opExtrude","CAP_FACE",FACE,{"disambiguationData":[OSD([subQ7,subQ6,subQ5,subQ4,subQ3,subQ2,subQ1,subQ0])],"isStart":false})});}
            cPlane(context, id + "F36", {"entities" : qUnion([Q0]), "cplaneType" : CPlaneType.OFFSET, "offset" : 17.5 * mm, "oppositeDirection" : true, "width" : 150 * mm, "height" : 150 * mm});
        }
        {
            var Q0;
            Q0=qCreatedBy(id+"F36.planeOp",FACE);
            var sketch = newSketch(context, id + "F37", { "sketchPlane" : qUnion([Q0])});
            skCircle(sketch, "E878", {"center": v(8.9, 3.98) * mm, "radius": 1.26 * mm});
            skCircle(sketch, "E879", {"center": v(15.8, -30.92) * mm, "radius": 1.17 * mm});
            skSolve(sketch);
        }
        {
            var Q0;
            Q0=qSketchRegion(id+"F37",true);
            var Q1;
            {var subQ0=sQuery(id+"F2.wireOp",EDGE,"E22");var subQ1=sQuery(id+"F2.wireOp",EDGE,"E20");Q1=makeQuery(id+"F24.boolean.opBoolean","SPLIT",FACE,{"disambiguationData":[TD([makeQuery(id+"F1.opExtrude","SWEPT_FACE",FACE,{"disambiguationData":[OSD([sQuery(id+"F0.wireOp",EDGE,"E3")])]})])],"derivedFrom":makeQuery(id+"F3.boolean.opBoolean","COPY",FACE,{"derivedFrom":makeQuery(id+"F3.opExtrude","SWEPT_FACE",FACE,{"disambiguationData":[OSD([subQ1,subQ0])]})})});}
            extrude(context, id + "F38", {"entities" : qUnion([Q0]), "operationType" : NewBodyOperationType.ADD, "endBound" : BoundingType.UP_TO_SURFACE, "endBoundEntityFace" : qUnion([Q1]), "depth" : 25 * mm});
        }
        {
            var Q0;
            Q0=makeQuery(id+"F1.opExtrude","SWEPT_FACE",FACE,{"disambiguationData":[OSD([sQuery(id+"F0.wireOp",EDGE,"E7.rect.bottom")])]});
            cPlane(context, id + "F39", {"entities" : qUnion([Q0]), "cplaneType" : CPlaneType.OFFSET, "offset" : 1.8 * mm, "oppositeDirection" : true, "width" : 150 * mm, "height" : 150 * mm});
        }
        {
            var Q0;
            Q0=qCreatedBy(id+"F39.planeOp",FACE);
            var sketch = newSketch(context, id + "F40", { "sketchPlane" : qUnion([Q0])});
            skLineSegment(sketch, "E880.top", {"start": v(-5.27, 0) * mm, "end": v(12.86, 0) * mm});
            skLineSegment(sketch, "E881.right", {"start": v(12.86, 5.48) * mm, "end": v(12.86, 0) * mm});
            skLineSegment(sketch, "E882.bottom", {"start": v(12.86, 0) * mm, "end": v(-5.27, 0) * mm});
            skLineSegment(sketch, "E882.top", {"start": v(12.86, 5.48) * mm, "end": v(-5.27, 5.48) * mm});
            skLineSegment(sketch, "E882.left", {"start": v(12.86, 0) * mm, "end": v(12.86, 5.48) * mm});
            skPoint(sketch, "E883.orphan", {"position": v(14.06, 0) * mm});
            skLineSegment(sketch, "E884", {"start": v(-5.27, 5.48) * mm, "end": v(-8, 5.48) * mm});
            skLineSegment(sketch, "E885", {"start": v(-8, 5.48) * mm, "end": v(-8, 0) * mm});
            skLineSegment(sketch, "E886", {"start": v(-8, 0) * mm, "end": v(-5.27, 0) * mm});
            skSolve(sketch);
        }
        {
            var Q0;
            Q0=qSketchRegion(id+"F40",true);
            extrude(context, id + "F41", {"entities" : qUnion([Q0]), "operationType" : NewBodyOperationType.REMOVE, "depth" : 1.2 * mm});
        }
        {
            var Q0;
            Q0=qCreatedBy(makeId("Top.planeOp"),FACE);
            var sketch = newSketch(context, id + "F42", { "sketchPlane" : qUnion([Q0])});
            skLineSegment(sketch, "E887.bottom", {"start": v(-10.2, -20.34) * mm, "end": v(-23.5, -20.34) * mm});
            skLineSegment(sketch, "E887.top", {"start": v(-9.76, -20.7) * mm, "end": v(-23.91, -20.7) * mm});
            skLineSegment(sketch, "E887.left", {"start": v(-9.76, -20.34) * mm, "end": v(-9.76, -20.7) * mm});
            skLineSegment(sketch, "E888", {"start": v(-9.76, -19.58) * mm, "end": v(-9.76, 2.28) * mm});
            skLineSegment(sketch, "E889.bottom", {"start": v(-10.2, 2.28) * mm, "end": v(-23.5, 2.28) * mm});
            skLineSegment(sketch, "E889.top", {"start": v(-9.76, 2.58) * mm, "end": v(-23.91, 2.58) * mm});
            skLineSegment(sketch, "E889.left", {"start": v(-9.76, 2.28) * mm, "end": v(-9.76, 2.58) * mm});
            skLineSegment(sketch, "E889.right", {"start": v(-23.91, 2.28) * mm, "end": v(-23.91, 2.58) * mm});
            skLineSegment(sketch, "E890.bottom", {"start": v(-10.2, -10.06) * mm, "end": v(-23.5, -10.06) * mm});
            skLineSegment(sketch, "E890.top", {"start": v(-10.2, -9.35) * mm, "end": v(-23.5, -9.35) * mm});
            skLineSegment(sketch, "E890.left", {"start": v(-9.76, -10.06) * mm, "end": v(-9.76, -9.35) * mm});
            skLineSegment(sketch, "E890.right", {"start": v(-25.9, -10.06) * mm, "end": v(-25.9, -9.35) * mm});
            skLineSegment(sketch, "E891", {"start": v(-10.2, -19.58) * mm, "end": v(-10.2, -10.06) * mm});
            skLineSegment(sketch, "E892.bottom", {"start": v(-23.91, 2.58) * mm, "end": v(-23.5, 2.58) * mm});
            skLineSegment(sketch, "E892.top", {"start": v(-23.91, -20.7) * mm, "end": v(-23.5, -20.7) * mm});
            skLineSegment(sketch, "E892.left", {"start": v(-23.91, 2.58) * mm, "end": v(-23.91, 2.28) * mm});
            skLineSegment(sketch, "E892.right", {"start": v(-23.5, 1.67) * mm, "end": v(-23.5, -9.35) * mm});
            skLineSegment(sketch, "E893.trimOffspring", {"start": v(-10.2, -9.35) * mm, "end": v(-10.2, 2.28) * mm});
            skLineSegment(sketch, "E894.trimOffspring", {"start": v(-23.91, -10.06) * mm, "end": v(-25.9, -10.06) * mm});
            skLineSegment(sketch, "E895.trimOffspring", {"start": v(-23.91, -10.06) * mm, "end": v(-23.91, -20.7) * mm});
            skLineSegment(sketch, "E896.trimOffspring", {"start": v(-23.5, -10.06) * mm, "end": v(-23.5, -20.34) * mm});
            skLineSegment(sketch, "E897.trimOffspring", {"start": v(-23.91, -9.35) * mm, "end": v(-25.9, -9.35) * mm});
            skLineSegment(sketch, "E898", {"start": v(-10.2, -19.58) * mm, "end": v(-9.76, -19.58) * mm});
            skLineSegment(sketch, "E899", {"start": v(-10.2, -20.34) * mm, "end": v(-9.76, -20.34) * mm});
            skLineSegment(sketch, "E900", {"start": v(-23.5, 2.28) * mm, "end": v(-23.91, 2.28) * mm});
            skLineSegment(sketch, "E901", {"start": v(-23.5, 1.67) * mm, "end": v(-23.91, 1.67) * mm});
            skLineSegment(sketch, "E902.trimOffspring", {"start": v(-23.91, 1.67) * mm, "end": v(-23.91, -9.35) * mm});
            skSolve(sketch);
        }
        {
            var Q0;
            Q0=qSketchRegion(id+"F42",true);
            var Q1;
            {var subQ0=sQuery(id+"F27.wireOp",EDGE,"E861");var subQ1=sQuery(id+"F27.wireOp",EDGE,"E860");var subQ2=sQuery(id+"F27.wireOp",EDGE,"E859");var subQ3=sQuery(id+"F27.wireOp",EDGE,"E858");var subQ4=sQuery(id+"F27.wireOp",EDGE,"E857");var subQ5=sQuery(id+"F27.wireOp",EDGE,"E856");var subQ6=sQuery(id+"F27.wireOp",EDGE,"E855");var subQ7=sQuery(id+"F27.wireOp",EDGE,"E854");var subQ8=sQuery(id+"F27.wireOp",EDGE,"E853");var subQ9=sQuery(id+"F27.wireOp",EDGE,"E852");var subQ10=sQuery(id+"F27.wireOp",EDGE,"E851");var subQ11=sQuery(id+"F27.wireOp",EDGE,"E850");var subQ12=sQuery(id+"F27.wireOp",EDGE,"E849");var subQ13=sQuery(id+"F27.wireOp",EDGE,"E848");var subQ14=sQuery(id+"F27.wireOp",EDGE,"E847");var subQ15=sQuery(id+"F27.wireOp",EDGE,"E846");var subQ16=sQuery(id+"F27.wireOp",EDGE,"E845");var subQ17=sQuery(id+"F27.wireOp",EDGE,"E844");var subQ18=sQuery(id+"F27.wireOp",EDGE,"E843");var subQ19=sQuery(id+"F27.wireOp",EDGE,"E842");var subQ20=sQuery(id+"F27.wireOp",EDGE,"E841");var subQ21=sQuery(id+"F27.wireOp",EDGE,"E840");var subQ22=sQuery(id+"F27.wireOp",EDGE,"E839");var subQ23=sQuery(id+"F27.wireOp",EDGE,"E838");var subQ24=sQuery(id+"F27.wireOp",EDGE,"E837");var subQ25=sQuery(id+"F27.wireOp",EDGE,"E836");var subQ26=sQuery(id+"F27.wireOp",EDGE,"E835");var subQ27=sQuery(id+"F27.wireOp",EDGE,"E834");var subQ28=sQuery(id+"F27.wireOp",EDGE,"E833");var subQ29=sQuery(id+"F27.wireOp",EDGE,"E832");var subQ30=sQuery(id+"F27.wireOp",EDGE,"E831");var subQ31=sQuery(id+"F27.wireOp",EDGE,"E830");var subQ32=sQuery(id+"F27.wireOp",EDGE,"E829");var subQ33=sQuery(id+"F27.wireOp",EDGE,"E828");var subQ34=sQuery(id+"F27.wireOp",EDGE,"E827");var subQ35=sQuery(id+"F27.wireOp",EDGE,"E826");var subQ36=sQuery(id+"F27.wireOp",EDGE,"E825");var subQ37=sQuery(id+"F27.wireOp",EDGE,"E824");var subQ38=sQuery(id+"F27.wireOp",EDGE,"E823");var subQ39=sQuery(id+"F27.wireOp",EDGE,"E822");var subQ40=sQuery(id+"F27.wireOp",EDGE,"E821");var subQ41=sQuery(id+"F27.wireOp",EDGE,"E820");var subQ42=sQuery(id+"F27.wireOp",EDGE,"E819");var subQ43=sQuery(id+"F27.wireOp",EDGE,"E818");var subQ44=sQuery(id+"F27.wireOp",EDGE,"E817");var subQ45=sQuery(id+"F27.wireOp",EDGE,"E816");var subQ46=sQuery(id+"F27.wireOp",EDGE,"E815");var subQ47=sQuery(id+"F27.wireOp",EDGE,"E814");var subQ48=sQuery(id+"F27.wireOp",EDGE,"E813");var subQ49=sQuery(id+"F27.wireOp",EDGE,"E812");var subQ50=sQuery(id+"F27.wireOp",EDGE,"E811");var subQ51=sQuery(id+"F27.wireOp",EDGE,"E810");var subQ52=sQuery(id+"F27.wireOp",EDGE,"E809");var subQ53=sQuery(id+"F27.wireOp",EDGE,"E808");var subQ54=sQuery(id+"F27.wireOp",EDGE,"E807");var subQ55=sQuery(id+"F27.wireOp",EDGE,"E806");var subQ56=sQuery(id+"F27.wireOp",EDGE,"E805");var subQ57=sQuery(id+"F27.wireOp",EDGE,"E804");var subQ58=sQuery(id+"F27.wireOp",EDGE,"E803");var subQ59=sQuery(id+"F27.wireOp",EDGE,"E802");var subQ60=sQuery(id+"F27.wireOp",EDGE,"E801");var subQ61=sQuery(id+"F27.wireOp",EDGE,"E800");var subQ62=sQuery(id+"F27.wireOp",EDGE,"E799");var subQ63=sQuery(id+"F27.wireOp",EDGE,"E798");var subQ64=sQuery(id+"F27.wireOp",EDGE,"E797");var subQ65=sQuery(id+"F27.wireOp",EDGE,"E796");var subQ66=sQuery(id+"F27.wireOp",EDGE,"E795");var subQ67=sQuery(id+"F27.wireOp",EDGE,"E794");var subQ68=sQuery(id+"F27.wireOp",EDGE,"E793");var subQ69=sQuery(id+"F27.wireOp",EDGE,"E792");var subQ70=sQuery(id+"F27.wireOp",EDGE,"E791");var subQ71=sQuery(id+"F27.wireOp",EDGE,"E790");var subQ72=sQuery(id+"F27.wireOp",EDGE,"E789");var subQ73=sQuery(id+"F27.wireOp",EDGE,"E788");var subQ74=sQuery(id+"F27.wireOp",EDGE,"E787");var subQ75=sQuery(id+"F27.wireOp",EDGE,"E786");var subQ76=sQuery(id+"F27.wireOp",EDGE,"E785");var subQ77=sQuery(id+"F27.wireOp",EDGE,"E784");var subQ78=sQuery(id+"F27.wireOp",EDGE,"E783");var subQ79=sQuery(id+"F27.wireOp",EDGE,"E782");var subQ80=sQuery(id+"F27.wireOp",EDGE,"E781");var subQ81=sQuery(id+"F27.wireOp",EDGE,"E780");var subQ82=sQuery(id+"F27.wireOp",EDGE,"E779");var subQ83=sQuery(id+"F27.wireOp",EDGE,"E778");var subQ84=sQuery(id+"F27.wireOp",EDGE,"E777");var subQ85=sQuery(id+"F27.wireOp",EDGE,"E776");var subQ86=sQuery(id+"F27.wireOp",EDGE,"E775");var subQ87=sQuery(id+"F27.wireOp",EDGE,"E774");var subQ88=sQuery(id+"F27.wireOp",EDGE,"E773");var subQ89=sQuery(id+"F27.wireOp",EDGE,"E772");var subQ90=sQuery(id+"F27.wireOp",EDGE,"E771");var subQ91=sQuery(id+"F27.wireOp",EDGE,"E770");var subQ92=sQuery(id+"F27.wireOp",EDGE,"E769");var subQ93=sQuery(id+"F27.wireOp",EDGE,"E768");var subQ94=sQuery(id+"F27.wireOp",EDGE,"E767");var subQ95=sQuery(id+"F27.wireOp",EDGE,"E766");var subQ96=sQuery(id+"F27.wireOp",EDGE,"E765");var subQ97=sQuery(id+"F27.wireOp",EDGE,"E764");var subQ98=sQuery(id+"F27.wireOp",EDGE,"E763");var subQ99=sQuery(id+"F27.wireOp",EDGE,"E762");var subQ100=sQuery(id+"F27.wireOp",EDGE,"E761");var subQ101=sQuery(id+"F27.wireOp",EDGE,"E760");var subQ102=sQuery(id+"F27.wireOp",EDGE,"E759");var subQ103=sQuery(id+"F27.wireOp",EDGE,"E758");var subQ104=sQuery(id+"F27.wireOp",EDGE,"E757");var subQ105=sQuery(id+"F27.wireOp",EDGE,"E756");var subQ106=sQuery(id+"F27.wireOp",EDGE,"E755");var subQ107=sQuery(id+"F27.wireOp",EDGE,"E754");var subQ108=sQuery(id+"F27.wireOp",EDGE,"E753");var subQ109=sQuery(id+"F27.wireOp",EDGE,"E752");var subQ110=sQuery(id+"F27.wireOp",EDGE,"E751");var subQ111=sQuery(id+"F27.wireOp",EDGE,"E750");var subQ112=sQuery(id+"F27.wireOp",EDGE,"E749");var subQ113=sQuery(id+"F27.wireOp",EDGE,"E748");var subQ114=sQuery(id+"F27.wireOp",EDGE,"E747");var subQ115=sQuery(id+"F27.wireOp",EDGE,"E746");var subQ116=sQuery(id+"F27.wireOp",EDGE,"E745");var subQ117=sQuery(id+"F27.wireOp",EDGE,"E744");var subQ118=sQuery(id+"F27.wireOp",EDGE,"E743");var subQ119=sQuery(id+"F27.wireOp",EDGE,"E742");var subQ120=sQuery(id+"F27.wireOp",EDGE,"E741");var subQ121=sQuery(id+"F27.wireOp",EDGE,"E740");var subQ122=sQuery(id+"F27.wireOp",EDGE,"E739");var subQ123=sQuery(id+"F27.wireOp",EDGE,"E738");var subQ124=sQuery(id+"F27.wireOp",EDGE,"E737");var subQ125=sQuery(id+"F27.wireOp",EDGE,"E736");var subQ126=sQuery(id+"F27.wireOp",EDGE,"E735");var subQ127=sQuery(id+"F27.wireOp",EDGE,"E734");var subQ128=sQuery(id+"F27.wireOp",EDGE,"E733");var subQ129=sQuery(id+"F27.wireOp",EDGE,"E732");var subQ130=sQuery(id+"F27.wireOp",EDGE,"E731");var subQ131=sQuery(id+"F27.wireOp",EDGE,"E730");var subQ132=sQuery(id+"F27.wireOp",EDGE,"E729");var subQ133=sQuery(id+"F27.wireOp",EDGE,"E728");var subQ134=sQuery(id+"F27.wireOp",EDGE,"E727");var subQ135=sQuery(id+"F27.wireOp",EDGE,"E726");var subQ136=sQuery(id+"F27.wireOp",EDGE,"E725");var subQ137=sQuery(id+"F27.wireOp",EDGE,"E724");var subQ138=sQuery(id+"F27.wireOp",EDGE,"E723");var subQ139=sQuery(id+"F27.wireOp",EDGE,"E722");var subQ140=sQuery(id+"F27.wireOp",EDGE,"E721");var subQ141=sQuery(id+"F27.wireOp",EDGE,"E720");var subQ142=sQuery(id+"F27.wireOp",EDGE,"E719");var subQ143=sQuery(id+"F27.wireOp",EDGE,"E718");var subQ144=sQuery(id+"F27.wireOp",EDGE,"E717");var subQ145=sQuery(id+"F27.wireOp",EDGE,"E716");var subQ146=sQuery(id+"F27.wireOp",EDGE,"E715");var subQ147=sQuery(id+"F27.wireOp",EDGE,"E714");var subQ148=sQuery(id+"F27.wireOp",EDGE,"E713");var subQ149=sQuery(id+"F27.wireOp",EDGE,"E712");var subQ150=sQuery(id+"F27.wireOp",EDGE,"E711");var subQ151=sQuery(id+"F27.wireOp",EDGE,"E710");var subQ152=sQuery(id+"F27.wireOp",EDGE,"E709");var subQ153=sQuery(id+"F27.wireOp",EDGE,"E708");var subQ154=sQuery(id+"F27.wireOp",EDGE,"E707");var subQ155=sQuery(id+"F27.wireOp",EDGE,"E706");var subQ156=sQuery(id+"F27.wireOp",EDGE,"E705");var subQ157=sQuery(id+"F27.wireOp",EDGE,"E704");var subQ158=sQuery(id+"F27.wireOp",EDGE,"E703");var subQ159=sQuery(id+"F27.wireOp",EDGE,"E702");var subQ160=sQuery(id+"F27.wireOp",EDGE,"E701");var subQ161=sQuery(id+"F27.wireOp",EDGE,"E700");var subQ162=sQuery(id+"F27.wireOp",EDGE,"E699");var subQ163=sQuery(id+"F27.wireOp",EDGE,"E698");var subQ164=sQuery(id+"F27.wireOp",EDGE,"E697");var subQ165=sQuery(id+"F27.wireOp",EDGE,"E696");var subQ166=sQuery(id+"F27.wireOp",EDGE,"E695");var subQ167=sQuery(id+"F27.wireOp",EDGE,"E694");var subQ168=sQuery(id+"F27.wireOp",EDGE,"E693");var subQ169=sQuery(id+"F27.wireOp",EDGE,"E692");var subQ170=sQuery(id+"F27.wireOp",EDGE,"E691");var subQ171=sQuery(id+"F27.wireOp",EDGE,"E690");var subQ172=sQuery(id+"F27.wireOp",EDGE,"E689");var subQ173=sQuery(id+"F27.wireOp",EDGE,"E688");var subQ174=sQuery(id+"F27.wireOp",EDGE,"E687");var subQ175=sQuery(id+"F27.wireOp",EDGE,"E686");var subQ176=sQuery(id+"F27.wireOp",EDGE,"E685");var subQ177=sQuery(id+"F27.wireOp",EDGE,"E684");var subQ178=sQuery(id+"F27.wireOp",EDGE,"E683");var subQ179=sQuery(id+"F27.wireOp",EDGE,"E682");var subQ180=sQuery(id+"F27.wireOp",EDGE,"E681");var subQ181=sQuery(id+"F27.wireOp",EDGE,"E680");var subQ182=sQuery(id+"F27.wireOp",EDGE,"E679");var subQ183=sQuery(id+"F27.wireOp",EDGE,"E678");var subQ184=sQuery(id+"F27.wireOp",EDGE,"E677");var subQ185=sQuery(id+"F27.wireOp",EDGE,"E676");var subQ186=sQuery(id+"F27.wireOp",EDGE,"E675");var subQ187=sQuery(id+"F27.wireOp",EDGE,"E674");var subQ188=sQuery(id+"F27.wireOp",EDGE,"E673");var subQ189=sQuery(id+"F27.wireOp",EDGE,"E672");var subQ190=sQuery(id+"F27.wireOp",EDGE,"E671");var subQ191=sQuery(id+"F27.wireOp",EDGE,"E670");var subQ192=sQuery(id+"F27.wireOp",EDGE,"E669");var subQ193=sQuery(id+"F27.wireOp",EDGE,"E668");var subQ194=sQuery(id+"F27.wireOp",EDGE,"E667");var subQ195=sQuery(id+"F27.wireOp",EDGE,"E870");var subQ196=sQuery(id+"F27.wireOp",EDGE,"E869");var subQ197=sQuery(id+"F27.wireOp",EDGE,"E868");var subQ198=sQuery(id+"F27.wireOp",EDGE,"E866");var subQ199=sQuery(id+"F27.wireOp",EDGE,"E865");var subQ200=sQuery(id+"F27.wireOp",EDGE,"E862");var subQ201=sQuery(id+"F27.wireOp",EDGE,"E337");var subQ202=sQuery(id+"F27.wireOp",EDGE,"E336");var subQ203=sQuery(id+"F27.wireOp",EDGE,"E335");var subQ204=sQuery(id+"F27.wireOp",EDGE,"E333");var subQ205=sQuery(id+"F27.wireOp",EDGE,"E332");var subQ206=sQuery(id+"F27.wireOp",EDGE,"E331");var subQ207=sQuery(id+"F27.wireOp",EDGE,"E330");var subQ208=sQuery(id+"F27.wireOp",EDGE,"E329");var subQ209=sQuery(id+"F27.wireOp",EDGE,"E328");var subQ210=sQuery(id+"F27.wireOp",EDGE,"E327");var subQ211=sQuery(id+"F27.wireOp",EDGE,"E326");var subQ212=sQuery(id+"F27.wireOp",EDGE,"E325");var subQ213=sQuery(id+"F27.wireOp",EDGE,"E324");var subQ214=sQuery(id+"F27.wireOp",EDGE,"E323");var subQ215=sQuery(id+"F27.wireOp",EDGE,"E322");var subQ216=sQuery(id+"F27.wireOp",EDGE,"E321");var subQ217=sQuery(id+"F27.wireOp",EDGE,"E320");var subQ218=sQuery(id+"F27.wireOp",EDGE,"E319");var subQ219=sQuery(id+"F27.wireOp",EDGE,"E318");var subQ220=sQuery(id+"F27.wireOp",EDGE,"E317");var subQ221=sQuery(id+"F27.wireOp",EDGE,"E316");var subQ222=sQuery(id+"F27.wireOp",EDGE,"E315");var subQ223=sQuery(id+"F27.wireOp",EDGE,"E314");var subQ224=sQuery(id+"F27.wireOp",EDGE,"E313");var subQ225=sQuery(id+"F27.wireOp",EDGE,"E312");var subQ226=sQuery(id+"F27.wireOp",EDGE,"E311");var subQ227=sQuery(id+"F27.wireOp",EDGE,"E310");var subQ228=sQuery(id+"F27.wireOp",EDGE,"E309");var subQ229=sQuery(id+"F27.wireOp",EDGE,"E308");var subQ230=sQuery(id+"F27.wireOp",EDGE,"E307");var subQ231=sQuery(id+"F27.wireOp",EDGE,"E306");var subQ232=sQuery(id+"F27.wireOp",EDGE,"E305");var subQ233=sQuery(id+"F27.wireOp",EDGE,"E304");var subQ234=sQuery(id+"F27.wireOp",EDGE,"E303");var subQ235=sQuery(id+"F27.wireOp",EDGE,"E302");var subQ236=sQuery(id+"F27.wireOp",EDGE,"E301");var subQ237=sQuery(id+"F27.wireOp",EDGE,"E300");var subQ238=sQuery(id+"F27.wireOp",EDGE,"E299");var subQ239=sQuery(id+"F27.wireOp",EDGE,"E298");var subQ240=sQuery(id+"F27.wireOp",EDGE,"E297");var subQ241=sQuery(id+"F27.wireOp",EDGE,"E296");var subQ242=sQuery(id+"F27.wireOp",EDGE,"E295");var subQ243=sQuery(id+"F27.wireOp",EDGE,"E294");var subQ244=sQuery(id+"F27.wireOp",EDGE,"E293");var subQ245=sQuery(id+"F27.wireOp",EDGE,"E292");var subQ246=sQuery(id+"F27.wireOp",EDGE,"E291");var subQ247=sQuery(id+"F27.wireOp",EDGE,"E290");var subQ248=sQuery(id+"F27.wireOp",EDGE,"E289");var subQ249=sQuery(id+"F27.wireOp",EDGE,"E288");var subQ250=sQuery(id+"F27.wireOp",EDGE,"E287");var subQ251=sQuery(id+"F27.wireOp",EDGE,"E286");var subQ252=sQuery(id+"F27.wireOp",EDGE,"E285");var subQ253=sQuery(id+"F27.wireOp",EDGE,"E284");var subQ254=sQuery(id+"F27.wireOp",EDGE,"E283");var subQ255=sQuery(id+"F27.wireOp",EDGE,"E282");var subQ256=sQuery(id+"F27.wireOp",EDGE,"E281");var subQ257=sQuery(id+"F27.wireOp",EDGE,"E280");var subQ258=sQuery(id+"F27.wireOp",EDGE,"E279");var subQ259=sQuery(id+"F27.wireOp",EDGE,"E278");var subQ260=sQuery(id+"F27.wireOp",EDGE,"E277");var subQ261=sQuery(id+"F27.wireOp",EDGE,"E276");var subQ262=sQuery(id+"F27.wireOp",EDGE,"E275");var subQ263=sQuery(id+"F27.wireOp",EDGE,"E274");var subQ264=sQuery(id+"F27.wireOp",EDGE,"E273");var subQ265=sQuery(id+"F27.wireOp",EDGE,"E272");var subQ266=sQuery(id+"F27.wireOp",EDGE,"E271");var subQ267=sQuery(id+"F27.wireOp",EDGE,"E270");var subQ268=sQuery(id+"F27.wireOp",EDGE,"E269");var subQ269=sQuery(id+"F27.wireOp",EDGE,"E268");var subQ270=sQuery(id+"F27.wireOp",EDGE,"E267");var subQ271=sQuery(id+"F27.wireOp",EDGE,"E266");var subQ272=sQuery(id+"F27.wireOp",EDGE,"E265");var subQ273=sQuery(id+"F27.wireOp",EDGE,"E264");var subQ274=sQuery(id+"F27.wireOp",EDGE,"E263");var subQ275=sQuery(id+"F27.wireOp",EDGE,"E262");var subQ276=sQuery(id+"F27.wireOp",EDGE,"E261");var subQ277=sQuery(id+"F27.wireOp",EDGE,"E260");var subQ278=sQuery(id+"F27.wireOp",EDGE,"E259");var subQ279=sQuery(id+"F27.wireOp",EDGE,"E258");var subQ280=sQuery(id+"F27.wireOp",EDGE,"E257");var subQ281=sQuery(id+"F27.wireOp",EDGE,"E256");var subQ282=sQuery(id+"F27.wireOp",EDGE,"E255");var subQ283=sQuery(id+"F27.wireOp",EDGE,"E254");var subQ284=sQuery(id+"F27.wireOp",EDGE,"E253");var subQ285=sQuery(id+"F27.wireOp",EDGE,"E194");var subQ286=sQuery(id+"F27.wireOp",EDGE,"E193");var subQ287=sQuery(id+"F27.wireOp",EDGE,"E192");var subQ288=sQuery(id+"F27.wireOp",EDGE,"E191");var subQ289=sQuery(id+"F27.wireOp",EDGE,"E190");var subQ290=sQuery(id+"F27.wireOp",EDGE,"E189");var subQ291=sQuery(id+"F27.wireOp",EDGE,"E188");var subQ292=sQuery(id+"F27.wireOp",EDGE,"E187");var subQ293=sQuery(id+"F27.wireOp",EDGE,"E186");var subQ294=sQuery(id+"F27.wireOp",EDGE,"E185");var subQ295=sQuery(id+"F27.wireOp",EDGE,"E184");var subQ296=sQuery(id+"F27.wireOp",EDGE,"E183");var subQ297=sQuery(id+"F27.wireOp",EDGE,"E182");var subQ298=sQuery(id+"F27.wireOp",EDGE,"E135");var subQ299=sQuery(id+"F0.wireOp",EDGE,"E7.rect.bottom");var subQ302=sQuery(id+"F0.wireOp",EDGE,"E7.rect.right");var subQ303=sQuery(id+"F0.wireOp",EDGE,"E7.rect.left");var subQ304=sQuery(id+"F0.wireOp",EDGE,"E7.rect.top");var subQ305=sQuery(id+"F0.wireOp",EDGE,"E5.MirrorC");var subQ306=sQuery(id+"F0.wireOp",EDGE,"E3");var subQ307=sQuery(id+"F0.wireOp",EDGE,"E2");var subQ308=sQuery(id+"F0.wireOp",EDGE,"E1");var subQ309=makeQuery(id+"F1.opExtrude","CAP_FACE",FACE,{"disambiguationData":[OSD([subQ308,subQ307,subQ306,subQ305,subQ299,subQ304,subQ303,subQ302])],"isStart":false});var subQ312=makeQuery(id+"F6.opShell","OFFSET_FACE",FACE,{"disambiguationData":[OSD([subQ308,subQ307,subQ306,subQ305,subQ299,subQ304,subQ303,subQ302]),TDD([subQ309])]});Q1=makeQuery(id+"F29.boolean.opBoolean","MERGE",FACE,{"derivedFrom":[makeQuery(id+"F28.boolean.opBoolean","SPLIT",FACE,{"disambiguationData":[TD([makeQuery(id+"F28.opExtrude","SWEPT_FACE",FACE,{"disambiguationData":[OSD([subQ298])]})])],"derivedFrom":subQ312}),makeQuery(id+"F28.boolean.opBoolean","SPLIT",FACE,{"disambiguationData":[TD([makeQuery(id+"F28.opExtrude","SWEPT_FACE",FACE,{"disambiguationData":[OSD([subQ262])]})])],"derivedFrom":subQ312}),makeQuery(id+"F28.boolean.opBoolean","SPLIT",FACE,{"disambiguationData":[TD([makeQuery(id+"F28.opExtrude","SWEPT_FACE",FACE,{"disambiguationData":[OSD([subQ297])]})])],"derivedFrom":subQ312}),makeQuery(id+"F29.opExtrude","CAP_FACE",FACE,{"disambiguationData":[OSD([subQ298,sQuery(id+"F27.wireOp",EDGE,"E136"),sQuery(id+"F27.wireOp",EDGE,"E137"),sQuery(id+"F27.wireOp",EDGE,"E138"),sQuery(id+"F27.wireOp",EDGE,"E139"),sQuery(id+"F27.wireOp",EDGE,"E140"),sQuery(id+"F27.wireOp",EDGE,"E141"),sQuery(id+"F27.wireOp",EDGE,"E142"),sQuery(id+"F27.wireOp",EDGE,"E143"),sQuery(id+"F27.wireOp",EDGE,"E144"),sQuery(id+"F27.wireOp",EDGE,"E145"),sQuery(id+"F27.wireOp",EDGE,"E146"),sQuery(id+"F27.wireOp",EDGE,"E147"),sQuery(id+"F27.wireOp",EDGE,"E148"),sQuery(id+"F27.wireOp",EDGE,"E149"),sQuery(id+"F27.wireOp",EDGE,"E150"),sQuery(id+"F27.wireOp",EDGE,"E151"),sQuery(id+"F27.wireOp",EDGE,"E152"),sQuery(id+"F27.wireOp",EDGE,"E153"),sQuery(id+"F27.wireOp",EDGE,"E154"),sQuery(id+"F27.wireOp",EDGE,"E155"),sQuery(id+"F27.wireOp",EDGE,"E156"),sQuery(id+"F27.wireOp",EDGE,"E157"),sQuery(id+"F27.wireOp",EDGE,"E158"),sQuery(id+"F27.wireOp",EDGE,"E159"),sQuery(id+"F27.wireOp",EDGE,"E160"),sQuery(id+"F27.wireOp",EDGE,"E161"),sQuery(id+"F27.wireOp",EDGE,"E162"),sQuery(id+"F27.wireOp",EDGE,"E163"),sQuery(id+"F27.wireOp",EDGE,"E164"),sQuery(id+"F27.wireOp",EDGE,"E165"),sQuery(id+"F27.wireOp",EDGE,"E166"),sQuery(id+"F27.wireOp",EDGE,"E167"),sQuery(id+"F27.wireOp",EDGE,"E168"),sQuery(id+"F27.wireOp",EDGE,"E169"),sQuery(id+"F27.wireOp",EDGE,"E170"),sQuery(id+"F27.wireOp",EDGE,"E171"),sQuery(id+"F27.wireOp",EDGE,"E172"),sQuery(id+"F27.wireOp",EDGE,"E173"),sQuery(id+"F27.wireOp",EDGE,"E174"),sQuery(id+"F27.wireOp",EDGE,"E175"),sQuery(id+"F27.wireOp",EDGE,"E176"),sQuery(id+"F27.wireOp",EDGE,"E177"),sQuery(id+"F27.wireOp",EDGE,"E178"),sQuery(id+"F27.wireOp",EDGE,"E179"),sQuery(id+"F27.wireOp",EDGE,"E180"),sQuery(id+"F27.wireOp",EDGE,"E181"),subQ297,subQ296,subQ295,subQ294,subQ293,subQ292,subQ291,subQ290,subQ289,subQ288,subQ287,subQ286,subQ285,sQuery(id+"F27.wireOp",EDGE,"E195"),sQuery(id+"F27.wireOp",EDGE,"E196"),sQuery(id+"F27.wireOp",EDGE,"E197"),sQuery(id+"F27.wireOp",EDGE,"E198"),sQuery(id+"F27.wireOp",EDGE,"E199"),sQuery(id+"F27.wireOp",EDGE,"E200"),sQuery(id+"F27.wireOp",EDGE,"E201"),sQuery(id+"F27.wireOp",EDGE,"E202"),sQuery(id+"F27.wireOp",EDGE,"E203"),sQuery(id+"F27.wireOp",EDGE,"E204"),sQuery(id+"F27.wireOp",EDGE,"E205"),sQuery(id+"F27.wireOp",EDGE,"E206"),sQuery(id+"F27.wireOp",EDGE,"E207"),sQuery(id+"F27.wireOp",EDGE,"E208"),sQuery(id+"F27.wireOp",EDGE,"E209"),sQuery(id+"F27.wireOp",EDGE,"E210"),sQuery(id+"F27.wireOp",EDGE,"E211"),sQuery(id+"F27.wireOp",EDGE,"E212"),sQuery(id+"F27.wireOp",EDGE,"E213"),sQuery(id+"F27.wireOp",EDGE,"E214"),sQuery(id+"F27.wireOp",EDGE,"E215"),sQuery(id+"F27.wireOp",EDGE,"E216"),sQuery(id+"F27.wireOp",EDGE,"E217"),sQuery(id+"F27.wireOp",EDGE,"E218"),sQuery(id+"F27.wireOp",EDGE,"E219"),sQuery(id+"F27.wireOp",EDGE,"E220"),sQuery(id+"F27.wireOp",EDGE,"E221"),sQuery(id+"F27.wireOp",EDGE,"E222"),sQuery(id+"F27.wireOp",EDGE,"E223"),sQuery(id+"F27.wireOp",EDGE,"E224"),sQuery(id+"F27.wireOp",EDGE,"E225"),sQuery(id+"F27.wireOp",EDGE,"E226"),sQuery(id+"F27.wireOp",EDGE,"E227"),sQuery(id+"F27.wireOp",EDGE,"E228"),sQuery(id+"F27.wireOp",EDGE,"E229"),sQuery(id+"F27.wireOp",EDGE,"E230"),sQuery(id+"F27.wireOp",EDGE,"E231"),sQuery(id+"F27.wireOp",EDGE,"E232"),sQuery(id+"F27.wireOp",EDGE,"E233"),sQuery(id+"F27.wireOp",EDGE,"E234"),sQuery(id+"F27.wireOp",EDGE,"E235"),sQuery(id+"F27.wireOp",EDGE,"E236"),sQuery(id+"F27.wireOp",EDGE,"E237"),sQuery(id+"F27.wireOp",EDGE,"E238"),sQuery(id+"F27.wireOp",EDGE,"E239"),sQuery(id+"F27.wireOp",EDGE,"E240"),sQuery(id+"F27.wireOp",EDGE,"E241"),sQuery(id+"F27.wireOp",EDGE,"E242"),sQuery(id+"F27.wireOp",EDGE,"E243"),sQuery(id+"F27.wireOp",EDGE,"E244"),sQuery(id+"F27.wireOp",EDGE,"E245"),sQuery(id+"F27.wireOp",EDGE,"E246"),sQuery(id+"F27.wireOp",EDGE,"E247"),sQuery(id+"F27.wireOp",EDGE,"E248"),sQuery(id+"F27.wireOp",EDGE,"E249"),sQuery(id+"F27.wireOp",EDGE,"E250"),sQuery(id+"F27.wireOp",EDGE,"E251"),sQuery(id+"F27.wireOp",EDGE,"E252"),subQ284,subQ283,subQ282,subQ281,subQ280,subQ279,subQ278,subQ277,subQ276,subQ275,subQ274,subQ273,subQ272,subQ271,subQ270,subQ269,subQ268,subQ267,subQ266,subQ265,subQ264,subQ263,subQ262,subQ261,subQ260,subQ259,subQ258,subQ257,subQ256,subQ255,subQ254,subQ253,subQ252,subQ251,subQ250,subQ249,subQ248,subQ247,subQ246,subQ245,subQ244,subQ243,subQ242,subQ241,subQ240,subQ239,subQ238,subQ237,subQ236,subQ235,subQ234,subQ233,subQ232,subQ231,subQ230,subQ229,subQ228,subQ227,subQ226,subQ225,subQ224,subQ223,subQ222,subQ221,subQ220,subQ219,subQ218,subQ217,subQ216,subQ215,subQ214,subQ213,subQ212,subQ211,subQ210,subQ209,subQ208,subQ207,subQ206,subQ205,subQ204,sQuery(id+"F27.wireOp",EDGE,"E334"),subQ203,subQ202,subQ201,subQ200,sQuery(id+"F27.wireOp",EDGE,"E863"),sQuery(id+"F27.wireOp",EDGE,"E864"),subQ199,subQ198,sQuery(id+"F27.wireOp",EDGE,"E867"),subQ197,subQ196,subQ195])],"isStart":false}),makeQuery(id+"F29.opExtrude","CAP_FACE",FACE,{"disambiguationData":[OSD([subQ194,subQ193,subQ192,subQ191,subQ190,subQ189,subQ188,subQ187,subQ186,subQ185,subQ184,subQ183,subQ182,subQ181,subQ180,subQ179,subQ178,subQ177,subQ176,subQ175,subQ174,subQ173,subQ172,subQ171,subQ170,subQ169,subQ168,subQ167,subQ166,subQ165,subQ164,subQ163,subQ162,subQ161,subQ160,subQ159,subQ158,subQ157,subQ156,subQ155,subQ154,subQ153,subQ152,subQ151,subQ150,subQ149])],"isStart":false}),makeQuery(id+"F29.opExtrude","CAP_FACE",FACE,{"disambiguationData":[OSD([subQ148,subQ147,subQ146,subQ145,subQ144,subQ143,subQ142,subQ141,subQ140,subQ139,subQ138,subQ137,subQ136,subQ135,subQ134,subQ133,subQ132,subQ131,subQ130,subQ129,subQ128,subQ127,subQ126,subQ125,subQ124,subQ123,subQ122,subQ121,subQ120,subQ119,subQ118,subQ117,subQ116,subQ115,subQ114,subQ113,subQ112,subQ111,subQ110,subQ109,subQ108,subQ107,subQ106,subQ105,subQ104,subQ103,subQ102,subQ101,subQ100])],"isStart":false}),makeQuery(id+"F29.opExtrude","CAP_FACE",FACE,{"disambiguationData":[OSD([subQ99,subQ98,subQ97,subQ96,subQ95,subQ94,subQ93,subQ92,subQ91,subQ90,subQ89,subQ88,subQ87,subQ86,subQ85,subQ84,subQ83,subQ82,subQ81,subQ80,subQ79,subQ78,subQ77,subQ76,subQ75,subQ74,subQ73,subQ72,subQ71,subQ70,subQ69,subQ68,subQ67,subQ66,subQ65,subQ64,subQ63,subQ62,subQ61,subQ60,subQ59,subQ58,subQ57,subQ56,subQ55,subQ54,subQ53,subQ52,subQ51,subQ50,subQ49,subQ48,subQ47,subQ46,subQ45,subQ44])],"isStart":false}),makeQuery(id+"F29.opExtrude","CAP_FACE",FACE,{"disambiguationData":[OSD([subQ43,subQ42,subQ41,subQ40,subQ39,subQ38,subQ37,subQ36,subQ35,subQ34,subQ33,subQ32,subQ31,subQ30,subQ29,subQ28,subQ27,subQ26,subQ25,subQ24,subQ23,subQ22,subQ21,subQ20,subQ19,subQ18,subQ17,subQ16,subQ15,subQ14,subQ13,subQ12,subQ11,subQ10,subQ9,subQ8,subQ7,subQ6,subQ5,subQ4,subQ3,subQ2,subQ1,subQ0])],"isStart":false})]});}
            extrude(context, id + "F43", {"entities" : qUnion([Q0]), "operationType" : NewBodyOperationType.ADD, "endBound" : BoundingType.UP_TO_SURFACE, "endBoundEntityFace" : qUnion([Q1]), "depth" : 25 * mm});
        }
        {
            var Q0;
            {var subQ0=sQuery(id+"F0.wireOp",EDGE,"E7.rect.right");var subQ2=sQuery(id+"F0.wireOp",EDGE,"E7.rect.bottom");var subQ3=makeQuery(id+"F1.opExtrude","SWEPT_FACE",FACE,{"disambiguationData":[OSD([subQ2])]});var subQ8=sQuery(id+"F0.wireOp",EDGE,"E7.rect.left");var subQ17=sQuery(id+"F0.wireOp",EDGE,"E7.rect.top");var subQ19=sQuery(id+"F0.wireOp",EDGE,"E5.MirrorC");var subQ20=sQuery(id+"F0.wireOp",EDGE,"E3");var subQ21=sQuery(id+"F0.wireOp",EDGE,"E2");var subQ22=sQuery(id+"F0.wireOp",EDGE,"E1");var subQ23=makeQuery(id+"F1.opExtrude","CAP_FACE",FACE,{"disambiguationData":[OSD([subQ22,subQ21,subQ20,subQ19,subQ2,subQ17,subQ8,subQ0])],"isStart":true});Q0=makeQuery(id+"F26.boolean.opBoolean","MERGE",FACE,{"derivedFrom":[makeQuery(id+"F6.opShell","OFFSET_FACE",FACE,{"disambiguationData":[OSD([subQ22,subQ21,subQ20,subQ19,subQ2,subQ17,subQ8,subQ0]),TDD([subQ23]),OD(2.0)]}),makeQuery(id+"F14.boolean.opBoolean","SPLIT",FACE,{"disambiguationData":[TD([makeQuery(id+"F1.opExtrude","SWEPT_FACE",FACE,{"disambiguationData":[OSD([subQ22])]})])],"derivedFrom":makeQuery(id+"F6.opShell","OFFSET_FACE",FACE,{"disambiguationData":[OSD([subQ22,subQ21,subQ20,subQ19,subQ2,subQ17,subQ8,subQ0]),TDD([subQ23]),OD(0.0)]})}),makeQuery(id+"F14.boolean.opBoolean","SPLIT",FACE,{"disambiguationData":[TD([subQ3])],"derivedFrom":makeQuery(id+"F10.boolean.opBoolean","SPLIT",FACE,{"disambiguationData":[TD([subQ3])],"derivedFrom":makeQuery(id+"F6.opShell","OFFSET_FACE",FACE,{"disambiguationData":[OSD([subQ22,subQ21,subQ20,subQ19,subQ2,subQ17,subQ8,subQ0]),TDD([subQ23]),OD(3.0)]})})}),makeQuery(id+"F26.opExtrude","CAP_FACE",FACE,{"disambiguationData":[OSD([sQuery(id+"F25.wireOp",EDGE,"E114.top"),sQuery(id+"F25.wireOp",EDGE,"E114.left"),sQuery(id+"F25.wireOp",EDGE,"E114.right"),sQuery(id+"F25.wireOp",EDGE,"E115.bottom"),sQuery(id+"F25.wireOp",EDGE,"E115.top"),sQuery(id+"F25.wireOp",EDGE,"E115.right"),sQuery(id+"F25.wireOp",EDGE,"E114.bottom"),sQuery(id+"F25.wireOp",EDGE,"E119.top"),sQuery(id+"F25.wireOp",EDGE,"E119.left"),sQuery(id+"F25.wireOp",EDGE,"E119.right")])],"isStart":true}),makeQuery(id+"F26.opExtrude","CAP_FACE",FACE,{"disambiguationData":[OSD([sQuery(id+"F25.wireOp",EDGE,"E117.bottom"),sQuery(id+"F25.wireOp",EDGE,"E117.top"),sQuery(id+"F25.wireOp",EDGE,"E117.left"),sQuery(id+"F25.wireOp",EDGE,"E117.right"),sQuery(id+"F25.wireOp",EDGE,"E118.bottom"),sQuery(id+"F25.wireOp",EDGE,"E118.top"),sQuery(id+"F25.wireOp",EDGE,"E118.right")])],"isStart":true})]});}
            cPlane(context, id + "F44", {"entities" : qUnion([Q0]), "cplaneType" : CPlaneType.OFFSET, "offset" : 0.6 * mm, "oppositeDirection" : true, "width" : 150 * mm, "height" : 150 * mm});
        }
        {
            var Q0;
            Q0=qCreatedBy(id+"F44.planeOp",FACE);
            var sketch = newSketch(context, id + "F45", { "sketchPlane" : qUnion([Q0])});
            skLineSegment(sketch, "E903.bottom", {"start": v(-24.07, 22.32) * mm, "end": v(-9.14, 22.32) * mm});
            skLineSegment(sketch, "E903.top", {"start": v(-24.07, -4.65) * mm, "end": v(-9.14, -4.65) * mm});
            skLineSegment(sketch, "E903.left", {"start": v(-24.07, 22.32) * mm, "end": v(-24.07, -4.65) * mm});
            skLineSegment(sketch, "E903.right", {"start": v(-9.14, 22.32) * mm, "end": v(-9.14, -4.65) * mm});
            skSolve(sketch);
        }
        {
            var Q0;
            Q0=qSketchRegion(id+"F45",true);
            extrude(context, id + "F46", {"entities" : qUnion([Q0]), "operationType" : NewBodyOperationType.ADD, "depth" : 0.6 * mm});
        }
        {
            var Q0;
            Q0=qCreatedBy(makeId("Top.planeOp"),FACE);
            var sketch = newSketch(context, id + "F47", { "sketchPlane" : qUnion([Q0])});
            skLineSegment(sketch, "E904.bottom", {"start": v(-32.16, -19.74) * mm, "end": v(-31.86, -19.74) * mm});
            skLineSegment(sketch, "E904.top", {"start": v(-32.16, -29.43) * mm, "end": v(-31.86, -29.43) * mm});
            skLineSegment(sketch, "E904.left", {"start": v(-32.16, -19.74) * mm, "end": v(-32.16, -29.43) * mm});
            skLineSegment(sketch, "E904.right", {"start": v(-31.86, -19.74) * mm, "end": v(-31.86, -29.43) * mm});
            skLineSegment(sketch, "E905.bottom", {"start": v(-34.1, 3.13) * mm, "end": v(-31.72, 3.13) * mm});
            skLineSegment(sketch, "E905.top", {"start": v(-34.1, 0.35) * mm, "end": v(-31.72, 0.35) * mm});
            skLineSegment(sketch, "E905.left", {"start": v(-34.1, 3.13) * mm, "end": v(-34.1, 0.35) * mm});
            skLineSegment(sketch, "E905.right", {"start": v(-31.72, 3.13) * mm, "end": v(-31.72, 0.35) * mm});
            skLineSegment(sketch, "E906.bottom", {"start": v(-34.13, -7.9) * mm, "end": v(-31.72, -7.9) * mm});
            skLineSegment(sketch, "E906.top", {"start": v(-34.13, -10.8) * mm, "end": v(-31.72, -10.8) * mm});
            skLineSegment(sketch, "E906.left", {"start": v(-34.13, -7.9) * mm, "end": v(-34.13, -10.8) * mm});
            skLineSegment(sketch, "E906.right", {"start": v(-31.72, -7.9) * mm, "end": v(-31.72, -10.8) * mm});
            skLineSegment(sketch, "E907", {"start": v(-33.4, -10.8) * mm, "end": v(-33.4, -7.9) * mm});
            skLineSegment(sketch, "E908", {"start": v(-33.2, 3.13) * mm, "end": v(-33.2, 0.35) * mm});
            skLineSegment(sketch, "E909.trimOffspring", {"start": v(-33.4, 0.35) * mm, "end": v(-33.4, 3.13) * mm});
            skLineSegment(sketch, "E910.trimOffspring", {"start": v(-33.2, -7.9) * mm, "end": v(-33.2, -10.8) * mm});
            skSolve(sketch);
        }
        {
            var Q0;
            {var subQ0=sQuery(id+"F47.wireOp",EDGE,"E905.left");Q0=makeQuery(id+"F47.imprint","IMPRINT",FACE,{"disambiguationData":[TD([[makeQuery(id+"F47.imprint","IMPRINT",EDGE,{"derivedFrom":subQ0}),1.0]])]});}
            var Q1;
            {var subQ0=sQuery(id+"F47.wireOp",EDGE,"E905.right");Q1=makeQuery(id+"F47.imprint","IMPRINT",FACE,{"disambiguationData":[TD([[makeQuery(id+"F47.imprint","IMPRINT",EDGE,{"derivedFrom":subQ0}),-1.0]])]});}
            var Q2;
            {var subQ0=sQuery(id+"F47.wireOp",EDGE,"E906.left");Q2=makeQuery(id+"F47.imprint","IMPRINT",FACE,{"disambiguationData":[TD([[makeQuery(id+"F47.imprint","IMPRINT",EDGE,{"derivedFrom":subQ0}),1.0]])]});}
            var Q3;
            {var subQ0=sQuery(id+"F47.wireOp",EDGE,"E906.right");Q3=makeQuery(id+"F47.imprint","IMPRINT",FACE,{"disambiguationData":[TD([[makeQuery(id+"F47.imprint","IMPRINT",EDGE,{"derivedFrom":subQ0}),-1.0]])]});}
            var Q4;
            {var subQ0=sQuery(id+"F12.wireOp",EDGE,"E33.top");Q4=makeQuery(id+"F14.boolean.opBoolean","MERGE",FACE,{"derivedFrom":[makeQuery(id+"F13.boolean.opBoolean","COPY",FACE,{"derivedFrom":makeQuery(id+"F13.opExtrude","SWEPT_FACE",FACE,{"disambiguationData":[OSD([subQ0,sQuery(id+"F12.wireOp",EDGE,"E44.trimOffspring"),sQuery(id+"F12.wireOp",EDGE,"E52")])]})}),makeQuery(id+"F14.opExtrude","SWEPT_FACE",FACE,{"disambiguationData":[OSD([subQ0])]})]});}
            extrude(context, id + "F48", {"entities" : qUnion([Q0, Q1, Q2, Q3]), "operationType" : NewBodyOperationType.REMOVE, "endBoundEntityFace" : qUnion([Q4]), "depth" : 6.35 * mm});
        }
        {
            var Q0;
            Q0=makeQuery(id+"F47.imprint","IMPRINT",FACE,{"disambiguationData":[TD([[makeQuery(id+"F47.imprint","IMPRINT",EDGE,{"derivedFrom":sQuery(id+"F47.wireOp",EDGE,"E904.bottom")}),-1.0]])]});
            var Q1;
            Q1=makeQuery(id+"F16.boolean.opBoolean","MERGE",FACE,{"derivedFrom":[makeQuery(id+"F14.boolean.opBoolean","COPY",FACE,{"derivedFrom":makeQuery(id+"F14.opExtrude","SWEPT_FACE",FACE,{"disambiguationData":[OSD([sQuery(id+"F12.wireOp",EDGE,"E39"),sQuery(id+"F12.wireOp",EDGE,"E56")])]})}),makeQuery(id+"F16.opExtrude","CAP_FACE",FACE,{"disambiguationData":[OSD([sQuery(id+"F15.wireOp",EDGE,"E62.bottom"),sQuery(id+"F15.wireOp",EDGE,"E62.left"),sQuery(id+"F15.wireOp",EDGE,"E62.right"),sQuery(id+"F15.wireOp",EDGE,"E64")])],"isStart":false})]});
            extrude(context, id + "F49", {"entities" : qUnion([Q0]), "operationType" : NewBodyOperationType.ADD, "endBound" : BoundingType.UP_TO_SURFACE, "endBoundEntityFace" : qUnion([Q1]), "depth" : 25 * mm});
        }
        {
            var Q0;
            Q0=makeQuery(id+"F35.boolean.opBoolean","MERGE",FACE,{"derivedFrom":[makeQuery(id+"F3.boolean.opBoolean","COPY",FACE,{"derivedFrom":makeQuery(id+"F3.opExtrude","SWEPT_FACE",FACE,{"disambiguationData":[OSD([sQuery(id+"F2.wireOp",EDGE,"E14")])]})}),makeQuery(id+"F35.opExtrude","CAP_FACE",FACE,{"disambiguationData":[OSD([sQuery(id+"F34.wireOp",EDGE,"E876")])],"isStart":false}),makeQuery(id+"F35.opExtrude","CAP_FACE",FACE,{"disambiguationData":[OSD([sQuery(id+"F34.wireOp",EDGE,"E877")])],"isStart":false})]});
            var sketch = newSketch(context, id + "F50", { "sketchPlane" : qUnion([Q0])});
            skText(sketch, "E911", { "text": "12v", "fontName": "OpenSans-Bold.ttf"});
            skText(sketch, "E912", { "text": "L3 L2 L1", "fontName": "OpenSans-Bold.ttf"});
            const initialGuessF50  = {"E911": [0.01715, 0.00103, 1, 0, 0.00547], "E912": [-0.01124, -0.00554, 1, 0, 0.00554]};
            skSetInitialGuess(sketch, initialGuessF50);
            skSolve(sketch);
        }
        {
            var Q0;
            Q0=qSketchRegion(id+"F50",true);
            extrude(context, id + "F51", {"entities" : qUnion([Q0]), "operationType" : NewBodyOperationType.REMOVE, "oppositeDirection" : true, "depth" : 0.9 * mm});
        }
        {
            var Q0;
            {var subQ1=sQuery(id+"F0.wireOp",EDGE,"E7.rect.top");var subQ2=sQuery(id+"F0.wireOp",EDGE,"E7.rect.right");var subQ9=makeQuery(id+"F1.opExtrude","SWEPT_FACE",FACE,{"disambiguationData":[OSD([subQ1])]});Q0=makeQuery(id+"F19.boolean.opBoolean","SPLIT",FACE,{"disambiguationData":[TD([makeQuery(id+"F1.opExtrude","SWEPT_FACE",FACE,{"disambiguationData":[OSD([subQ2])]})])],"derivedFrom":subQ9});}
            var sketch = newSketch(context, id + "F52", { "sketchPlane" : qUnion([Q0])});
            skText(sketch, "E913", { "text": "S2", "fontName": "OpenSans-Bold.ttf"});
            skText(sketch, "E914", { "text": "S3", "fontName": "OpenSans-Bold.ttf"});
            skText(sketch, "E915", { "text": "S1", "fontName": "OpenSans-Bold.ttf"});
            const initialGuessF52  = {"E913": [0.00543, 0.00629, 1, 0, 0.005], "E914": [-0.0147, 0.00046, 1, 0, 0.005], "E915": [0.02787, 0.00057, 1, 0, 0.005]};
            skSetInitialGuess(sketch, initialGuessF52);
            skSolve(sketch);
        }
        {
            var Q0;
            Q0=qSketchRegion(id+"F52",true);
            extrude(context, id + "F53", {"entities" : qUnion([Q0]), "operationType" : NewBodyOperationType.REMOVE, "depth" : 1 * mm, "hasSecondDirection" : true, "secondDirectionOppositeDirection" : true, "secondDirectionDepth" : 1 * mm});
        }
        {
            var Q0;
            {var subQ0=sQuery(id+"F2.wireOp",EDGE,"E22");var subQ1=sQuery(id+"F2.wireOp",EDGE,"E20");Q0=makeQuery(id+"F38.boolean.opBoolean","MERGE",FACE,{"derivedFrom":[makeQuery(id+"F24.boolean.opBoolean","SPLIT",FACE,{"disambiguationData":[TD([makeQuery(id+"F1.opExtrude","SWEPT_FACE",FACE,{"disambiguationData":[OSD([sQuery(id+"F0.wireOp",EDGE,"E3")])]})])],"derivedFrom":makeQuery(id+"F3.boolean.opBoolean","COPY",FACE,{"derivedFrom":makeQuery(id+"F3.opExtrude","SWEPT_FACE",FACE,{"disambiguationData":[OSD([subQ1,subQ0])]})})}),makeQuery(id+"F38.opExtrude","CAP_FACE",FACE,{"disambiguationData":[OSD([sQuery(id+"F37.wireOp",EDGE,"E878")])],"isStart":false}),makeQuery(id+"F38.opExtrude","CAP_FACE",FACE,{"disambiguationData":[OSD([sQuery(id+"F37.wireOp",EDGE,"E879")])],"isStart":false})]});}
            var sketch = newSketch(context, id + "F54", { "sketchPlane" : qUnion([Q0])});
            skText(sketch, "E916", { "text": "S6", "fontName": "OpenSans-Bold.ttf"});
            const initialGuessF54  = {"E916": [0.00536, -0.02288, 1, 0, 0.005]};
            skSetInitialGuess(sketch, initialGuessF54);
            skSolve(sketch);
        }
        {
            var Q0;
            Q0=qSketchRegion(id+"F54",true);
            var Q1;
            Q1=makeQuery(id+"F4.opFillet","BLEND_FACE",FACE,{"disambiguationData":[OSD([sQuery(id+"F0.wireOp",EDGE,"E7.rect.left"),sQuery(id+"F2.wireOp",EDGE,"E20"),sQuery(id+"F2.wireOp",EDGE,"E22")])]});
            extrude(context, id + "F55", {"entities" : qUnion([Q0]), "operationType" : NewBodyOperationType.REMOVE, "oppositeDirection" : true, "depth" : 1 * mm});
        }
        {
            var Q0;
            {var subQ1=sQuery(id+"F0.wireOp",EDGE,"E7.rect.left");var subQ3=sQuery(id+"F0.wireOp",EDGE,"E7.rect.bottom");Q0=makeQuery(id+"F9.boolean.opBoolean","SPLIT",FACE,{"disambiguationData":[TD([makeQuery(id+"F1.opExtrude","SWEPT_FACE",FACE,{"disambiguationData":[OSD([subQ3])]})])],"derivedFrom":makeQuery(id+"F1.opExtrude","SWEPT_FACE",FACE,{"disambiguationData":[OSD([subQ1])]})});}
            var sketch = newSketch(context, id + "F56", { "sketchPlane" : qUnion([Q0])});
            skText(sketch, "E917", { "text": "S5", "fontName": "OpenSans-Bold.ttf"});
            skText(sketch, "E918", { "text": "S4", "fontName": "OpenSans-Bold.ttf"});
            const initialGuessF56  = {"E917": [-0.03102, 0.00035, 1, 0, 0.00488], "E918": [0.00797, 0.0003, 1, 0, 0.0048]};
            skSetInitialGuess(sketch, initialGuessF56);
            skSolve(sketch);
        }
        {
            var Q0;
            Q0=qSketchRegion(id+"F56",true);
            extrude(context, id + "F57", {"entities" : qUnion([Q0]), "operationType" : NewBodyOperationType.REMOVE, "oppositeDirection" : true, "depth" : 1 * mm});
        }
        {
            var Q0;
            {var subQ0=sQuery(id+"F12.wireOp",EDGE,"E53");Q0=makeQuery(id+"F12.imprint","IMPRINT",FACE,{"disambiguationData":[TD([[makeQuery(id+"F12.imprint","IMPRINT",EDGE,{"derivedFrom":subQ0}),-1.0]])]});}
            extrude(context, id + "F58", {"entities" : qUnion([Q0]), "operationType" : NewBodyOperationType.REMOVE, "oppositeDirection" : true, "depth" : 8 * mm});
        }
        {
            var Q0;
            Q0=makeQuery(id+"F0.imprint","IMPRINT",FACE,{"disambiguationData":[TD([[makeQuery(id+"F0.imprint","IMPRINT",EDGE,{"derivedFrom":sQuery(id+"F0.wireOp",EDGE,"E1")}),-1.0]])]});
            var sketch = newSketch(context, id + "F59", { "sketchPlane" : qUnion([Q0])});
            skPoint(sketch, "E919.first.point", {"position": v(6.62, 7.4) * mm});
            skPoint(sketch, "E919.second.point", {"position": v(6.67, 13.38) * mm});
            skPoint(sketch, "E919.third.point", {"position": v(3.73, 10.32) * mm});
            skPoint(sketch, "E920.first.point", {"position": v(17.45, 10.32) * mm});
            skPoint(sketch, "E920.second.point", {"position": v(14.7, 13.34) * mm});
            skPoint(sketch, "E920.third.point", {"position": v(14.7, 7.45) * mm});
            skPoint(sketch, "E921.MirrorP", {"position": v(17.5, 10.32) * mm});
            skPoint(sketch, "E922.MirrorP", {"position": v(14.62, 7.4) * mm});
            skPoint(sketch, "E923.MirrorP", {"position": v(14.57, 13.38) * mm});
            skLineSegment(sketch, "E924", {"start": v(14.46, 6.75) * mm, "end": v(6.63, 6.75) * mm});
            skLineSegment(sketch, "E925", {"start": v(14.66, 13.88) * mm, "end": v(6.96, 13.88) * mm});
            skArc(sketch, "E926.trimOffspring", {"start": v(6.96, 13.88) * mm, "mid": v(3.17, 10.38) * mm, "end": v(6.84, 6.75) * mm});
            skArc(sketch, "E927.trimOffspring", {"start": v(14.27, 13.88) * mm, "mid": v(18.08, 10.42) * mm, "end": v(14.46, 6.75) * mm});
            skPoint(sketch, "E928.orphan", {"position": v(14.5, 10.4) * mm});
            skPoint(sketch, "E929.start.orphan", {"position": v(10.62, 10.36) * mm});
            skCircle(sketch, "E930", {"center": v(6.74, 10.32) * mm, "radius": 2.01 * mm});
            skCircle(sketch, "E931", {"center": v(14.51, 10.32) * mm, "radius": 2.16 * mm});
            skLineSegment(sketch, "E932.trimOffspring", {"start": v(6.52, 13.88) * mm, "end": v(6.5, 13.88) * mm});
            skSolve(sketch);
        }
        {
            var Q0;
            Q0=qSketchRegion(id+"F59",true);
            extrude(context, id + "F60", {"entities" : qUnion([Q0]), "operationType" : NewBodyOperationType.REMOVE, "depth" : 8.2 * mm});
        }
    });
